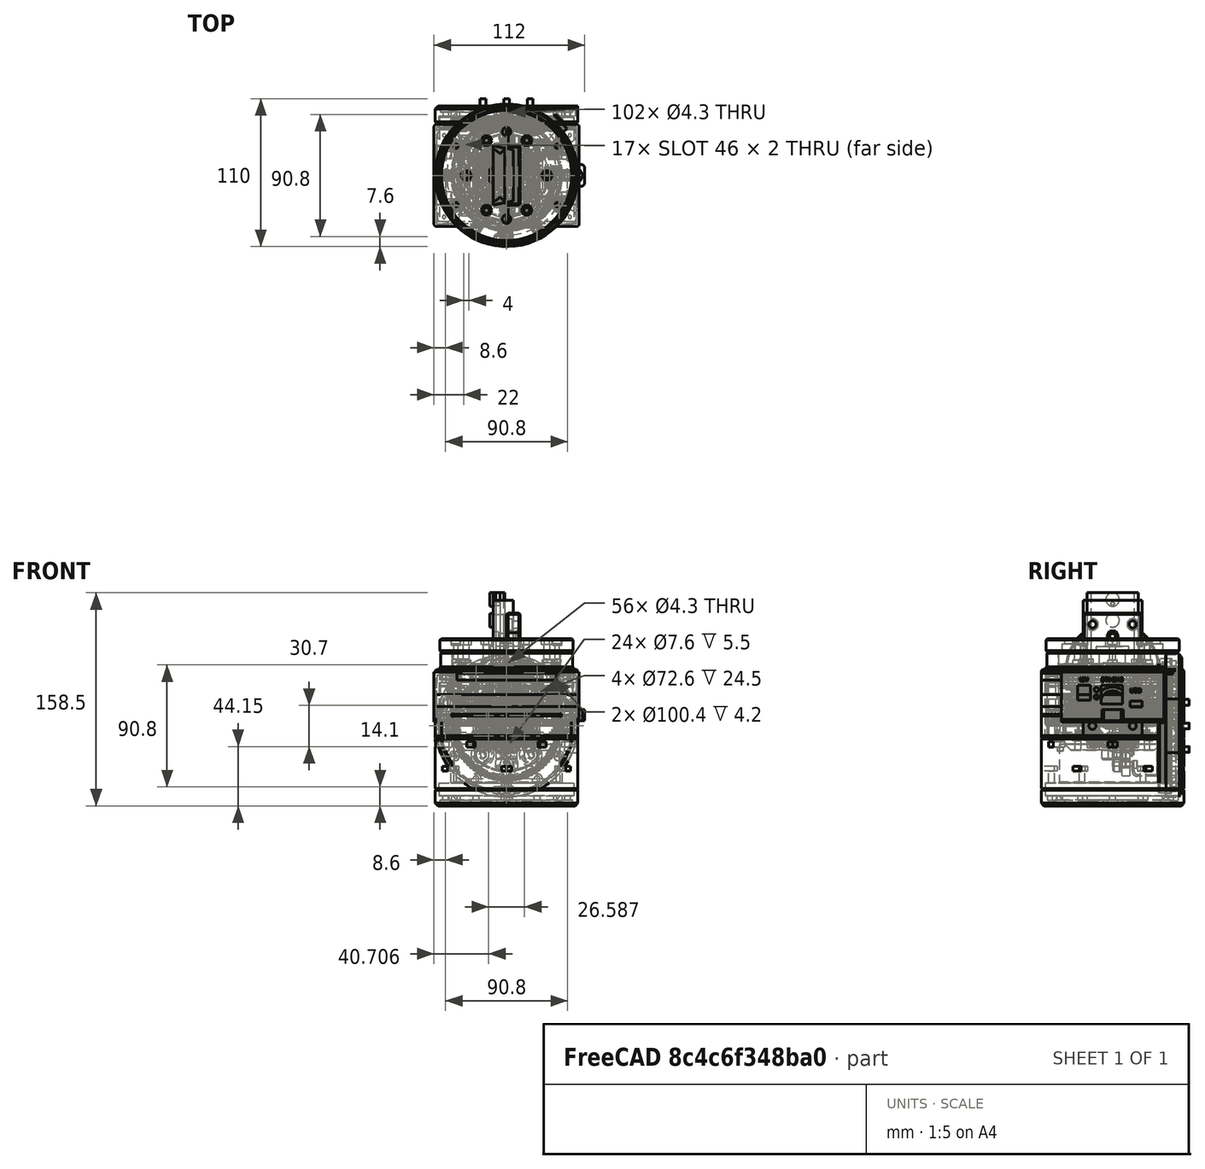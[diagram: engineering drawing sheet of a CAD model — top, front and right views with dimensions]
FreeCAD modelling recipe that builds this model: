
FCSTD DOCUMENT  (FreeCAD 0.19R)
Label: HrEM
License: All rights reserved
LicenseURL: http://en.wikipedia.org/wiki/All_rights_reserved
objects: Part::Cylinder×298, Part::Refine×224, Part::MultiFuse×180, Part::Box×74, Part::Cut×71, Part::Prism×45, Part::Feature×42, Part::Chamfer×30, Part::FeaturePython×20, Part::Part2DObjectPython×13, Part::Extrusion×12, Part::Fillet×5, Part::Fuse×4, App::Part×3
note: 1018 computed .brp shape members not serialized (recipe doc carries the construction recipe); baked Part::Feature solids carry a one-line shape summary decoded from their .brp

FEATURE [Part::Feature] Part__Feature048  label="OUTPUT_SHAFT"
  Placement = pos=(0,0,-16) rot=(1,0,0;1.5708rad)
  shape: bbox 70.02 x 70.02 x 15.12 mm, 150 faces (baked)
FEATURE [Part::Feature] Part__Feature015  label="CIRCULAR_SPLINE"
  Placement = pos=(-3.943e-12,44,4.322e-12) rot=(1,0,0;3.14159rad)
  shape: bbox 100 x 10 x 100 mm, 706 faces (baked)
FEATURE [Part::Feature] Part__Feature014  label="FLEXGEAR"
  Placement = pos=(0,33.5,0) rot=(0,0,1;0rad)
  shape: bbox 81.18 x 57.96 x 81.18 mm, 699 faces (baked)
FEATURE [Part::FeaturePython] cycloidgear  # WARN: FeaturePython — macro-defined, semantics opaque (R4)
  AttacherType = Attacher::AttachEngine3D
  Placement = pos=(0,44,0) rot=(1,0,0;1.5708rad)
  backlash = 0
  beta = 0
  clearance = 0.25
  double_helix = false
  head = 0
  height = 10
  inner_diameter = 5
  module = 1
  numpoints = 15
  outer_diameter = 5
  teeth = 79
  version = 0.0.3
FEATURE [Part::Cylinder] Cylinder  label="Válec"
  Angle = 360
  AttacherType = Attacher::AttachEngine3D
  Height = 10
  Placement = pos=(0,44,0) rot=(1,0,0;1.5708rad)
  Radius = 50
FEATURE [Part::Cylinder] Cylinder001  label="Válec001"
  Angle = 360
  AttacherType = Attacher::AttachEngine3D
  Height = 10
  Placement = pos=(0,44,45.4) rot=(1,0,0;1.5708rad)
  Radius = 2.15
FEATURE [Part::Refine] Cylinder001001  label="Válec002"
  Placement = pos=(0,0,0) rot=(0,1,0;1.0472rad)
  Source = -> Cylinder001
FEATURE [Part::Refine] Cylinder001002  label="Válec003"
  Placement = pos=(0,0,0) rot=(0,1,0;2.0944rad)
  Source = -> Cylinder001
FEATURE [Part::Refine] Cylinder001003  label="Válec004"
  Placement = pos=(0,0,0) rot=(0,1,0;3.14159rad)
  Source = -> Cylinder001
FEATURE [Part::Refine] Cylinder001004  label="Válec005"
  Placement = pos=(0,0,0) rot=(0,1,0;4.18879rad)
  Source = -> Cylinder001
FEATURE [Part::Refine] Cylinder001005  label="Válec006"
  Placement = pos=(0,0,0) rot=(0,-1,0;1.0472rad)
  Source = -> Cylinder001
FEATURE [Part::MultiFuse] Fusion
  Shapes = -> [cycloidgear,Cylinder001,Cylinder001001,Cylinder001002,Cylinder001003,Cylinder001004,Cylinder001005]
FEATURE [Part::Chamfer] Chamfer
  Base = -> Cylinder
  Edges = 2 edges r=1: [Edge1,Edge3]
FEATURE [Part::Cut] Cut  label="CIRCULAR_79"
  Base = -> Chamfer
  Tool = -> Fusion
FEATURE [Part::Cylinder] Cylinder001006  label="Válec007"
  Angle = 360
  AttacherType = Attacher::AttachEngine3D
  Height = 10
  Placement = pos=(0,44,0) rot=(1,0,0;1.5708rad)
  Radius = 50
FEATURE [Part::FeaturePython] cycloidgear001  # WARN: FeaturePython — macro-defined, semantics opaque (R4)
  AttacherType = Attacher::AttachEngine3D
  Placement = pos=(0,43.5,0) rot=(1,0,0;1.5708rad)
  backlash = 0
  beta = 0
  clearance = 0.25
  double_helix = false
  head = 0
  height = 11
  inner_diameter = 5
  module = 0.55
  numpoints = 15
  outer_diameter = 5
  teeth = 145
  version = 0.0.3
FEATURE [Part::Cylinder] Cylinder001007  label="Válec008"
  Angle = 360
  AttacherType = Attacher::AttachEngine3D
  Height = 10
  Placement = pos=(0,44,45.4) rot=(1,0,0;1.5708rad)
  Radius = 2.15
FEATURE [Part::Chamfer] Chamfer001
  Base = -> Cylinder001006
  Edges = 2 edges r=1: [Edge1,Edge3]
FEATURE [Part::Refine] Cylinder001008  label="Válec009"
  Placement = pos=(0,0,0) rot=(0,1,0;2.0944rad)
  Source = -> Cylinder001007
FEATURE [Part::Refine] Cylinder001009  label="Válec010"
  Placement = pos=(0,0,0) rot=(0,1,0;1.0472rad)
  Source = -> Cylinder001007
FEATURE [Part::Refine] Cylinder001010  label="Válec011"
  Placement = pos=(0,0,0) rot=(0,1,0;4.18879rad)
  Source = -> Cylinder001007
FEATURE [Part::Refine] Cylinder001011  label="Válec012"
  Placement = pos=(0,0,0) rot=(0,-1,0;1.0472rad)
  Source = -> Cylinder001007
FEATURE [Part::Refine] Cylinder001012  label="Válec013"
  Placement = pos=(0,0,0) rot=(0,1,0;3.14159rad)
  Source = -> Cylinder001007
FEATURE [Part::MultiFuse] Fusion001
  Shapes = -> [cycloidgear001,Cylinder001007,Cylinder001009,Cylinder001008,Cylinder001012,Cylinder001010,Cylinder001011]
FEATURE [Part::Cut] Cut001  label="CIRCULAR_145"
  Base = -> Chamfer001
  Tool = -> Fusion001
FEATURE [Part::Cylinder] Cylinder001014  label="Válec015"
  Angle = 360
  AttacherType = Attacher::AttachEngine3D
  Height = 10
  Placement = pos=(0,44,0) rot=(1,0,0;1.5708rad)
  Radius = 50
FEATURE [Part::Cylinder] Cylinder001017  label="Válec018"
  Angle = 360
  AttacherType = Attacher::AttachEngine3D
  Height = 10
  Placement = pos=(0,44,45.4) rot=(1,0,0;1.5708rad)
  Radius = 2.15
FEATURE [Part::Refine] Cylinder001013  label="Válec014"
  Placement = pos=(0,0,0) rot=(0,-1,0;1.0472rad)
  Source = -> Cylinder001017
FEATURE [Part::Refine] Cylinder001015  label="Válec016"
  Placement = pos=(0,0,0) rot=(0,1,0;2.0944rad)
  Source = -> Cylinder001017
FEATURE [Part::Refine] Cylinder001016  label="Válec017"
  Placement = pos=(0,0,0) rot=(0,1,0;4.18879rad)
  Source = -> Cylinder001017
FEATURE [Part::FeaturePython] cycloidgear002  # WARN: FeaturePython — macro-defined, semantics opaque (R4)
  AttacherType = Attacher::AttachEngine3D
  Placement = pos=(0,44,0) rot=(1,0,0;1.5708rad)
  backlash = 0
  beta = 30
  clearance = 0.25
  double_helix = false
  head = 0
  height = 10
  inner_diameter = 5
  module = 0.792
  numpoints = 15
  outer_diameter = 5
  teeth = 101
  version = 0.0.3
FEATURE [Part::Chamfer] Chamfer002
  Base = -> Cylinder001014
  Edges = 2 edges r=1: [Edge1,Edge3]
FEATURE [Part::Refine] Cylinder001018  label="Válec019"
  Placement = pos=(0,0,0) rot=(0,1,0;1.0472rad)
  Source = -> Cylinder001017
FEATURE [Part::Refine] Cylinder001019  label="Válec020"
  Placement = pos=(0,0,0) rot=(0,1,0;3.14159rad)
  Source = -> Cylinder001017
FEATURE [Part::MultiFuse] Fusion002
  Shapes = -> [cycloidgear002,Cylinder001017,Cylinder001018,Cylinder001015,Cylinder001019,Cylinder001016,Cylinder001013]
FEATURE [Part::Cut] Cut002  label="CIRCULAR_101"
  Base = -> Chamfer002
  Tool = -> Fusion002
FEATURE [Part::FeaturePython] cycloidgear003  # WARN: FeaturePython — macro-defined, semantics opaque (R4)
  AttacherType = Attacher::AttachEngine3D
  Placement = pos=(0,44,0) rot=(1,0,0;1.5708rad)
  backlash = 0
  beta = 30
  clearance = 0.25
  double_helix = false
  head = 0
  height = 11
  inner_diameter = 5
  module = 0.792
  numpoints = 15
  outer_diameter = 5
  teeth = 101
  version = 0.0.3
FEATURE [Part::Cylinder] Cylinder001023  label="Válec024"
  Angle = 360
  AttacherType = Attacher::AttachEngine3D
  Height = 10
  Placement = pos=(0,44,45.4) rot=(1,0,0;1.5708rad)
  Radius = 2.15
FEATURE [Part::Refine] Cylinder001020  label="Válec021"
  Placement = pos=(0,0,0) rot=(0,1,0;4.18879rad)
  Source = -> Cylinder001023
FEATURE [Part::Refine] Cylinder001021  label="Válec022"
  Placement = pos=(0,0,0) rot=(0,-1,0;1.0472rad)
  Source = -> Cylinder001023
FEATURE [Part::Refine] Cylinder001022  label="Válec023"
  Placement = pos=(0,0,0) rot=(0,1,0;2.0944rad)
  Source = -> Cylinder001023
FEATURE [Part::Refine] Cylinder001024  label="Válec025"
  Placement = pos=(0,0,0) rot=(0,1,0;3.14159rad)
  Source = -> Cylinder001023
FEATURE [Part::Refine] Cylinder001025  label="Válec026"
  Placement = pos=(0,0,0) rot=(0,1,0;1.0472rad)
  Source = -> Cylinder001023
FEATURE [Part::MultiFuse] Fusion003
  Shapes = -> [cycloidgear003,Cylinder001023,Cylinder001025,Cylinder001022,Cylinder001024,Cylinder001020,Cylinder001021]
FEATURE [Part::Cylinder] Cylinder001026  label="Válec027"
  Angle = 360
  AttacherType = Attacher::AttachEngine3D
  Height = 10
  Placement = pos=(0,44,0) rot=(1,0,0;1.5708rad)
  Radius = 50
FEATURE [Part::Chamfer] Chamfer003
  Base = -> Cylinder001026
  Edges = 2 edges r=1: [Edge1,Edge3]
FEATURE [Part::Cut] Cut003
  Base = -> Chamfer003
  Tool = -> Fusion003
FEATURE [Part::Cylinder] cylinder
  Angle = 360
  AttacherType = Attacher::AttachEngine3D
  Height = 10
  Radius = 3
FEATURE [Part::Cylinder] cylinder001
  Angle = 360
  AttacherType = Attacher::AttachEngine3D
  Height = 10
  Placement = pos=(15,0,0) rot=(0,0,1;0rad)
  Radius = 3.5
FEATURE [Part::Cylinder] cylinder002
  Angle = 360
  AttacherType = Attacher::AttachEngine3D
  Height = 5
  Placement = pos=(15,0,0) rot=(0,0,1;0rad)
  Radius = 7
FEATURE [Part::Cylinder] cylinder003
  Angle = 360
  AttacherType = Attacher::AttachEngine3D
  Height = 10
  Placement = pos=(-15,0,0) rot=(0,0,1;0rad)
  Radius = 3.5
FEATURE [Part::Cylinder] cylinder004
  Angle = 360
  AttacherType = Attacher::AttachEngine3D
  Height = 5
  Placement = pos=(-15,0,0) rot=(0,0,1;0rad)
  Radius = 7
FEATURE [Part::Cylinder] cylinder005
  Angle = 360
  AttacherType = Attacher::AttachEngine3D
  Height = 10
  Placement = pos=(-25,0,0) rot=(0,0,1;0rad)
  Radius = 2.6
FEATURE [Part::Cylinder] cylinder006
  Angle = 360
  AttacherType = Attacher::AttachEngine3D
  Height = 10
  Placement = pos=(25,0,0) rot=(0,0,1;0rad)
  Radius = 2.6
FEATURE [Part::MultiFuse] union
  Shapes = -> [cylinder,cylinder001,cylinder002,cylinder003,cylinder004,cylinder005,cylinder006]
FEATURE [Part::Cylinder] Cylinder001027  label="Válec028"
  Angle = 360
  AttacherType = Attacher::AttachEngine3D
  Height = 10
  Radius = 35
FEATURE [Part::Cut] Cut004  label="H1"
  Base = -> Cylinder001027
  Placement = pos=(0,0,10) rot=(0,0,1;0rad)
  Tool = -> union
FEATURE [Part::Cylinder] Cylinder001028  label="H2"
  Angle = 360
  AttacherType = Attacher::AttachEngine3D
  Height = 10
  Radius = 35
FEATURE [Part::Cylinder] Cylinder001029  label="Válec030"
  Angle = 360
  AttacherType = Attacher::AttachEngine3D
  Height = 16
  Placement = pos=(0,24,-6) rot=(0,0,1;0rad)
  Radius = 2.15
FEATURE [Part::Cylinder] cylinder007
  Angle = 360
  AttacherType = Attacher::AttachEngine3D
  Height = 10
  Placement = pos=(-25,0,0) rot=(0,0,1;0rad)
  Radius = 2.6
FEATURE [Part::Cylinder] cylinder008
  Angle = 360
  AttacherType = Attacher::AttachEngine3D
  Height = 10
  Placement = pos=(25,0,0) rot=(0,0,1;0rad)
  Radius = 2.6
FEATURE [Part::Cylinder] cylinder009
  Angle = 360
  AttacherType = Attacher::AttachEngine3D
  Height = 10
  Radius = 3
FEATURE [Part::Cylinder] Cylinder001030  label="Válec031"
  Angle = 360
  AttacherType = Attacher::AttachEngine3D
  Height = 4
  Placement = pos=(0,24,6) rot=(0,0,1;0rad)
  Radius = 3.6
FEATURE [Part::MultiFuse] Fusion004  label="Imbus"
  Shapes = -> [Cylinder001030,Cylinder001029]
FEATURE [Part::Refine] Fusion004001  label="Imbus001"
  Placement = pos=(0,0,0) rot=(0,0,1;1.0472rad)
  Source = -> Fusion004
FEATURE [Part::Refine] Fusion004002  label="Imbus002"
  Placement = pos=(0,0,0) rot=(0,0,1;2.0944rad)
  Source = -> Fusion004
FEATURE [Part::Refine] Fusion004003  label="Imbus003"
  Placement = pos=(0,0,0) rot=(0,0,1;3.14159rad)
  Source = -> Fusion004
FEATURE [Part::Refine] Fusion004004  label="Imbus004"
  Placement = pos=(0,0,0) rot=(0,0,1;4.18879rad)
  Source = -> Fusion004
FEATURE [Part::Refine] Fusion004005  label="Imbus005"
  Placement = pos=(0,0,0) rot=(0,0,-1;1.0472rad)
  Source = -> Fusion004
FEATURE [Part::FeaturePython] Nut  label="M5-Nut"  # Fasteners workbench fastener (typed FeaturePython)
  Placement = pos=(25,0,0) rot=(0.894427,0,0.447214;0rad)
  diameter = 7
  invert = false
  matchOuter = false
  offset = 0
  thread = false
  type = 7
FEATURE [Part::FeaturePython] Nut001  label="M5-Nut001"  # Fasteners workbench fastener (typed FeaturePython)
  Placement = pos=(-25,0,0) rot=(0.894427,0,0.447214;0rad)
  diameter = 7
  invert = false
  matchOuter = false
  offset = 0
  thread = false
  type = 7
FEATURE [Part::MultiFuse] Fusion004006
  Shapes = -> [cylinder007,cylinder008,cylinder009,Fusion004,Fusion004001,Fusion004002,Fusion004003,Fusion004004,Fusion004005,Nut,Nut001]
FEATURE [Part::Cut] Cut005
  Base = -> Cylinder001028
  Tool = -> Fusion004006
FEATURE [Part::Chamfer] Chamfer004  label="HH1"
  Base = -> Cut004
  Edges = 2 edges r=1: [Edge1,Edge3]
FEATURE [Part::Chamfer] Chamfer005  label="HH2"
  Base = -> Cut005
  Edges = 2 edges r=1: [Edge1,Edge3]
FEATURE [Part::Feature] Part__Feature049  label="FLEXGEAR001"
  Placement = pos=(0,33.5,0) rot=(0,0,1;0rad)
  shape: bbox 81.18 x 57.96 x 81.18 mm, 699 faces (baked)
FEATURE [Part::FeaturePython] cycloidgear005  # WARN: FeaturePython — macro-defined, semantics opaque (R4)
  AttacherType = Attacher::AttachEngine3D
  Placement = pos=(0,43.5,0) rot=(1,0,0;1.5708rad)
  backlash = 0
  beta = 0
  clearance = 0.25
  double_helix = false
  head = 0
  height = 10.5
  inner_diameter = 5
  module = 0.79
  numpoints = 15
  outer_diameter = 5
  teeth = 100
  version = 0.0.3
FEATURE [Part::FeaturePython] Tube  # WARN: FeaturePython — macro-defined, semantics opaque (R4)
  AttacherType = Attacher::AttachEngine3D
  Height = 10
  InnerRadius = 36.5
  OuterRadius = 42
  Placement = pos=(0,35.75,0) rot=(1,0,0;1.5708rad)
FEATURE [Part::Chamfer] Chamfer007
  Base = -> Tube
  Edges = 1 edges r=4: [Edge5]
FEATURE [Part::Cut] Cut007
  Base = -> cycloidgear005
  Tool = -> Chamfer007
FEATURE [Part::Cylinder] Cylinder001038  label="Válec039"
  Angle = 360
  AttacherType = Attacher::AttachEngine3D
  Height = 10.5
  Placement = pos=(0,43.5,0) rot=(1,0,0;1.5708rad)
  Radius = 42
FEATURE [Part::Cylinder] Cylinder001039  label="Válec040"
  Angle = 360
  AttacherType = Attacher::AttachEngine3D
  Height = 10.5
  Placement = pos=(0,43.5,0) rot=(1,0,0;1.5708rad)
  Radius = 36.3
FEATURE [Part::Cut] Cut008
  Base = -> Part__Feature049
  Tool = -> Cylinder001038
FEATURE [Part::MultiFuse] Fusion004008
  Shapes = -> [Cut007,Cut008]
FEATURE [Part::Cut] Cut009  label="FLEX100"
  Base = -> Fusion004008
  Tool = -> Cylinder001039
FEATURE [Part::Refine] Cut009001  label="FLEX100n"
  Source = -> Cut009
FEATURE [Part::FeaturePython] cycloidgear006  # WARN: FeaturePython — macro-defined, semantics opaque (R4)
  AttacherType = Attacher::AttachEngine3D
  Placement = pos=(0,43.5,0) rot=(1,0,0;1.5708rad)
  backlash = 0
  beta = 0
  clearance = 0.25
  double_helix = false
  head = 0
  height = 10.5
  inner_diameter = 5
  module = 1
  numpoints = 15
  outer_diameter = 5
  teeth = 78
  version = 0.0.3
FEATURE [Part::Feature] Part__Feature050  label="FLEXGEAR002"
  Placement = pos=(0,33.5,0) rot=(0,0,1;0rad)
  shape: bbox 81.18 x 57.96 x 81.18 mm, 699 faces (baked)
FEATURE [Part::FeaturePython] Tube001  # WARN: FeaturePython — macro-defined, semantics opaque (R4)
  AttacherType = Attacher::AttachEngine3D
  Height = 10
  InnerRadius = 36.5
  OuterRadius = 42
  Placement = pos=(0,35.75,0) rot=(1,0,0;1.5708rad)
FEATURE [Part::Chamfer] Chamfer008
  Base = -> Tube001
  Edges = 1 edges r=4: [Edge5]
FEATURE [Part::Cut] Cut009002
  Base = -> cycloidgear006
  Tool = -> Chamfer008
FEATURE [Part::Cylinder] Cylinder001040  label="Válec041"
  Angle = 360
  AttacherType = Attacher::AttachEngine3D
  Height = 11.5
  Placement = pos=(0,43.5,0) rot=(1,0,0;1.5708rad)
  Radius = 36.3
FEATURE [Part::Cylinder] Cylinder001041  label="Válec042"
  Angle = 360
  AttacherType = Attacher::AttachEngine3D
  Height = 10.5
  Placement = pos=(0,43.5,0) rot=(1,0,0;1.5708rad)
  Radius = 42
FEATURE [Part::Cut] Cut009004
  Base = -> Part__Feature050
  Tool = -> Cylinder001041
FEATURE [Part::MultiFuse] Fusion004009
  Shapes = -> [Cut009002,Cut009004]
FEATURE [Part::Cut] Cut009003  label="FLEX78"
  Base = -> Fusion004009
  Tool = -> Cylinder001040
FEATURE [Part::Refine] Cut009003001  label="FLEX78n"
  Source = -> Cut009003
FEATURE [Part::FeaturePython] cycloidgear007  # WARN: FeaturePython — macro-defined, semantics opaque (R4)
  AttacherType = Attacher::AttachEngine3D
  Placement = pos=(0,43.5,0) rot=(1,0,0;1.5708rad)
  backlash = 0
  beta = 0
  clearance = 0.25
  double_helix = false
  head = 0
  height = 10.5
  inner_diameter = 5
  module = 0.55
  numpoints = 15
  outer_diameter = 5
  teeth = 144
  version = 0.0.3
FEATURE [Part::Feature] Part__Feature051  label="FLEXGEAR003"
  Placement = pos=(0,33.5,0) rot=(0,0,1;0rad)
  shape: bbox 81.18 x 57.96 x 81.18 mm, 699 faces (baked)
FEATURE [Part::FeaturePython] Tube002  # WARN: FeaturePython — macro-defined, semantics opaque (R4)
  AttacherType = Attacher::AttachEngine3D
  Height = 10
  InnerRadius = 36.5
  OuterRadius = 42
  Placement = pos=(0,35.75,0) rot=(1,0,0;1.5708rad)
FEATURE [Part::Chamfer] Chamfer009
  Base = -> Tube002
  Edges = 1 edges r=4: [Edge5]
FEATURE [Part::Cut] Cut009003002
  Base = -> cycloidgear007
  Tool = -> Chamfer009
FEATURE [Part::Cylinder] Cylinder001042  label="Válec043"
  Angle = 360
  AttacherType = Attacher::AttachEngine3D
  Height = 11.5
  Placement = pos=(0,43.5,0) rot=(1,0,0;1.5708rad)
  Radius = 36.3
FEATURE [Part::Cylinder] Cylinder001043  label="Válec044"
  Angle = 360
  AttacherType = Attacher::AttachEngine3D
  Height = 10.5
  Placement = pos=(0,43.5,0) rot=(1,0,0;1.5708rad)
  Radius = 42
FEATURE [Part::Cut] Cut009003004
  Base = -> Part__Feature051
  Tool = -> Cylinder001043
FEATURE [Part::MultiFuse] Fusion004010
  Shapes = -> [Cut009003002,Cut009003004]
FEATURE [Part::Cut] Cut009003003  label="FLEX144"
  Base = -> Fusion004010
  Tool = -> Cylinder001042
FEATURE [Part::Refine] Cut009003003001  label="FLEX144n"
  Source = -> Cut009003003
FEATURE [Part::Feature] Part__Feature030  label="MOTOR_CAP"
  Placement = pos=(0,0,0) rot=(0,1,0;0.523599rad)
  shape: bbox 106 x 12.2 x 106 mm, 94 faces (baked)
FEATURE [Part::Cylinder] Cylinder014005699  label="Válec616"
  Angle = 360
  AttacherType = Attacher::AttachEngine3D
  Height = 10
  Placement = pos=(-9.9,9.9,0) rot=(0,0,1;0rad)
  Radius = 1.6
FEATURE [Part::Cylinder] Cylinder014005700  label="Válec617"
  Angle = 360
  AttacherType = Attacher::AttachEngine3D
  Height = 10
  Placement = pos=(-9.9,-9.9,0) rot=(0,0,1;0rad)
  Radius = 1.6
FEATURE [Part::Cylinder] Cylinder014005701  label="Válec618"
  Angle = 360
  AttacherType = Attacher::AttachEngine3D
  Height = 10
  Placement = pos=(9.9,-9.9,0) rot=(0,0,1;0rad)
  Radius = 1.6
FEATURE [Part::Cylinder] Cylinder014005703  label="Válec619"
  Angle = 360
  AttacherType = Attacher::AttachEngine3D
  Height = 10
  Placement = pos=(9.9,9.9,0) rot=(0,0,1;0rad)
  Radius = 1.6
FEATURE [Part::MultiFuse] Fusion004011  label="Diry PG"
  Shapes = -> [Cylinder014005699,Cylinder014005703,Cylinder014005700,Cylinder014005701]
FEATURE [Part::Box] Box001  label="Krychle001"
  AttacherType = Attacher::AttachEngine3D
  Height = 40
  Length = 10
  Placement = pos=(43,39.5,-20) rot=(0,0,1;0rad)
  Width = 12
FEATURE [Part::Cylinder] Cylinder014005822  label="Válec735"
  Angle = 360
  AttacherType = Attacher::AttachEngine3D
  Height = 12
  Placement = pos=(0,51.5,0) rot=(1,0,0;1.5708rad)
  Radius = 51
FEATURE [Part::FeaturePython] Tube003  label="B6010"  # WARN: FeaturePython — macro-defined, semantics opaque (R4)
  AttacherType = Attacher::AttachEngine3D
  Height = 16
  InnerRadius = 25
  OuterRadius = 40
FEATURE [Part::Cut] Cut009003003003  label="Lista prac"
  Base = -> Box001
  Tool = -> Cylinder014005822
FEATURE [Part::Cylinder] Cylinder014005826  label="Válec739"
  Angle = 360
  AttacherType = Attacher::AttachEngine3D
  Height = 4
  Placement = pos=(0,17.5,0) rot=(0,0,1;0rad)
  Radius = 3.6
FEATURE [Part::Cylinder] Cylinder014005827  label="Válec740"
  Angle = 360
  AttacherType = Attacher::AttachEngine3D
  Height = 4
  Placement = pos=(-17.5,0,0) rot=(0,0,1;0rad)
  Radius = 3.6
FEATURE [Part::Cylinder] Cylinder014005828  label="Válec741"
  Angle = 360
  AttacherType = Attacher::AttachEngine3D
  Height = 4
  Placement = pos=(17.5,0,0) rot=(0,0,1;0rad)
  Radius = 3.6
FEATURE [Part::Cylinder] Cylinder014005834  label="Válec747"
  Angle = 360
  AttacherType = Attacher::AttachEngine3D
  Height = 4
  Placement = pos=(0,-17.5,0) rot=(0,0,1;0rad)
  Radius = 3.6
FEATURE [Part::MultiFuse] Fusion001089086  label="Diry HG002"
  Placement = pos=(0,0,-1) rot=(0,0,1;0rad)
  Shapes = -> [Cylinder014005828,Cylinder014005834,Cylinder014005827,Cylinder014005826]
FEATURE [Part::Cylinder] Cylinder014005835  label="Válec748"
  Angle = 360
  AttacherType = Attacher::AttachEngine3D
  Height = 10
  Placement = pos=(17.5,0,0) rot=(0,0,1;0rad)
  Radius = 2.15
FEATURE [Part::Cylinder] Cylinder014005836  label="Válec749"
  Angle = 360
  AttacherType = Attacher::AttachEngine3D
  Height = 10
  Placement = pos=(-17.5,0,0) rot=(0,0,1;0rad)
  Radius = 2.15
FEATURE [Part::Cylinder] Cylinder014005837  label="Válec750"
  Angle = 360
  AttacherType = Attacher::AttachEngine3D
  Height = 10
  Placement = pos=(0,17.5,0) rot=(0,0,1;0rad)
  Radius = 2.15
FEATURE [Part::Cylinder] Cylinder014005838  label="Válec751"
  Angle = 360
  AttacherType = Attacher::AttachEngine3D
  Height = 10
  Placement = pos=(0,-17.5,0) rot=(0,0,1;0rad)
  Radius = 2.15
FEATURE [Part::MultiFuse] Fusion001089087  label="Diry HG003"
  Shapes = -> [Cylinder014005835,Cylinder014005838,Cylinder014005836,Cylinder014005837]
FEATURE [Part::MultiFuse] Fusion001089085  label="GeerHD"
  Placement = pos=(0,47,0) rot=(-1,0,0;1.5708rad)
  Shapes = -> [Fusion001089087,Fusion001089086]
FEATURE [Part::Cylinder] Cylinder014005814  label="Válec727"
  Angle = 360
  AttacherType = Attacher::AttachEngine3D
  Height = 3
  Placement = pos=(9.9,9.9,0) rot=(0,0,1;0rad)
  Radius = 2.8
FEATURE [Part::Cylinder] Cylinder014005815  label="Válec728"
  Angle = 360
  AttacherType = Attacher::AttachEngine3D
  Height = 3
  Placement = pos=(9.9,-9.9,0) rot=(0,0,1;0rad)
  Radius = 2.8
FEATURE [Part::Cylinder] Cylinder014005816  label="Válec729"
  Angle = 360
  AttacherType = Attacher::AttachEngine3D
  Height = 3
  Placement = pos=(-9.9,-9.9,0) rot=(0,0,1;0rad)
  Radius = 2.8
FEATURE [Part::Cylinder] Cylinder014005817  label="Válec730"
  Angle = 360
  AttacherType = Attacher::AttachEngine3D
  Height = 3
  Placement = pos=(-9.9,9.9,0) rot=(0,0,1;0rad)
  Radius = 2.8
FEATURE [Part::MultiFuse] Fusion001089081  label="Diry PG001"
  Shapes = -> [Cylinder014005817,Cylinder014005814,Cylinder014005816,Cylinder014005815]
FEATURE [Part::MultiFuse] Fusion001089083  label="GeerPG"
  Placement = pos=(0,47,0) rot=(-1,0,0;1.5708rad)
  Shapes = -> [Fusion004011,Fusion001089081]
FEATURE [Part::Feature] Part__Feature052  label="MOTOR_CAP001"
  Placement = pos=(0,0,0) rot=(0,1,0;0.523599rad)
  shape: bbox 106 x 12.2 x 106 mm, 94 faces (baked)
FEATURE [Part::Cut] Cut009003003004  label="MotorPG"
  Base = -> Part__Feature052
  Tool = -> Fusion001089083
FEATURE [Part::Feature] Cut005_solid  label="Planetary Gear Box distance  RA"
  shape: bbox 41 x 41 x 22.5 mm, 15 faces (baked)
FEATURE [Part::Cylinder] Cylinder014005839  label="Válec752"
  Angle = 360
  AttacherType = Attacher::AttachEngine3D
  Height = 22.5
  Placement = pos=(15.5,15.5,0) rot=(0,0,1;0rad)
  Radius = 1.3
FEATURE [Part::Cylinder] Cylinder014005840  label="Válec753"
  Angle = 360
  AttacherType = Attacher::AttachEngine3D
  Height = 22.5
  Placement = pos=(-15.5,15.5,0) rot=(0,0,1;0rad)
  Radius = 1.3
FEATURE [Part::Cylinder] Cylinder014005841  label="Válec754"
  Angle = 360
  AttacherType = Attacher::AttachEngine3D
  Height = 22.5
  Placement = pos=(15.5,-15.5,0) rot=(0,0,1;0rad)
  Radius = 1.3
FEATURE [Part::Cylinder] Cylinder014005842  label="Válec755"
  Angle = 360
  AttacherType = Attacher::AttachEngine3D
  Height = 22.5
  Placement = pos=(-15.5,-15.5,0) rot=(0,0,1;0rad)
  Radius = 1.3
FEATURE [Part::MultiFuse] Fusion001089088
  Shapes = -> [Cylinder014005839,Cylinder014005840,Cylinder014005841,Cylinder014005842]
FEATURE [Part::Cylinder] Cylinder014005843  label="Válec756"
  Angle = 360
  AttacherType = Attacher::AttachEngine3D
  Height = 22.5
  Placement = pos=(15.5,15.5,0) rot=(0,0,1;0rad)
  Radius = 2
FEATURE [Part::Cylinder] Cylinder014005844  label="Válec757"
  Angle = 360
  AttacherType = Attacher::AttachEngine3D
  Height = 22.5
  Placement = pos=(-15.5,15.5,0) rot=(0,0,1;0rad)
  Radius = 2
FEATURE [Part::Cylinder] Cylinder014005845  label="Válec758"
  Angle = 360
  AttacherType = Attacher::AttachEngine3D
  Height = 22.5
  Placement = pos=(15.5,-15.5,0) rot=(0,0,1;0rad)
  Radius = 2
FEATURE [Part::Cylinder] Cylinder014005846  label="Válec759"
  Angle = 360
  AttacherType = Attacher::AttachEngine3D
  Height = 22.5
  Placement = pos=(-15.5,-15.5,0) rot=(0,0,1;0rad)
  Radius = 2
FEATURE [Part::MultiFuse] Fusion001089089
  Shapes = -> [Cylinder014005843,Cylinder014005844,Cylinder014005845,Cylinder014005846,Cut005_solid]
FEATURE [Part::Cut] Cut009003003005  label="PlantH"
  Base = -> Fusion001089089
  Tool = -> Fusion001089088
FEATURE [Part::Feature] Part__Feature011  label="606ZZ003"
  Placement = pos=(17.9237,7,-21.3677) rot=(0.707107,0.707107,0;3.14159rad)
  shape: bbox 18.4 x 6 x 18.4 mm, 16 faces (baked)
FEATURE [Part::Feature] Part__Feature013  label="606ZZ005"
  Placement = pos=(17.9237,7,21.3677) rot=(0.707107,0.707107,0;3.14159rad)
  shape: bbox 18.4 x 6 x 18.4 mm, 16 faces (baked)
FEATURE [Part::Feature] Part__Feature012  label="606ZZ004"
  Placement = pos=(-17.9237,7,21.3677) rot=(0.707107,0.707107,0;3.14159rad)
  shape: bbox 18.4 x 6 x 18.4 mm, 16 faces (baked)
FEATURE [Part::Feature] Part__Feature005  label="SQ_NUT_M005"
  Placement = pos=(9.1,9.5075,-1e-15) rot=(0,0,1;1.5708rad)
  shape: bbox 3.1 x 7.8 x 7.8 mm, 7 faces (baked)
FEATURE [Part::Feature] Part__Feature009  label="M4x017"
  Placement = pos=(-12,9.5075,1.2e-14) rot=(0,0,1;1.5708rad)
  shape: bbox 14 x 7 x 7 mm, 5 faces (baked)
FEATURE [Part::Feature] Part__Feature001  label="WAVE_BEARING_CAP"
  Placement = pos=(0,0,0) rot=(1,0,0;1.5708rad)
  shape: bbox 70.52 x 49.37 x 8.25 mm, 105 faces (baked)
FEATURE [Part::Feature] Part__Feature010  label="606ZZ002"
  Placement = pos=(-17.9237,7,-21.3677) rot=(0.707107,0.707107,0;3.14159rad)
  shape: bbox 18.4 x 6 x 18.4 mm, 16 faces (baked)
FEATURE [Part::Feature] Part__Feature008  label="M4x10"
  Placement = pos=(12,9.5075,-8e-15) rot=(0,0,-1;1.5708rad)
  shape: bbox 14 x 7 x 7 mm, 5 faces (baked)
FEATURE [Part::Feature] Part__Feature004  label="SQ_NUT_M4"
  Placement = pos=(-6,9.5075,1e-15) rot=(0,0,1;1.5708rad)
  shape: bbox 3.1 x 7.8 x 7.8 mm, 7 faces (baked)
FEATURE [Part::Feature] Part__Feature003  label="606ZZ001"
  Placement = pos=(1.1e-14,7,28.5) rot=(0.707107,0.707107,0;3.14159rad)
  shape: bbox 18.4 x 6 x 18.4 mm, 16 faces (baked)
FEATURE [Part::Feature] Part__Feature007  label="M4x016"
  Placement = pos=(-7.9e-15,15.25,-28.5) rot=(0,0,1;0rad)
  shape: bbox 5.5 x 18 x 5.5 mm, 5 faces (baked)
FEATURE [Part::Feature] Part__Feature  label="WAVE_BEARING_PLATE"
  shape: bbox 49.37 x 14 x 70.52 mm, 157 faces (baked)
FEATURE [Part::Feature] Part__Feature006  label="M4x15"
  Placement = pos=(1.2e-15,15.25,28.5) rot=(0,0,1;0rad)
  shape: bbox 5.5 x 18 x 5.5 mm, 5 faces (baked)
FEATURE [Part::Feature] Part__Feature002  label="606ZZ"
  Placement = pos=(-1.1e-14,7,-28.5) rot=(0.707107,0.707107,0;3.14159rad)
  shape: bbox 18.4 x 6 x 18.4 mm, 16 faces (baked)
FEATURE [App::Part] WAVE_GEN1_ASM
  Group = -> [Part__Feature,Part__Feature002,Part__Feature003,Part__Feature004,Part__Feature005,Part__Feature006,Part__Feature007,Part__Feature008,Part__Feature009,Part__Feature010,Part__Feature011,Part__Feature012,Part__Feature013]
  Origin = -> Origin001
  Placement = pos=(-2.4e-15,27.5,1.1e-15) rot=(0,1,0;3.14159rad)
FEATURE [Part::Feature] Part__Feature053  label="WAVE_BEARING_PLATE001"
  Placement = pos=(0,0,0) rot=(1,0,0;1.5708rad)
  shape: bbox 49.37 x 70.52 x 14 mm, 157 faces (baked)
FEATURE [Part::Cylinder] Cylinder014005847  label="Válec760"
  Angle = 360
  AttacherType = Attacher::AttachEngine3D
  Height = 14
  Radius = 4
FEATURE [Part::Cylinder] Cylinder014005848  label="Válec761"
  Angle = 360
  AttacherType = Attacher::AttachEngine3D
  Height = 3
  Placement = pos=(0,28.5,0) rot=(0,0,1;0rad)
  Radius = 2.9
FEATURE [Part::Cylinder] Cylinder014005849  label="Válec762"
  Angle = 360
  AttacherType = Attacher::AttachEngine3D
  Height = 3
  Placement = pos=(0,-28.5,0) rot=(0,0,1;0rad)
  Radius = 2.9
FEATURE [Part::Cylinder] Cylinder014005854  label="Valec"
  Angle = 360
  AttacherType = Attacher::AttachEngine3D
  Height = 30
  Placement = pos=(-15,0,9) rot=(0,1,0;1.5708rad)
  Radius = 2.5
FEATURE [Part::FeaturePython] Tube004  # WARN: FeaturePython — macro-defined, semantics opaque (R4)
  AttacherType = Attacher::AttachEngine3D
  Height = 4
  InnerRadius = 4.2
  OuterRadius = 8
FEATURE [Part::Cylinder] Cylinder014005855  label="Válec768"
  Angle = 360
  AttacherType = Attacher::AttachEngine3D
  Height = 1
  Radius = 7
FEATURE [Part::Cut] Cut009003003007  label="ring"
  Base = -> Tube004
  Tool = -> Cylinder014005855
FEATURE [Part::Prism] prism  label="M4X"
  AttacherType = Attacher::AttachEngine3D
  Circumradius = 4.21
  FirstAngle = 0
  Height = 8.4
  Placement = pos=(0,23,-12.8) rot=(0,0,1;0rad)
  Polygon = 6
  SecondAngle = 0
FEATURE [Part::Feature] Part__Feature054  label="OUTPUT_SHAFT001"
  Placement = pos=(0,0,-17) rot=(1,0,0;1.5708rad)
  shape: bbox 70.02 x 70.02 x 15.12 mm, 150 faces (baked)
FEATURE [Part::Feature] Part__Feature055  label="M4_NUT017"
  Placement = pos=(0,0.1,15.35) rot=(0,1,0;0.523599rad)
  shape: bbox 7 x 3.2 x 8.083 mm, 9 faces (baked)
FEATURE [Part::Feature] Part__Feature056  label="M4x029"
  Placement = pos=(-13.2935,9.5,7.675) rot=(0,1,0;2.0944rad)
  shape: bbox 7 x 14 x 7 mm, 5 faces (baked)
FEATURE [Part::Feature] Part__Feature016  label="HOUSING"
  Placement = pos=(0,0,-52.5) rot=(1,0,0;1.5708rad)
  shape: bbox 106 x 106 x 39.4 mm, 163 faces (baked)
FEATURE [Part::Cylinder] Cylinder014005856  label="H003"
  Angle = 360
  AttacherType = Attacher::AttachEngine3D
  Height = 8
  Radius = 35
FEATURE [Part::Cylinder] Cylinder014005857  label="Válec769"
  Angle = 360
  AttacherType = Attacher::AttachEngine3D
  Height = 16
  Placement = pos=(0,24,-6) rot=(0,0,1;0rad)
  Radius = 2.15
FEATURE [Part::Cylinder] Cylinder014005858  label="Válec770"
  Angle = 360
  AttacherType = Attacher::AttachEngine3D
  Height = 4
  Placement = pos=(0,24,6) rot=(0,0,1;0rad)
  Radius = 3.6
FEATURE [Part::MultiFuse] Fusion001089094  label="Imbus006"
  Shapes = -> [Cylinder014005858,Cylinder014005857]
FEATURE [Part::Refine] Fusion001089095  label="Imbus007"
  Placement = pos=(0,0,0) rot=(0,0,1;1.0472rad)
  Source = -> Fusion001089094
FEATURE [Part::Refine] Fusion001089096  label="Imbus008"
  Placement = pos=(0,0,0) rot=(0,0,1;2.0944rad)
  Source = -> Fusion001089094
FEATURE [Part::Refine] Fusion001089097  label="Imbus009"
  Placement = pos=(0,0,0) rot=(0,0,1;3.14159rad)
  Source = -> Fusion001089094
FEATURE [Part::Refine] Fusion001089098  label="Imbus010"
  Placement = pos=(0,0,0) rot=(0,0,1;4.18879rad)
  Source = -> Fusion001089094
FEATURE [Part::Refine] Fusion001089099  label="Imbus011"
  Placement = pos=(0,0,0) rot=(0,0,-1;1.0472rad)
  Source = -> Fusion001089094
FEATURE [Part::MultiFuse] Fusion001089100
  Shapes = -> [Fusion001089094,Fusion001089095,Fusion001089096,Fusion001089097,Fusion001089098,Fusion001089099]
FEATURE [Part::Cut] Cut009003003008  label="Old"
  Base = -> Cylinder014005856
  Tool = -> Fusion001089100
FEATURE [Part::Cylinder] Cylinder014005859  label="Válec771"
  Angle = 360
  AttacherType = Attacher::AttachEngine3D
  Height = 15.9
  Radius = 24.8
FEATURE [Part::Cylinder] Cylinder014005860  label="H004"
  Angle = 360
  AttacherType = Attacher::AttachEngine3D
  Height = 7.5
  Placement = pos=(0,0,-7.8) rot=(0,0,1;0rad)
  Radius = 35
FEATURE [Part::Cylinder] Cylinder014005861  label="Válec772"
  Angle = 360
  AttacherType = Attacher::AttachEngine3D
  Height = 20
  Placement = pos=(0,23,-15) rot=(0,0,1;0rad)
  Radius = 2.1
FEATURE [Part::MultiFuse] Fusion001089102  label="sroub"
  Shapes = -> [Cylinder014005861,prism]
FEATURE [Part::Refine] Fusion001089102001  label="sroub001"
  Placement = pos=(0,0,0) rot=(0,0,1;1.0472rad)
  Source = -> Fusion001089102
FEATURE [Part::Refine] Fusion001089102002  label="sroub002"
  Placement = pos=(0,0,0) rot=(0,0,1;2.0944rad)
  Source = -> Fusion001089102
FEATURE [Part::Refine] Fusion001089102003  label="sroub003"
  Placement = pos=(0,0,0) rot=(0,0,1;3.14159rad)
  Source = -> Fusion001089102
FEATURE [Part::Refine] Fusion001089102004  label="sroub004"
  Placement = pos=(0,0,0) rot=(0,0,1;4.18879rad)
  Source = -> Fusion001089102
FEATURE [Part::Refine] Fusion001089102005  label="sroub005"
  Placement = pos=(0,0,0) rot=(0,0,-1;1.0472rad)
  Source = -> Fusion001089102
FEATURE [Part::Prism] prism001  label="M4X001"
  AttacherType = Attacher::AttachEngine3D
  Circumradius = 7.86
  FirstAngle = 0
  Height = 5.5
  Placement = pos=(0,0,-15.5) rot=(0,0,1;0rad)
  Polygon = 6
  SecondAngle = 0
FEATURE [Part::Cylinder] Cylinder014005862  label="Válec773"
  Angle = 360
  AttacherType = Attacher::AttachEngine3D
  Height = 30
  Placement = pos=(0,0,-28) rot=(0,0,1;0rad)
  Radius = 3.15
FEATURE [Part::MultiFuse] Fusion001089102006
  Shapes = -> [Fusion001089102,Fusion001089102001,Fusion001089102002,Fusion001089102003,Fusion001089102004,Fusion001089102005,Cylinder014005862]
FEATURE [Part::Cylinder] Cylinder014005863  label="Válec774"
  Angle = 360
  AttacherType = Attacher::AttachEngine3D
  Height = 10.5
  Placement = pos=(0,0,-25) rot=(0,0,1;0rad)
  Radius = 7.75
FEATURE [Part::MultiFuse] Fusion001089101
  Shapes = -> [Part__Feature054,Cylinder014005860,Cylinder014005863]
FEATURE [Part::Cut] Cut009003003009  label="Out"
  Base = -> Fusion001089101
  Tool = -> Fusion001089102006
FEATURE [Part::Refine] Cut009003003009001
  Source = -> Cut009003003009
FEATURE [Part::Chamfer] Chamfer010  label="OutA"
  Base = -> Cut009003003009001
  Edges = 3 edges r=0.5: [Edge436,Edge437,Edge441]
FEATURE [Part::Cylinder] Cylinder014005865  label="H005"
  Angle = 360
  AttacherType = Attacher::AttachEngine3D
  Height = 12
  Placement = pos=(0,0,15.9) rot=(0,0,1;0rad)
  Radius = 35
FEATURE [Part::Cylinder] Cylinder014005866  label="Válec776"
  Angle = 360
  AttacherType = Attacher::AttachEngine3D
  Height = 28
  Placement = pos=(0,23,0) rot=(0,0,1;0rad)
  Radius = 2.1
FEATURE [Part::Cylinder] Cylinder014005867  label="Válec777"
  Angle = 360
  AttacherType = Attacher::AttachEngine3D
  Height = 4.1
  Placement = pos=(0,23,24) rot=(0,0,1;0rad)
  Radius = 3.45
FEATURE [Part::MultiFuse] Fusion001089102007  label="M4Inbus"
  Placement = pos=(0,0,0) rot=(0,0,1;2.0944rad)
  Shapes = -> [Cylinder014005866,Cylinder014005867]
FEATURE [Part::MultiFuse] Fusion001089102008
  Shapes = -> [Cylinder014005859,Cylinder014005865]
FEATURE [Part::Refine] Fusion001089102007001  label="M4Inbus001"
  Placement = pos=(0,0,0) rot=(0,0,1;1.0472rad)
  Source = -> Fusion001089102007
FEATURE [Part::Refine] Fusion001089102007002  label="M4Inbus002"
  Placement = pos=(0,0,0) rot=(0,0,1;2.0944rad)
  Source = -> Fusion001089102007
FEATURE [Part::Refine] Fusion001089102007003  label="M4Inbus003"
  Placement = pos=(0,0,0) rot=(0,0,1;3.14159rad)
  Source = -> Fusion001089102007
FEATURE [Part::Refine] Fusion001089102007004  label="M4Inbus004"
  Placement = pos=(0,0,0) rot=(0,0,1;4.18879rad)
  Source = -> Fusion001089102007
FEATURE [Part::Refine] Fusion001089102007005  label="M4Inbus005"
  Placement = pos=(0,0,0) rot=(0,0,-1;1.0472rad)
  Source = -> Fusion001089102007
FEATURE [Part::Cylinder] Cylinder014005868  label="Válec778"
  Angle = 360
  AttacherType = Attacher::AttachEngine3D
  Height = 28
  Radius = 3.15
FEATURE [Part::Cylinder] Cylinder014005869  label="Válec779"
  Angle = 360
  AttacherType = Attacher::AttachEngine3D
  Height = 28
  Placement = pos=(25,0,12) rot=(0,0,1;0rad)
  Radius = 2.65
FEATURE [Part::Prism] prism002  label="M4X002"
  AttacherType = Attacher::AttachEngine3D
  Circumradius = 4.6
  FirstAngle = 0
  Height = 8.4
  Placement = pos=(25,0,12) rot=(0,0,1;0rad)
  Polygon = 6
  SecondAngle = 0
FEATURE [Part::MultiFuse] Fusion001089102007007
  Shapes = -> [Cylinder014005869,prism002]
FEATURE [Part::Refine] Fusion001089102007007001
  Placement = pos=(0,0,0) rot=(0,0,1;3.14159rad)
  Source = -> Fusion001089102007007
FEATURE [Part::MultiFuse] Fusion001089102007006
  Shapes = -> [Fusion001089102007001,Fusion001089102007002,Fusion001089102007003,Fusion001089102007004,Fusion001089102007005,Cylinder014005868,Fusion001089102007,Fusion001089102007007,Fusion001089102007007001]
FEATURE [Part::Chamfer] Chamfer011
  Base = -> Fusion001089102008
  Edges = 3 edges r=0.75: [Edge1,Edge3,Edge6]
FEATURE [Part::Cut] Cut009003003009002  label="OutB"
  Base = -> Chamfer011
  Tool = -> Fusion001089102007006
FEATURE [Part::Cylinder] Cylinder014005870  label="Válec780"
  Angle = 360
  AttacherType = Attacher::AttachEngine3D
  Height = 16
  Placement = pos=(0,0,-8) rot=(0,0,1;0rad)
  Radius = 53
FEATURE [Part::Cylinder] Cylinder014005871  label="Válec781"
  Angle = 360
  AttacherType = Attacher::AttachEngine3D
  Height = 16
  Placement = pos=(0,0,-8) rot=(0,0,1;0rad)
  Radius = 36
FEATURE [Part::Cylinder] Cylinder014005872  label="Válec782"
  Angle = 360
  AttacherType = Attacher::AttachEngine3D
  Height = 16
  Placement = pos=(0,0,0.1) rot=(0,0,1;0rad)
  Radius = 40.05
FEATURE [Part::Cylinder] Cylinder014005873  label="Válec783"
  Angle = 360
  AttacherType = Attacher::AttachEngine3D
  Height = 24
  Placement = pos=(45,0,-16) rot=(0,0,1;0rad)
  Radius = 2.15
FEATURE [Part::Cylinder] Cylinder014005874  label="Válec784"
  Angle = 360
  AttacherType = Attacher::AttachEngine3D
  Height = 4
  Placement = pos=(45,0,4) rot=(0,0,1;0rad)
  Radius = 3.65
FEATURE [Part::MultiFuse] Fusion001089102007007003  label="inbusL1"
  Shapes = -> [Cylinder014005873,Cylinder014005874]
FEATURE [Part::Refine] Fusion001089102007007003001  label="inbusL002"
  Placement = pos=(0,0,0) rot=(0,0,1;1.0472rad)
  Source = -> Fusion001089102007007003
FEATURE [Part::Refine] Fusion001089102007007003002  label="inbusL003"
  Placement = pos=(0,0,0) rot=(0,0,1;2.0944rad)
  Source = -> Fusion001089102007007003
FEATURE [Part::Refine] Fusion001089102007007003003  label="inbusL004"
  Placement = pos=(0,0,0) rot=(0,0,1;3.14159rad)
  Source = -> Fusion001089102007007003
FEATURE [Part::Refine] Fusion001089102007007003004  label="inbusL005"
  Placement = pos=(0,0,0) rot=(0,0,1;4.18879rad)
  Source = -> Fusion001089102007007003
FEATURE [Part::Refine] Fusion001089102007007003005  label="inbusL006"
  Placement = pos=(0,0,0) rot=(0,0,-1;1.0472rad)
  Source = -> Fusion001089102007007003
FEATURE [Part::MultiFuse] Fusion001089102007007003006
  Shapes = -> [Fusion001089102007007003,Fusion001089102007007003001,Fusion001089102007007003002,Fusion001089102007007003003,Fusion001089102007007003004,Fusion001089102007007003005]
FEATURE [Part::Box] Box  label="Krychle"
  AttacherType = Attacher::AttachEngine3D
  Height = 16
  Length = 10
  Placement = pos=(43,-22,-8) rot=(0,0,1;0rad)
  Width = 44
FEATURE [Part::MultiFuse] Fusion001089102007007003007
  Shapes = -> [Cylinder014005870,Box]
FEATURE [Part::Prism] prism003  label="M4X003"
  AttacherType = Attacher::AttachEngine3D
  Circumradius = 4.21
  FirstAngle = 0
  Height = 3.4
  Placement = pos=(0,0,0) rot=(0,0,1;1.5708rad)
  Polygon = 6
  SecondAngle = 0
FEATURE [Part::Box] Box002  label="Krychle002"
  AttacherType = Attacher::AttachEngine3D
  Height = 3.4
  Length = 7
  Placement = pos=(-3.5,0,0) rot=(0,0,1;0rad)
  Width = 10
FEATURE [Part::Cylinder] Cylinder014005875  label="Válec785"
  Angle = 360
  AttacherType = Attacher::AttachEngine3D
  Height = 16
  Placement = pos=(0,0,-8) rot=(0,0,1;0rad)
  Radius = 2.15
FEATURE [Part::MultiFuse] Fusion001089102007007003008  label="M4nut"
  Placement = pos=(0,-45,0) rot=(0,0,1;0rad)
  Shapes = -> [Cylinder014005875,Box002,prism003]
FEATURE [Part::Refine] Fusion001089102007007003008001  label="M4nut001"
  Placement = pos=(0,0,0) rot=(0,0,1;1.0472rad)
  Source = -> Fusion001089102007007003008
FEATURE [Part::Refine] Fusion001089102007007003008002  label="M4nut002"
  Placement = pos=(0,0,0) rot=(0,0,1;2.0944rad)
  Source = -> Fusion001089102007007003008
FEATURE [Part::Refine] Fusion001089102007007003008003  label="M4nut003"
  Placement = pos=(0,0,0) rot=(0,0,1;3.14159rad)
  Source = -> Fusion001089102007007003008
FEATURE [Part::Refine] Fusion001089102007007003008004  label="M4nut004"
  Placement = pos=(0,0,0) rot=(0,0,1;4.18879rad)
  Source = -> Fusion001089102007007003008
FEATURE [Part::Refine] Fusion001089102007007003008005  label="M4nut005"
  Placement = pos=(0,0,0) rot=(0,0,-1;1.0472rad)
  Source = -> Fusion001089102007007003008
FEATURE [Part::MultiFuse] Fusion001089102007007003008006
  Shapes = -> [Fusion001089102007007003008,Fusion001089102007007003008001,Fusion001089102007007003008002,Fusion001089102007007003008003,Fusion001089102007007003008004,Fusion001089102007007003008005]
FEATURE [Part::Prism] prism004  label="M5X004"
  AttacherType = Attacher::AttachEngine3D
  Circumradius = 4.6
  FirstAngle = 0
  Height = 4.2
  Placement = pos=(0,0,0) rot=(0,1,0;1.5708rad)
  Polygon = 6
  SecondAngle = 0
FEATURE [Part::Box] Box003  label="Krychle003"
  AttacherType = Attacher::AttachEngine3D
  Height = 10
  Length = 4.1
  Placement = pos=(0,-4,0) rot=(0,0.707107,0.707107;0rad)
  Width = 8
FEATURE [Part::Cylinder] Cylinder014005876  label="Válec786"
  Angle = 360
  AttacherType = Attacher::AttachEngine3D
  Height = 14
  Placement = pos=(-4,0,0) rot=(0,1,0;1.5708rad)
  Radius = 2.65
FEATURE [Part::MultiFuse] Fusion001089102007007003008007  label="M5"
  Placement = pos=(45,15,0) rot=(0,0,1;0rad)
  Shapes = -> [prism004,Box003,Cylinder014005876]
FEATURE [Part::Box] Box004  label="Krychle004"
  AttacherType = Attacher::AttachEngine3D
  Height = 10
  Length = 4.1
  Placement = pos=(0,-4,0) rot=(0,0.707107,0.707107;0rad)
  Width = 8
FEATURE [Part::Cylinder] Cylinder014005877  label="Válec787"
  Angle = 360
  AttacherType = Attacher::AttachEngine3D
  Height = 14
  Placement = pos=(-4,0,0) rot=(0,1,0;1.5708rad)
  Radius = 2.65
FEATURE [Part::Prism] prism005  label="M5X005"
  AttacherType = Attacher::AttachEngine3D
  Circumradius = 4.6
  FirstAngle = 0
  Height = 4.2
  Placement = pos=(0,0,0) rot=(0,1,0;1.5708rad)
  Polygon = 6
  SecondAngle = 0
FEATURE [Part::MultiFuse] Fusion001089102007007003008008  label="M006"
  Placement = pos=(45,-15,0) rot=(0,0,1;0rad)
  Shapes = -> [prism005,Box004,Cylinder014005877]
FEATURE [Part::MultiFuse] Fusion001089102007007002
  Shapes = -> [Cylinder014005871,Cylinder014005872,Fusion001089102007007003006,Fusion001089102007007003008006,Fusion001089102007007003008007,Fusion001089102007007003008008]
FEATURE [Part::Cut] Cut009003003009003  label="OutC"
  Base = -> Fusion001089102007007003007
  Tool = -> Fusion001089102007007002
FEATURE [Part::Refine] Cut009003003009003001  label="OutC001"
  Source = -> Cut009003003009003
FEATURE [Part::Chamfer] Chamfer012  label="OutputC"
  Base = -> Cut009003003009003001
  Edges = 10 edges r=0.75: [Edge1,Edge3,Edge5,Edge7,Edge8,Edge10,Edge11,Edge12,Edge172,Edge300]
FEATURE [Part::Cylinder] Cylinder014005878  label="Válec788"
  Angle = 360
  AttacherType = Attacher::AttachEngine3D
  Height = 16
  Placement = pos=(0,0,8) rot=(0,0,1;0rad)
  Radius = 53
FEATURE [Part::Cylinder] Cylinder014005879  label="Válec789"
  Angle = 360
  AttacherType = Attacher::AttachEngine3D
  Height = 16
  Placement = pos=(0,0,8) rot=(0,0,1;0rad)
  Radius = 36
FEATURE [Part::Cylinder] Cylinder014005880  label="Válec790"
  Angle = 360
  AttacherType = Attacher::AttachEngine3D
  Height = 16
  Placement = pos=(0,0,-0.25) rot=(0,0,1;0rad)
  Radius = 40.05
FEATURE [Part::Cylinder] Cylinder014005881  label="Válec791"
  Angle = 360
  AttacherType = Attacher::AttachEngine3D
  Height = 24
  Placement = pos=(45,0,-16) rot=(0,0,1;0rad)
  Radius = 2.15
FEATURE [Part::Cylinder] Cylinder014005882  label="Válec792"
  Angle = 360
  AttacherType = Attacher::AttachEngine3D
  Height = 4
  Placement = pos=(45,0,4) rot=(0,0,1;0rad)
  Radius = 3.65
FEATURE [Part::MultiFuse] Fusion001089102007007003008013  label="inbusL010"
  Shapes = -> [Cylinder014005881,Cylinder014005882]
FEATURE [Part::Refine] Fusion001089102007007003008009  label="inbusL007"
  Placement = pos=(0,0,0) rot=(0,0,1;3.14159rad)
  Source = -> Fusion001089102007007003008013
FEATURE [Part::Refine] Fusion001089102007007003008011  label="inbusL008"
  Placement = pos=(0,0,0) rot=(0,0,1;2.0944rad)
  Source = -> Fusion001089102007007003008013
FEATURE [Part::Refine] Fusion001089102007007003008012  label="inbusL009"
  Placement = pos=(0,0,0) rot=(0,0,1;4.18879rad)
  Source = -> Fusion001089102007007003008013
FEATURE [Part::Refine] Fusion001089102007007003008014  label="inbusL011"
  Placement = pos=(0,0,0) rot=(0,0,-1;1.0472rad)
  Source = -> Fusion001089102007007003008013
FEATURE [Part::Refine] Fusion001089102007007003008015  label="inbusL012"
  Placement = pos=(0,0,0) rot=(0,0,1;1.0472rad)
  Source = -> Fusion001089102007007003008013
FEATURE [Part::MultiFuse] Fusion001089102007007003008010
  Placement = pos=(0,0,16) rot=(0,0,1;0.523599rad)
  Shapes = -> [Fusion001089102007007003008013,Fusion001089102007007003008015,Fusion001089102007007003008011,Fusion001089102007007003008009,Fusion001089102007007003008012,Fusion001089102007007003008014]
FEATURE [Part::MultiFuse] Fusion001089102007007003008016
  Shapes = -> [Cylinder014005879,Cylinder014005880,Fusion001089102007007003008010]
FEATURE [Part::Cut] Cut009003003009003002
  Base = -> Cylinder014005878
  Tool = -> Fusion001089102007007003008016
FEATURE [Part::Chamfer] Chamfer013  label="OutputD"
  Base = -> Cut009003003009003002
  Edges = 4 edges r=0.75: [Edge1,Edge3,Edge6,Edge13]
FEATURE [Part::Cylinder] Cylinder014005883  label="Válec793"
  Angle = 360
  AttacherType = Attacher::AttachEngine3D
  Height = 16
  Placement = pos=(0,0,-8) rot=(0,0,1;0rad)
  Radius = 53
FEATURE [Part::Cylinder] Cylinder014005884  label="Válec794"
  Angle = 360
  AttacherType = Attacher::AttachEngine3D
  Height = 16
  Placement = pos=(0,0,-8) rot=(0,0,1;0rad)
  Radius = 36
FEATURE [Part::Cylinder] Cylinder014005885  label="Válec795"
  Angle = 360
  AttacherType = Attacher::AttachEngine3D
  Height = 16
  Placement = pos=(0,0,0.1) rot=(0,0,1;0rad)
  Radius = 40.05
FEATURE [Part::Cylinder] Cylinder014005886  label="Válec796"
  Angle = 360
  AttacherType = Attacher::AttachEngine3D
  Height = 24
  Placement = pos=(45,0,-16) rot=(0,0,1;0rad)
  Radius = 2.15
FEATURE [Part::Cylinder] Cylinder014005887  label="Válec797"
  Angle = 360
  AttacherType = Attacher::AttachEngine3D
  Height = 4
  Placement = pos=(45,0,4) rot=(0,0,1;0rad)
  Radius = 3.65
FEATURE [Part::MultiFuse] Fusion001089102007007003008017  label="inbusL013"
  Shapes = -> [Cylinder014005886,Cylinder014005887]
FEATURE [Part::Refine] Fusion001089102007007003008018  label="inbusL014"
  Placement = pos=(0,0,0) rot=(0,0,1;4.18879rad)
  Source = -> Fusion001089102007007003008017
FEATURE [Part::Refine] Fusion001089102007007003008020  label="inbusL015"
  Placement = pos=(0,0,0) rot=(0,0,1;1.0472rad)
  Source = -> Fusion001089102007007003008017
FEATURE [Part::Refine] Fusion001089102007007003008021  label="inbusL016"
  Placement = pos=(0,0,0) rot=(0,0,1;2.0944rad)
  Source = -> Fusion001089102007007003008017
FEATURE [Part::Refine] Fusion001089102007007003008022  label="inbusL017"
  Placement = pos=(0,0,0) rot=(0,0,1;3.14159rad)
  Source = -> Fusion001089102007007003008017
FEATURE [Part::Refine] Fusion001089102007007003008023  label="inbusL018"
  Placement = pos=(0,0,0) rot=(0,0,-1;1.0472rad)
  Source = -> Fusion001089102007007003008017
FEATURE [Part::MultiFuse] Fusion001089102007007003008024
  Shapes = -> [Fusion001089102007007003008017,Fusion001089102007007003008020,Fusion001089102007007003008021,Fusion001089102007007003008022,Fusion001089102007007003008018,Fusion001089102007007003008023]
FEATURE [Part::Box] Box005  label="Krychle005"
  AttacherType = Attacher::AttachEngine3D
  Height = 16
  Length = 10
  Placement = pos=(43,-22,-8) rot=(0,0,1;0rad)
  Width = 44
FEATURE [Part::Prism] prism006  label="M4X004"
  AttacherType = Attacher::AttachEngine3D
  Circumradius = 4.21
  FirstAngle = 0
  Height = 3.4
  Placement = pos=(0,0,0) rot=(0,0,1;1.5708rad)
  Polygon = 6
  SecondAngle = 0
FEATURE [Part::Box] Box006  label="Krychle006"
  AttacherType = Attacher::AttachEngine3D
  Height = 3.4
  Length = 7
  Placement = pos=(-3.5,0,0) rot=(0,0,1;0rad)
  Width = 10
FEATURE [Part::Cylinder] Cylinder014005888  label="Válec798"
  Angle = 360
  AttacherType = Attacher::AttachEngine3D
  Height = 16
  Placement = pos=(0,0,-8) rot=(0,0,1;0rad)
  Radius = 2.15
FEATURE [Part::MultiFuse] Fusion001089102007007003008026  label="M4nut006"
  Placement = pos=(0,-45,0) rot=(0,0,1;0rad)
  Shapes = -> [Cylinder014005888,Box006,prism006]
FEATURE [Part::Refine] Fusion001089102007007003008027  label="M4nut007"
  Placement = pos=(0,0,0) rot=(0,0,1;1.0472rad)
  Source = -> Fusion001089102007007003008026
FEATURE [Part::Refine] Fusion001089102007007003008028  label="M4nut008"
  Placement = pos=(0,0,0) rot=(0,0,1;2.0944rad)
  Source = -> Fusion001089102007007003008026
FEATURE [Part::Refine] Fusion001089102007007003008029  label="M4nut009"
  Placement = pos=(0,0,0) rot=(0,0,1;3.14159rad)
  Source = -> Fusion001089102007007003008026
FEATURE [Part::Refine] Fusion001089102007007003008030  label="M4nut010"
  Placement = pos=(0,0,0) rot=(0,0,1;4.18879rad)
  Source = -> Fusion001089102007007003008026
FEATURE [Part::Refine] Fusion001089102007007003008031  label="M4nut011"
  Placement = pos=(0,0,0) rot=(0,0,-1;1.0472rad)
  Source = -> Fusion001089102007007003008026
FEATURE [Part::MultiFuse] Fusion001089102007007003008032
  Shapes = -> [Fusion001089102007007003008026,Fusion001089102007007003008027,Fusion001089102007007003008028,Fusion001089102007007003008029,Fusion001089102007007003008030,Fusion001089102007007003008031]
FEATURE [Part::Prism] prism007  label="M5X006"
  AttacherType = Attacher::AttachEngine3D
  Circumradius = 4.6
  FirstAngle = 0
  Height = 4.2
  Placement = pos=(0,0,0) rot=(0,1,0;1.5708rad)
  Polygon = 6
  SecondAngle = 0
FEATURE [Part::Box] Box007  label="Krychle007"
  AttacherType = Attacher::AttachEngine3D
  Height = 10
  Length = 4.1
  Placement = pos=(0,-4,0) rot=(0,0.707107,0.707107;0rad)
  Width = 8
FEATURE [Part::Cylinder] Cylinder014005889  label="Válec799"
  Angle = 360
  AttacherType = Attacher::AttachEngine3D
  Height = 14
  Placement = pos=(-4,0,0) rot=(0,1,0;1.5708rad)
  Radius = 2.65
FEATURE [Part::MultiFuse] Fusion001089102007007003008033  label="M007"
  Placement = pos=(45,15,0) rot=(0,0,1;0rad)
  Shapes = -> [prism007,Box007,Cylinder014005889]
FEATURE [Part::Box] Box008  label="Krychle008"
  AttacherType = Attacher::AttachEngine3D
  Height = 10
  Length = 4.1
  Placement = pos=(0,-4,0) rot=(0,0.707107,0.707107;0rad)
  Width = 8
FEATURE [Part::Cylinder] Cylinder014005890  label="Válec800"
  Angle = 360
  AttacherType = Attacher::AttachEngine3D
  Height = 14
  Placement = pos=(-4,0,0) rot=(0,1,0;1.5708rad)
  Radius = 2.65
FEATURE [Part::Prism] prism008  label="M5X007"
  AttacherType = Attacher::AttachEngine3D
  Circumradius = 4.6
  FirstAngle = 0
  Height = 4.2
  Placement = pos=(0,0,0) rot=(0,1,0;1.5708rad)
  Polygon = 6
  SecondAngle = 0
FEATURE [Part::MultiFuse] Fusion001089102007007003008034  label="M008"
  Placement = pos=(45,-15,0) rot=(0,0,1;0rad)
  Shapes = -> [prism008,Box008,Cylinder014005890]
FEATURE [Part::Box] Box009  label="Krychle009"
  AttacherType = Attacher::AttachEngine3D
  Height = 16
  Length = 10
  Placement = pos=(-53,-22,-8) rot=(0,0,1;0rad)
  Width = 44
FEATURE [Part::MultiFuse] Fusion001089102007007003008025
  Shapes = -> [Cylinder014005883,Box005,Box009]
FEATURE [Part::Refine] Fusion001089102007007003008033001  label="M009"
  Placement = pos=(0,0,0) rot=(0,0,1;3.14159rad)
  Source = -> Fusion001089102007007003008033
FEATURE [Part::Refine] Fusion001089102007007003008034001  label="M010"
  Placement = pos=(0,0,0) rot=(0,0,1;3.14159rad)
  Source = -> Fusion001089102007007003008034
FEATURE [Part::MultiFuse] Fusion001089102007007003008019
  Shapes = -> [Cylinder014005884,Cylinder014005885,Fusion001089102007007003008024,Fusion001089102007007003008032,Fusion001089102007007003008033,Fusion001089102007007003008034,Fusion001089102007007003008033001,Fusion001089102007007003008034001]
FEATURE [Part::Cut] Cut009003003009003003  label="OutC002"
  Base = -> Fusion001089102007007003008025
  Tool = -> Fusion001089102007007003008019
FEATURE [Part::Refine] Cut009003003009003003001  label="OutC003"
  Source = -> Cut009003003009003003
FEATURE [Part::Chamfer] Chamfer014  label="OuTCra"
  Base = -> Cut009003003009003003001
  Edges = 18 edges r=0.5: [Edge2,Edge4,Edge5,Edge7,Edge8,Edge9,Edge11,Edge12,Edge13,Edge14,Edge15,Edge16,Edge33,Edge37,Edge38,Edge185,Edge315,Edge392]
FEATURE [Part::Cylinder] Cylinder014005892  label="Válec802"
  Angle = 360
  AttacherType = Attacher::AttachEngine3D
  Height = 10
  Placement = pos=(0,44,0) rot=(1,0,0;1.5708rad)
  Radius = 50
FEATURE [Part::Cylinder] Cylinder014005895  label="Válec805"
  Angle = 360
  AttacherType = Attacher::AttachEngine3D
  Height = 10
  Placement = pos=(0,44,45.4) rot=(1,0,0;1.5708rad)
  Radius = 2.15
FEATURE [Part::Refine] Cylinder014005891  label="Válec801"
  Placement = pos=(0,0,0) rot=(0,-1,0;1.0472rad)
  Source = -> Cylinder014005895
FEATURE [Part::Refine] Cylinder014005893  label="Válec803"
  Placement = pos=(0,0,0) rot=(0,1,0;2.0944rad)
  Source = -> Cylinder014005895
FEATURE [Part::Refine] Cylinder014005894  label="Válec804"
  Placement = pos=(0,0,0) rot=(0,1,0;4.18879rad)
  Source = -> Cylinder014005895
FEATURE [Part::FeaturePython] cycloidgear008  # WARN: FeaturePython — macro-defined, semantics opaque (R4)
  AttacherType = Attacher::AttachEngine3D
  Placement = pos=(0,44,0) rot=(1,0,0;1.5708rad)
  backlash = 0
  beta = 0
  clearance = 0.25
  double_helix = false
  head = 0
  height = 10
  inner_diameter = 5
  module = 0.792
  numpoints = 15
  outer_diameter = 5
  teeth = 102
  version = 0.0.3
FEATURE [Part::Chamfer] Chamfer015
  Base = -> Cylinder014005892
  Edges = 2 edges r=1: [Edge1,Edge3]
FEATURE [Part::Refine] Cylinder014005896  label="Válec806"
  Placement = pos=(0,0,0) rot=(0,1,0;1.0472rad)
  Source = -> Cylinder014005895
FEATURE [Part::Refine] Cylinder014005897  label="Válec807"
  Placement = pos=(0,0,0) rot=(0,1,0;3.14159rad)
  Source = -> Cylinder014005895
FEATURE [Part::MultiFuse] Fusion001089102007007003008034002
  Shapes = -> [cycloidgear008,Cylinder014005895,Cylinder014005896,Cylinder014005893,Cylinder014005897,Cylinder014005894,Cylinder014005891]
FEATURE [Part::Cut] Cut009003003009003003002  label="CIRCULAR_102"
  Base = -> Chamfer015
  Placement = pos=(0,0,0) rot=(1,0,0;1.5708rad)
  Tool = -> Fusion001089102007007003008034002
FEATURE [Part::Refine] Part__Feature001001  label="WAVE_BEARING_CAP001"
  Placement = pos=(0,0,14) rot=(0,0,1;1.5708rad)
  Source = -> Part__Feature001
FEATURE [Part::Prism] Prism  label="Hranol"
  AttacherType = Attacher::AttachEngine3D
  Circumradius = 3.2
  FirstAngle = 0
  Height = 2.5
  Placement = pos=(0,27.9,0) rot=(0,0,1;0rad)
  Polygon = 6
  SecondAngle = 0
FEATURE [Part::Prism] Prism001  label="Hranol001"
  AttacherType = Attacher::AttachEngine3D
  Circumradius = 3.2
  FirstAngle = 0
  Height = 2.5
  Placement = pos=(0,-27.9,0) rot=(0,0,1;0rad)
  Polygon = 6
  SecondAngle = 0
FEATURE [Part::MultiFuse] Fusion001089092
  Placement = pos=(0,0,0) rot=(0,0,1;0.698132rad)
  Shapes = -> [Prism,Prism001]
FEATURE [Part::Prism] Prism002  label="Hranol002"
  AttacherType = Attacher::AttachEngine3D
  Circumradius = 3.2
  FirstAngle = 0
  Height = 2.5
  Placement = pos=(0,27.9,0) rot=(0,0,1;0rad)
  Polygon = 6
  SecondAngle = 0
FEATURE [Part::Prism] Prism003  label="Hranol003"
  AttacherType = Attacher::AttachEngine3D
  Circumradius = 3.2
  FirstAngle = 0
  Height = 2.5
  Placement = pos=(0,-27.9,0) rot=(0,0,1;0rad)
  Polygon = 6
  SecondAngle = 0
FEATURE [Part::MultiFuse] Fusion001089091
  Placement = pos=(0,0,0) rot=(0,0,-1;0.698132rad)
  Shapes = -> [Prism002,Prism003]
FEATURE [Part::Prism] Prism004  label="Hranol004"
  AttacherType = Attacher::AttachEngine3D
  Circumradius = 3.2
  FirstAngle = 0
  Height = 2.5
  Placement = pos=(0,28.5,0) rot=(0,0,1;0rad)
  Polygon = 6
  SecondAngle = 0
FEATURE [Part::Prism] Prism005  label="Hranol005"
  AttacherType = Attacher::AttachEngine3D
  Circumradius = 3.2
  FirstAngle = 0
  Height = 2.5
  Placement = pos=(0,-28.5,0) rot=(0,0,1;0rad)
  Polygon = 6
  SecondAngle = 0
FEATURE [Part::MultiFuse] Fusion001089090
  Shapes = -> [Cylinder014005848,Cylinder014005849,Prism004,Prism005]
FEATURE [Part::Box] Box010  label="Krychle010"
  AttacherType = Attacher::AttachEngine3D
  Height = 14
  Length = 22
  Placement = pos=(-11,-11,0) rot=(0,0,1;0rad)
  Width = 22
FEATURE [Part::MultiFuse] Fusion001089102007007003008034003
  Shapes = -> [Part__Feature053,Box010]
FEATURE [Part::Prism] Prism006  label="Hranol006"
  AttacherType = Attacher::AttachEngine3D
  Circumradius = 4.6
  FirstAngle = 0
  Height = 3.8
  Placement = pos=(0,0,9) rot=(0,1,0;1.5708rad)
  Polygon = 6
  SecondAngle = 0
FEATURE [Part::Box] Box011  label="Krychle011"
  AttacherType = Attacher::AttachEngine3D
  Height = 10
  Length = 3.8
  Placement = pos=(0,-3.95,9) rot=(0,0,1;0rad)
  Width = 7.9
FEATURE [Part::MultiFuse] Fusion001089102007007003008034004
  Placement = pos=(6,0,0) rot=(0,0,1;0rad)
  Shapes = -> [Prism006,Box011]
FEATURE [Part::Box] Box012  label="Krychle012"
  AttacherType = Attacher::AttachEngine3D
  Height = 10
  Length = 3.8
  Placement = pos=(0,-3.95,9) rot=(0,0,1;0rad)
  Width = 7.9
FEATURE [Part::Prism] Prism007  label="Hranol007"
  AttacherType = Attacher::AttachEngine3D
  Circumradius = 4.6
  FirstAngle = 0
  Height = 3.8
  Placement = pos=(0,0,9) rot=(0,1,0;1.5708rad)
  Polygon = 6
  SecondAngle = 0
FEATURE [Part::MultiFuse] Fusion001089102007007003008034005
  Placement = pos=(-9.8,0,0) rot=(0,0,1;0rad)
  Shapes = -> [Prism007,Box012]
FEATURE [Part::MultiFuse] Fusion001089093
  Shapes = -> [Cylinder014005847,Fusion001089090,Fusion001089091,Fusion001089092,Cylinder014005854,Fusion001089102007007003008034004,Fusion001089102007007003008034005]
FEATURE [Part::Cut] Cut009003003009003003003  label="WAWE"
  Base = -> Fusion001089102007007003008034003
  Tool = -> Fusion001089093
FEATURE [Part::Cylinder] Cylinder014005898  label="Válec808"
  Angle = 360
  AttacherType = Attacher::AttachEngine3D
  Height = 14
  Placement = pos=(0,0,10) rot=(0,0,1;0rad)
  Radius = 4
FEATURE [Part::Refine] Cut009003003009003003003001  label="WaveGenA"
  Source = -> Cut009003003009003003003
FEATURE [Part::Cut] Cut009003003009003003003002  label="WaveGenB"
  Base = -> Part__Feature001001
  Tool = -> Cylinder014005898
FEATURE [Part::FeaturePython] Tube005  # WARN: FeaturePython — macro-defined, semantics opaque (R4)
  AttacherType = Attacher::AttachEngine3D
  Height = 4.5
  InnerRadius = 4.2
  OuterRadius = 8
FEATURE [Part::Cylinder] Cylinder014005899  label="Válec809"
  Angle = 360
  AttacherType = Attacher::AttachEngine3D
  Height = 1
  Radius = 7
FEATURE [Part::Cut] Cut009003003009003003003003  label="ring001"
  Base = -> Tube005
  Tool = -> Cylinder014005899
FEATURE [Part::Cylinder] Cylinder014005900  label="Válec810"
  Angle = 360
  AttacherType = Attacher::AttachEngine3D
  Height = 22.5
  Placement = pos=(0,0,-8) rot=(0,0,1;0rad)
  Radius = 53
FEATURE [Part::Cylinder] Cylinder014005901  label="Válec811"
  Angle = 360
  AttacherType = Attacher::AttachEngine3D
  Height = 22.5
  Placement = pos=(0,0,-8) rot=(0,0,1;0rad)
  Radius = 18.5
FEATURE [Part::Cylinder] Cylinder014005902  label="Válec812"
  Angle = 360
  AttacherType = Attacher::AttachEngine3D
  Height = 22.5
  Placement = pos=(0,0,-5) rot=(0,0,1;0rad)
  Radius = 39
FEATURE [Part::Cylinder] Cylinder014005903  label="Válec813"
  Angle = 360
  AttacherType = Attacher::AttachEngine3D
  Height = 14
  Placement = pos=(45,0,-8) rot=(0,0,1;0rad)
  Radius = 2.15
FEATURE [Part::Cylinder] Cylinder014005904  label="Válec814"
  Angle = 360
  AttacherType = Attacher::AttachEngine3D
  Height = 10.5
  Placement = pos=(45,0,4) rot=(0,0,1;0rad)
  Radius = 3.65
FEATURE [Part::MultiFuse] Fusion001089102007007003008034008  label="inbusL020"
  Shapes = -> [Cylinder014005903,Cylinder014005904]
FEATURE [Part::Refine] Fusion001089102007007003008034006  label="inbusL019"
  Placement = pos=(0,0,0) rot=(0,0,-1;1.0472rad)
  Source = -> Fusion001089102007007003008034008
FEATURE [Part::Refine] Fusion001089102007007003008034009  label="inbusL021"
  Placement = pos=(0,0,0) rot=(0,0,1;1.0472rad)
  Source = -> Fusion001089102007007003008034008
FEATURE [Part::Refine] Fusion001089102007007003008034010  label="inbusL022"
  Placement = pos=(0,0,0) rot=(0,0,1;2.0944rad)
  Source = -> Fusion001089102007007003008034008
FEATURE [Part::Refine] Fusion001089102007007003008034011  label="inbusL023"
  Placement = pos=(0,0,0) rot=(0,0,1;3.14159rad)
  Source = -> Fusion001089102007007003008034008
FEATURE [Part::Refine] Fusion001089102007007003008034012  label="inbusL024"
  Placement = pos=(0,0,0) rot=(0,0,1;4.18879rad)
  Source = -> Fusion001089102007007003008034008
FEATURE [Part::MultiFuse] Fusion001089102007007003008034013  label="m4INBUS"
  Shapes = -> [Fusion001089102007007003008034008,Fusion001089102007007003008034009,Fusion001089102007007003008034010,Fusion001089102007007003008034011,Fusion001089102007007003008034012,Fusion001089102007007003008034006]
FEATURE [Part::Box] Box013  label="Krychle013"
  AttacherType = Attacher::AttachEngine3D
  Height = 16
  Length = 10
  Placement = pos=(43,-22,-8) rot=(0,0,1;0rad)
  Width = 44
FEATURE [Part::MultiFuse] Fusion001089102007007003008034014
  Shapes = -> [Cylinder014005900,Box013]
FEATURE [Part::Prism] prism009  label="M4X005"
  AttacherType = Attacher::AttachEngine3D
  Circumradius = 4.6
  FirstAngle = 0
  Height = 4.2
  Placement = pos=(0,0,7) rot=(0,0,1;1.5708rad)
  Polygon = 6
  SecondAngle = 0
FEATURE [Part::Box] Box014  label="Krychle014"
  AttacherType = Attacher::AttachEngine3D
  Height = 4.1
  Length = 8
  Placement = pos=(-3.5,0,7) rot=(0,0,1;0rad)
  Width = 10
FEATURE [Part::Cylinder] Cylinder014005905  label="Válec815"
  Angle = 360
  AttacherType = Attacher::AttachEngine3D
  Height = 22.5
  Placement = pos=(0,0,-8) rot=(0,0,1;0rad)
  Radius = 2.65
FEATURE [Part::Prism] prism010  label="M5X008"
  AttacherType = Attacher::AttachEngine3D
  Circumradius = 4.6
  FirstAngle = 0
  Height = 4.2
  Placement = pos=(0,0,0) rot=(0,1,0;1.5708rad)
  Polygon = 6
  SecondAngle = 0
FEATURE [Part::Box] Box015  label="Krychle015"
  AttacherType = Attacher::AttachEngine3D
  Height = 10
  Length = 4.1
  Placement = pos=(0,-4,0) rot=(0,0.707107,0.707107;0rad)
  Width = 8
FEATURE [Part::Cylinder] Cylinder014005906  label="Válec816"
  Angle = 360
  AttacherType = Attacher::AttachEngine3D
  Height = 14
  Placement = pos=(-4,0,0) rot=(0,1,0;1.5708rad)
  Radius = 2.65
FEATURE [Part::MultiFuse] Fusion001089102007007003008034022  label="M011"
  Placement = pos=(45,15,0) rot=(1,0,0;3.14159rad)
  Shapes = -> [prism010,Box015,Cylinder014005906]
FEATURE [Part::Box] Box016  label="Krychle016"
  AttacherType = Attacher::AttachEngine3D
  Height = 10
  Length = 4.1
  Placement = pos=(0,-4,0) rot=(0,0.707107,0.707107;0rad)
  Width = 8
FEATURE [Part::Cylinder] Cylinder014005907  label="Válec817"
  Angle = 360
  AttacherType = Attacher::AttachEngine3D
  Height = 14
  Placement = pos=(-4,0,0) rot=(0,1,0;1.5708rad)
  Radius = 2.65
FEATURE [Part::Prism] prism011  label="M5X009"
  AttacherType = Attacher::AttachEngine3D
  Circumradius = 4.6
  FirstAngle = 0
  Height = 4.2
  Placement = pos=(0,0,0) rot=(0,1,0;1.5708rad)
  Polygon = 6
  SecondAngle = 0
FEATURE [Part::MultiFuse] Fusion001089102007007003008034023  label="M012"
  Placement = pos=(45,-15,0) rot=(1,0,0;3.14159rad)
  Shapes = -> [prism011,Box016,Cylinder014005907]
FEATURE [Part::Cylinder] Cylinder014005908  label="Válec818"
  Angle = 360
  AttacherType = Attacher::AttachEngine3D
  Height = 10
  Placement = pos=(-9.9,9.9,0) rot=(0,0,1;0rad)
  Radius = 1.6
FEATURE [Part::Cylinder] Cylinder014005909  label="Válec819"
  Angle = 360
  AttacherType = Attacher::AttachEngine3D
  Height = 10
  Placement = pos=(-9.9,-9.9,0) rot=(0,0,1;0rad)
  Radius = 1.6
FEATURE [Part::Cylinder] Cylinder014005910  label="Válec820"
  Angle = 360
  AttacherType = Attacher::AttachEngine3D
  Height = 10
  Placement = pos=(9.9,-9.9,0) rot=(0,0,1;0rad)
  Radius = 1.6
FEATURE [Part::Cylinder] Cylinder014005911  label="Válec821"
  Angle = 360
  AttacherType = Attacher::AttachEngine3D
  Height = 10
  Placement = pos=(9.9,9.9,0) rot=(0,0,1;0rad)
  Radius = 1.6
FEATURE [Part::MultiFuse] Fusion001089102007007003008034024  label="Diry PG002"
  Shapes = -> [Cylinder014005908,Cylinder014005911,Cylinder014005909,Cylinder014005910]
FEATURE [Part::Cylinder] Cylinder014005912  label="Válec822"
  Angle = 360
  AttacherType = Attacher::AttachEngine3D
  Height = 3
  Placement = pos=(9.9,9.9,0) rot=(0,0,1;0rad)
  Radius = 2.8
FEATURE [Part::Cylinder] Cylinder014005913  label="Válec823"
  Angle = 360
  AttacherType = Attacher::AttachEngine3D
  Height = 3
  Placement = pos=(9.9,-9.9,0) rot=(0,0,1;0rad)
  Radius = 2.8
FEATURE [Part::Cylinder] Cylinder014005914  label="Válec824"
  Angle = 360
  AttacherType = Attacher::AttachEngine3D
  Height = 3
  Placement = pos=(-9.9,-9.9,0) rot=(0,0,1;0rad)
  Radius = 2.8
FEATURE [Part::Cylinder] Cylinder014005915  label="Válec825"
  Angle = 360
  AttacherType = Attacher::AttachEngine3D
  Height = 3
  Placement = pos=(-9.9,9.9,0) rot=(0,0,1;0rad)
  Radius = 2.8
FEATURE [Part::MultiFuse] Fusion001089102007007003008034026  label="Diry PG003"
  Shapes = -> [Cylinder014005915,Cylinder014005912,Cylinder014005914,Cylinder014005913]
FEATURE [Part::MultiFuse] Fusion001089102007007003008034025  label="GeerPG001"
  Placement = pos=(0,47,0) rot=(-1,0,0;1.5708rad)
  Shapes = -> [Fusion001089102007007003008034024,Fusion001089102007007003008034026]
FEATURE [Part::Feature] Part__Feature001002  label="MOTOR_CAP002"
  Placement = pos=(0,0,0) rot=(0,1,0;0.523599rad)
  shape: bbox 106 x 12.2 x 106 mm, 94 faces (baked)
FEATURE [Part::Cut] Cut009003003009003003003006  label="MotorPG001"
  Base = -> Part__Feature001002
  Placement = pos=(0,0,-8) rot=(-1,0,0;1.5708rad)
  Tool = -> Fusion001089102007007003008034025
FEATURE [Part::Feature] Cut005_solid002  label="Planetary Gear Box distance  RA002"
  Placement = pos=(0,0,-8) rot=(0,0,1;0rad)
  shape: bbox 41 x 41 x 22.5 mm, 15 faces (baked)
FEATURE [Part::Cylinder] Cylinder014005916  label="Válec826"
  Angle = 360
  AttacherType = Attacher::AttachEngine3D
  Height = 10
  Placement = pos=(0,0,-8) rot=(0,0,1;0rad)
  Radius = 3.65
FEATURE [Part::MultiFuse] Fusion001089102007007003008034015  label="M4nut012"
  Placement = pos=(0,-45,0) rot=(0,0,1;0rad)
  Shapes = -> [Cylinder014005905,Box014,prism009,Cylinder014005916]
FEATURE [Part::Refine] Fusion001089102007007003008034016  label="M4nut013"
  Placement = pos=(0,0,0) rot=(0,0,1;1.0472rad)
  Source = -> Fusion001089102007007003008034015
FEATURE [Part::Refine] Fusion001089102007007003008034017  label="M4nut014"
  Placement = pos=(0,0,0) rot=(0,0,1;2.0944rad)
  Source = -> Fusion001089102007007003008034015
FEATURE [Part::Refine] Fusion001089102007007003008034018  label="M4nut015"
  Placement = pos=(0,0,0) rot=(0,0,1;3.14159rad)
  Source = -> Fusion001089102007007003008034015
FEATURE [Part::Refine] Fusion001089102007007003008034019  label="M4nut016"
  Placement = pos=(0,0,0) rot=(0,0,1;4.18879rad)
  Source = -> Fusion001089102007007003008034015
FEATURE [Part::Refine] Fusion001089102007007003008034020  label="M4nut017"
  Placement = pos=(0,0,0) rot=(0,0,-1;1.0472rad)
  Source = -> Fusion001089102007007003008034015
FEATURE [Part::Cylinder] Cylinder014005917  label="Válec827"
  Angle = 360
  AttacherType = Attacher::AttachEngine3D
  Height = 22.5
  Placement = pos=(0,0,-8) rot=(0,0,1;0rad)
  Radius = 1.65
FEATURE [Part::Prism] Prism008  label="Hranol008"
  AttacherType = Attacher::AttachEngine3D
  Circumradius = 3.2
  FirstAngle = 0
  Height = 2.5
  Polygon = 6
  SecondAngle = 0
FEATURE [Part::Box] Box017  label="Krychle017"
  AttacherType = Attacher::AttachEngine3D
  Height = 2.5
  Length = 8
  Placement = pos=(0,-2.75,0) rot=(0,0,1;0rad)
  Width = 5.5
FEATURE [Part::MultiFuse] Fusion001089102007007003008034028
  Placement = pos=(15.5,15.5,0) rot=(0,0,1;0.785398rad)
  Shapes = -> [Box017,Cylinder014005917,Prism008]
FEATURE [Part::Refine] Fusion001089102007007003008034028001
  Placement = pos=(0,0,0) rot=(0,0,1;1.5708rad)
  Source = -> Fusion001089102007007003008034028
FEATURE [Part::Refine] Fusion001089102007007003008034028002
  Placement = pos=(0,0,0) rot=(0,0,1;3.14159rad)
  Source = -> Fusion001089102007007003008034028
FEATURE [Part::Refine] Fusion001089102007007003008034028003
  Placement = pos=(0,0,0) rot=(0,0,-1;1.5708rad)
  Source = -> Fusion001089102007007003008034028
FEATURE [Part::MultiFuse] Fusion001089102007007003008034028004  label="M3i"
  Shapes = -> [Fusion001089102007007003008034028,Fusion001089102007007003008034028001,Fusion001089102007007003008034028002,Fusion001089102007007003008034028003]
FEATURE [Part::Cylinder] Cylinder014005918  label="Válec828"
  Angle = 360
  AttacherType = Attacher::AttachEngine3D
  Height = 22.5
  Placement = pos=(0,0,-8) rot=(0,0,1;0rad)
  Radius = 18.5
FEATURE [Part::Cylinder] Cylinder014005919  label="Válec829"
  Angle = 360
  AttacherType = Attacher::AttachEngine3D
  Height = 22.5
  Placement = pos=(0,0,-5) rot=(0,0,1;0rad)
  Radius = 39
FEATURE [Part::Cylinder] Cylinder014005920  label="Válec830"
  Angle = 360
  AttacherType = Attacher::AttachEngine3D
  Height = 14
  Placement = pos=(45,0,-8) rot=(0,0,1;0rad)
  Radius = 2.15
FEATURE [Part::Cylinder] Cylinder014005921  label="Válec831"
  Angle = 360
  AttacherType = Attacher::AttachEngine3D
  Height = 10.5
  Placement = pos=(45,0,4) rot=(0,0,1;0rad)
  Radius = 3.65
FEATURE [Part::Prism] prism012  label="M4X006"
  AttacherType = Attacher::AttachEngine3D
  Circumradius = 4.6
  FirstAngle = 0
  Height = 4.2
  Placement = pos=(0,0,7) rot=(0,0,1;1.5708rad)
  Polygon = 6
  SecondAngle = 0
FEATURE [Part::Box] Box018  label="Krychle018"
  AttacherType = Attacher::AttachEngine3D
  Height = 4.1
  Length = 8
  Placement = pos=(-3.5,0,7) rot=(0,0,1;0rad)
  Width = 10
FEATURE [Part::Cylinder] Cylinder014005922  label="Válec832"
  Angle = 360
  AttacherType = Attacher::AttachEngine3D
  Height = 22.5
  Placement = pos=(0,0,-8) rot=(0,0,1;0rad)
  Radius = 2.65
FEATURE [Part::Feature] Cut005_solid003  label="Planetary Gear Box distance  RA003"
  Placement = pos=(0,0,-8) rot=(0,0,1;0rad)
  shape: bbox 41 x 41 x 22.5 mm, 15 faces (baked)
FEATURE [Part::Prism] prism013  label="M5X010"
  AttacherType = Attacher::AttachEngine3D
  Circumradius = 4.6
  FirstAngle = 0
  Height = 4.2
  Placement = pos=(0,0,0) rot=(0,1,0;1.5708rad)
  Polygon = 6
  SecondAngle = 0
FEATURE [Part::Box] Box019  label="Krychle019"
  AttacherType = Attacher::AttachEngine3D
  Height = 10
  Length = 4.1
  Placement = pos=(0,-4,0) rot=(0,0.707107,0.707107;0rad)
  Width = 8
FEATURE [Part::Cylinder] Cylinder014005923  label="Válec833"
  Angle = 360
  AttacherType = Attacher::AttachEngine3D
  Height = 22.5
  Placement = pos=(0,0,-8) rot=(0,0,1;0rad)
  Radius = 53
FEATURE [Part::Cylinder] Cylinder014005924  label="Válec834"
  Angle = 360
  AttacherType = Attacher::AttachEngine3D
  Height = 14
  Placement = pos=(-4,0,0) rot=(0,1,0;1.5708rad)
  Radius = 2.65
FEATURE [Part::MultiFuse] Fusion001089102007007003008034028015  label="M013"
  Placement = pos=(45,15,0) rot=(1,0,0;3.14159rad)
  Shapes = -> [prism013,Box019,Cylinder014005924]
FEATURE [Part::Box] Box020  label="Krychle020"
  AttacherType = Attacher::AttachEngine3D
  Height = 10
  Length = 4.1
  Placement = pos=(0,-4,0) rot=(0,0.707107,0.707107;0rad)
  Width = 8
FEATURE [Part::Cylinder] Cylinder014005925  label="Válec835"
  Angle = 360
  AttacherType = Attacher::AttachEngine3D
  Height = 14
  Placement = pos=(-4,0,0) rot=(0,1,0;1.5708rad)
  Radius = 2.65
FEATURE [Part::Prism] prism014  label="M5X011"
  AttacherType = Attacher::AttachEngine3D
  Circumradius = 4.6
  FirstAngle = 0
  Height = 4.2
  Placement = pos=(0,0,0) rot=(0,1,0;1.5708rad)
  Polygon = 6
  SecondAngle = 0
FEATURE [Part::MultiFuse] Fusion001089102007007003008034028016  label="M014"
  Placement = pos=(45,-15,0) rot=(1,0,0;3.14159rad)
  Shapes = -> [prism014,Box020,Cylinder014005925]
FEATURE [Part::MultiFuse] Fusion001089102007007003008034028017  label="inbusL026"
  Shapes = -> [Cylinder014005920,Cylinder014005921]
FEATURE [Part::Refine] Fusion001089102007007003008034028006  label="inbusL025"
  Placement = pos=(0,0,0) rot=(0,0,-1;1.0472rad)
  Source = -> Fusion001089102007007003008034028017
FEATURE [Part::Refine] Fusion001089102007007003008034028018  label="inbusL027"
  Placement = pos=(0,0,0) rot=(0,0,1;1.0472rad)
  Source = -> Fusion001089102007007003008034028017
FEATURE [Part::Refine] Fusion001089102007007003008034028019  label="inbusL028"
  Placement = pos=(0,0,0) rot=(0,0,1;2.0944rad)
  Source = -> Fusion001089102007007003008034028017
FEATURE [Part::Refine] Fusion001089102007007003008034028020  label="inbusL029"
  Placement = pos=(0,0,0) rot=(0,0,1;3.14159rad)
  Source = -> Fusion001089102007007003008034028017
FEATURE [Part::Refine] Fusion001089102007007003008034028021  label="inbusL030"
  Placement = pos=(0,0,0) rot=(0,0,1;4.18879rad)
  Source = -> Fusion001089102007007003008034028017
FEATURE [Part::MultiFuse] Fusion001089102007007003008034028022  label="m4INBUS001"
  Shapes = -> [Fusion001089102007007003008034028017,Fusion001089102007007003008034028018,Fusion001089102007007003008034028019,Fusion001089102007007003008034028020,Fusion001089102007007003008034028021,Fusion001089102007007003008034028006]
FEATURE [Part::Box] Box021  label="Krychle021"
  AttacherType = Attacher::AttachEngine3D
  Height = 16
  Length = 10
  Placement = pos=(43,-22,-8) rot=(0,0,1;0rad)
  Width = 44
FEATURE [Part::Box] Box022  label="Krychle022"
  AttacherType = Attacher::AttachEngine3D
  Height = 2.5
  Length = 8
  Placement = pos=(0,-2.75,0) rot=(0,0,1;0rad)
  Width = 5.5
FEATURE [Part::Prism] Prism009  label="Hranol009"
  AttacherType = Attacher::AttachEngine3D
  Circumradius = 3.2
  FirstAngle = 0
  Height = 2.5
  Polygon = 6
  SecondAngle = 0
FEATURE [Part::Cylinder] Cylinder014005926  label="Válec836"
  Angle = 360
  AttacherType = Attacher::AttachEngine3D
  Height = 10
  Placement = pos=(0,0,-8) rot=(0,0,1;0rad)
  Radius = 3.65
FEATURE [Part::MultiFuse] Fusion001089102007007003008034028009  label="M4nut018"
  Placement = pos=(0,-45,0) rot=(0,0,1;0rad)
  Shapes = -> [Cylinder014005922,Box018,prism012,Cylinder014005926]
FEATURE [Part::Refine] Fusion001089102007007003008034028010  label="M4nut019"
  Placement = pos=(0,0,0) rot=(0,0,1;1.0472rad)
  Source = -> Fusion001089102007007003008034028009
FEATURE [Part::Refine] Fusion001089102007007003008034028011  label="M4nut020"
  Placement = pos=(0,0,0) rot=(0,0,1;3.14159rad)
  Source = -> Fusion001089102007007003008034028009
FEATURE [Part::Refine] Fusion001089102007007003008034028012  label="M4nut021"
  Placement = pos=(0,0,0) rot=(0,0,1;4.18879rad)
  Source = -> Fusion001089102007007003008034028009
FEATURE [Part::Refine] Fusion001089102007007003008034028013  label="M4nut022"
  Placement = pos=(0,0,0) rot=(0,0,-1;1.0472rad)
  Source = -> Fusion001089102007007003008034028009
FEATURE [Part::Cylinder] Cylinder014005927  label="Válec837"
  Angle = 360
  AttacherType = Attacher::AttachEngine3D
  Height = 22.5
  Placement = pos=(0,0,-8) rot=(0,0,1;0rad)
  Radius = 1.65
FEATURE [Part::MultiFuse] Fusion001089102007007003008034028027
  Placement = pos=(15.5,15.5,0) rot=(0,0,1;0.785398rad)
  Shapes = -> [Box022,Cylinder014005927,Prism009]
FEATURE [Part::Refine] Fusion001089102007007003008034028023
  Placement = pos=(0,0,0) rot=(0,0,1;1.5708rad)
  Source = -> Fusion001089102007007003008034028027
FEATURE [Part::Refine] Fusion001089102007007003008034028025
  Placement = pos=(0,0,0) rot=(0,0,-1;1.5708rad)
  Source = -> Fusion001089102007007003008034028027
FEATURE [Part::Refine] Fusion001089102007007003008034028026
  Placement = pos=(0,0,0) rot=(0,0,1;3.14159rad)
  Source = -> Fusion001089102007007003008034028027
FEATURE [Part::MultiFuse] Fusion001089102007007003008034028005  label="M3i001"
  Shapes = -> [Fusion001089102007007003008034028027,Fusion001089102007007003008034028023,Fusion001089102007007003008034028026,Fusion001089102007007003008034028025]
FEATURE [Part::Refine] Box021001  label="Krychle023"
  Placement = pos=(0,0,0) rot=(0,0,1;3.14159rad)
  Source = -> Box021
FEATURE [Part::MultiFuse] Fusion001089102007007003008034028008
  Shapes = -> [Cylinder014005923,Box021,Box021001]
FEATURE [Part::Refine] Fusion001089102007007003008034028015001  label="M015"
  Placement = pos=(0,0,0) rot=(0,0,1;3.14159rad)
  Source = -> Fusion001089102007007003008034028015
FEATURE [Part::Refine] Fusion001089102007007003008034028016001  label="M016"
  Placement = pos=(0,0,0) rot=(0,0,1;3.14159rad)
  Source = -> Fusion001089102007007003008034028016
FEATURE [Part::Refine] Fusion001089102007007003008034028009001  label="M4nut023"
  Placement = pos=(0,0,0) rot=(0,0,1;2.0944rad)
  Source = -> Fusion001089102007007003008034028009
FEATURE [Part::MultiFuse] Fusion001089102007007003008034028014
  Shapes = -> [Fusion001089102007007003008034028009,Fusion001089102007007003008034028010,Fusion001089102007007003008034028011,Fusion001089102007007003008034028012,Fusion001089102007007003008034028013,Fusion001089102007007003008034028009001]
FEATURE [Part::MultiFuse] Fusion001089102007007003008034028007
  Shapes = -> [Cylinder014005918,Cylinder014005919,Fusion001089102007007003008034028022,Fusion001089102007007003008034028014,Fusion001089102007007003008034028015,Fusion001089102007007003008034028016,Fusion001089102007007003008034028015001,Fusion001089102007007003008034028016001]
FEATURE [Part::Cut] Cut009003003009003003003007002  label="OutC005"
  Base = -> Fusion001089102007007003008034028008
  Tool = -> Fusion001089102007007003008034028007
FEATURE [Part::MultiFuse] Fusion001089102007007003008034028024  label="MotorDa001"
  Shapes = -> [Cut005_solid003,Cut009003003009003003003007002]
FEATURE [Part::Cut] Cut009003003009003003003007003  label="MotorOra02"
  Base = -> Fusion001089102007007003008034028024
  Tool = -> Fusion001089102007007003008034028005
FEATURE [Part::Refine] Cut009003003009003003003007003001  label="MotorOra003"
  Source = -> Cut009003003009003003003007003
FEATURE [Part::Refine] Fusion001089102007007003008034015001  label="M4nut024"
  Placement = pos=(0,0,0) rot=(0,0,1;2.0944rad)
  Source = -> Fusion001089102007007003008034015
FEATURE [Part::MultiFuse] Fusion001089102007007003008034021
  Shapes = -> [Fusion001089102007007003008034015,Fusion001089102007007003008034016,Fusion001089102007007003008034018,Fusion001089102007007003008034019,Fusion001089102007007003008034020,Fusion001089102007007003008034015001]
FEATURE [Part::MultiFuse] Fusion001089102007007003008034007
  Shapes = -> [Cylinder014005901,Cylinder014005902,Fusion001089102007007003008034013,Fusion001089102007007003008034021,Fusion001089102007007003008034022,Fusion001089102007007003008034023]
FEATURE [Part::Cut] Cut009003003009003003003004  label="OutC004"
  Base = -> Fusion001089102007007003008034014
  Tool = -> Fusion001089102007007003008034007
FEATURE [Part::MultiFuse] Fusion001089102007007003008034027  label="MotorDa"
  Shapes = -> [Cut005_solid002,Cut009003003009003003003004]
FEATURE [Part::Cut] Cut009003003009003003003007  label="MotorOde"
  Base = -> Fusion001089102007007003008034027
  Tool = -> Fusion001089102007007003008034028004
FEATURE [Part::Refine] Cut009003003009003003003007001  label="MotorOde001"
  Source = -> Cut009003003009003003003007
FEATURE [Part::Fillet] Fillet  label="MotorDe"
  Base = -> Cut009003003009003003003007001
  Edges = 8 edges r=0.75: [Edge87,Edge167,Edge314,Edge429,Edge430,Edge431,Edge432,Edge483]
FEATURE [Part::Box] Box021002  label="Krychle024"
  AttacherType = Attacher::AttachEngine3D
  Height = 84
  Length = 10
  Placement = pos=(0,-22,0) rot=(0,0,1;0rad)
  Width = 44
FEATURE [Part::Cylinder] Cylinder014005928  label="Válec838"
  Angle = 360
  AttacherType = Attacher::AttachEngine3D
  Height = 10
  Placement = pos=(0,0,42) rot=(0,1,0;1.5708rad)
  Radius = 35
FEATURE [Part::MultiFuse] Fusion001089102007007003008034028016002
  Shapes = -> [Cylinder014005928,Box021002]
FEATURE [Part::Cylinder] Cylinder014005931  label="Válec841"
  Angle = 360
  AttacherType = Attacher::AttachEngine3D
  Height = 10
  Placement = pos=(0,-15,7.5) rot=(0,1,0;1.5708rad)
  Radius = 2.65
FEATURE [Part::Cylinder] Cylinder014005932  label="Válec842"
  Angle = 360
  AttacherType = Attacher::AttachEngine3D
  Height = 10
  Placement = pos=(0,15,7.5) rot=(0,1,0;1.5708rad)
  Radius = 2.65
FEATURE [Part::Cylinder] Cylinder014005933  label="Válec843"
  Angle = 360
  AttacherType = Attacher::AttachEngine3D
  Height = 10
  Placement = pos=(0,-15,75.5) rot=(0,1,0;1.5708rad)
  Radius = 2.65
FEATURE [Part::Cylinder] Cylinder014005934  label="Válec844"
  Angle = 360
  AttacherType = Attacher::AttachEngine3D
  Height = 10
  Placement = pos=(0,15,75.5) rot=(0,1,0;1.5708rad)
  Radius = 2.65
FEATURE [Part::Cylinder] Cylinder014005935  label="Válec845"
  Angle = 360
  AttacherType = Attacher::AttachEngine3D
  Height = 4.2
  Placement = pos=(0,-15,7.5) rot=(0,1,0;1.5708rad)
  Radius = 4.3
FEATURE [Part::Cylinder] Cylinder014005936  label="Válec846"
  Angle = 360
  AttacherType = Attacher::AttachEngine3D
  Height = 4.2
  Placement = pos=(0,15,7.5) rot=(0,1,0;1.5708rad)
  Radius = 4.3
FEATURE [Part::Cylinder] Cylinder014005937  label="Válec847"
  Angle = 360
  AttacherType = Attacher::AttachEngine3D
  Height = 4.2
  Placement = pos=(0,-15,75.5) rot=(0,1,0;1.5708rad)
  Radius = 4.3
FEATURE [Part::Cylinder] Cylinder014005938  label="Válec848"
  Angle = 360
  AttacherType = Attacher::AttachEngine3D
  Height = 4.2
  Placement = pos=(0,15,75.5) rot=(0,1,0;1.5708rad)
  Radius = 4.3
FEATURE [Part::Cylinder] Cylinder014005939  label="Válec849"
  Angle = 360
  AttacherType = Attacher::AttachEngine3D
  Height = 10
  Placement = pos=(0,-25,42) rot=(0,1,0;1.5708rad)
  Radius = 2.65
FEATURE [Part::Cylinder] Cylinder014005940  label="Válec850"
  Angle = 360
  AttacherType = Attacher::AttachEngine3D
  Height = 10
  Placement = pos=(0,25,42) rot=(0,1,0;1.5708rad)
  Radius = 2.65
FEATURE [Part::Cylinder] Cylinder014005941  label="Válec851"
  Angle = 360
  AttacherType = Attacher::AttachEngine3D
  Height = 4.2
  Placement = pos=(5.8,-25,42) rot=(0,1,0;1.5708rad)
  Radius = 4.3
FEATURE [Part::Cylinder] Cylinder014005942  label="Válec852"
  Angle = 360
  AttacherType = Attacher::AttachEngine3D
  Height = 4.2
  Placement = pos=(5.8,25,42) rot=(0,1,0;1.5708rad)
  Radius = 4.3
FEATURE [Part::Prism] Prism010  label="Hranol010"
  AttacherType = Attacher::AttachEngine3D
  Circumradius = 5.8
  FirstAngle = 0
  Height = 4.5
  Placement = pos=(5.5,0,0) rot=(0,1,0;1.5708rad)
  Polygon = 6
  SecondAngle = 0
FEATURE [Part::Cylinder] Cylinder014005943  label="Válec853"
  Angle = 360
  AttacherType = Attacher::AttachEngine3D
  Height = 10
  Placement = pos=(0,0,0) rot=(0,1,0;1.5708rad)
  Radius = 3.15
FEATURE [Part::MultiFuse] Fusion001089102007007003008034028016004
  Placement = pos=(0,0,41.5) rot=(0,0,1;0rad)
  Shapes = -> [Prism010,Cylinder014005943]
FEATURE [Part::Box] Box021003  label="Krychle025"
  AttacherType = Attacher::AttachEngine3D
  Height = 84
  Length = 10
  Placement = pos=(0,-22,0) rot=(0,0,1;0rad)
  Width = 44
FEATURE [Part::Cylinder] Cylinder014005945  label="Válec855"
  Angle = 360
  AttacherType = Attacher::AttachEngine3D
  Height = 10
  Placement = pos=(0,-15,7.5) rot=(0,1,0;1.5708rad)
  Radius = 2.65
FEATURE [Part::Cylinder] Cylinder014005946  label="Válec856"
  Angle = 360
  AttacherType = Attacher::AttachEngine3D
  Height = 10
  Placement = pos=(0,15,7.5) rot=(0,1,0;1.5708rad)
  Radius = 2.65
FEATURE [Part::Cylinder] Cylinder014005947  label="Válec857"
  Angle = 360
  AttacherType = Attacher::AttachEngine3D
  Height = 10
  Placement = pos=(0,-15,75.5) rot=(0,1,0;1.5708rad)
  Radius = 2.65
FEATURE [Part::Cylinder] Cylinder014005948  label="Válec858"
  Angle = 360
  AttacherType = Attacher::AttachEngine3D
  Height = 10
  Placement = pos=(0,15,75.5) rot=(0,1,0;1.5708rad)
  Radius = 2.65
FEATURE [Part::Cylinder] Cylinder014005949  label="Válec859"
  Angle = 360
  AttacherType = Attacher::AttachEngine3D
  Height = 4.2
  Placement = pos=(0,-15,7.5) rot=(0,1,0;1.5708rad)
  Radius = 4.3
FEATURE [Part::Cylinder] Cylinder014005950  label="Válec860"
  Angle = 360
  AttacherType = Attacher::AttachEngine3D
  Height = 4.2
  Placement = pos=(0,15,7.5) rot=(0,1,0;1.5708rad)
  Radius = 4.3
FEATURE [Part::Cylinder] Cylinder014005951  label="Válec861"
  Angle = 360
  AttacherType = Attacher::AttachEngine3D
  Height = 4.2
  Placement = pos=(0,-15,75.5) rot=(0,1,0;1.5708rad)
  Radius = 4.3
FEATURE [Part::Cylinder] Cylinder014005952  label="Válec862"
  Angle = 360
  AttacherType = Attacher::AttachEngine3D
  Height = 4.2
  Placement = pos=(0,15,75.5) rot=(0,1,0;1.5708rad)
  Radius = 4.3
FEATURE [Part::Box] cube
  AttacherType = Attacher::AttachEngine3D
  Height = 10
  Length = 115
  Placement = pos=(0,-19,0) rot=(0,0,1;0rad)
  Width = 38
FEATURE [Part::Box] cube001
  AttacherType = Attacher::AttachEngine3D
  Height = 10
  Length = 115.1
  Placement = pos=(-0.01,16,5) rot=(-1,0,0;0.785398rad)
  Width = 10
FEATURE [Part::Box] cube002
  AttacherType = Attacher::AttachEngine3D
  Height = 10
  Length = 115.1
  Placement = pos=(-0.01,-16,5) rot=(1,0,0;2.35619rad)
  Width = 10
FEATURE [Part::Fuse] union001
  Base = -> cube001
  Tool = -> cube002
FEATURE [Part::Cut] difference
  Base = -> cube
  Placement = pos=(-10,0,99) rot=(0,1,0;1.5708rad)
  Tool = -> union001
FEATURE [Part::Prism] prism015  label="M4X007"
  AttacherType = Attacher::AttachEngine3D
  Circumradius = 4.21
  FirstAngle = 0
  Height = 3.4
  Placement = pos=(0,0,0) rot=(0,0,1;1.5708rad)
  Polygon = 6
  SecondAngle = 0
FEATURE [Part::Cylinder] Cylinder014005953  label="Válec863"
  Angle = 360
  AttacherType = Attacher::AttachEngine3D
  Height = 16
  Radius = 2.15
FEATURE [Part::MultiFuse] Fusion001089102007007003008034028016007  label="M4nut025"
  Placement = pos=(10,0,42) rot=(0,-1,0;1.5708rad)
  Shapes = -> [Cylinder014005953,prism015]
FEATURE [Part::Refine] Fusion001089102007007003008034028016007001  label="M4nut026"
  Placement = pos=(0,10,1) rot=(0,0,1;0rad)
  Source = -> Fusion001089102007007003008034028016007
FEATURE [Part::Refine] Fusion001089102007007003008034028016007002  label="M4nut027"
  Placement = pos=(0,-10,0) rot=(0,0,1;0rad)
  Source = -> Fusion001089102007007003008034028016007
FEATURE [Part::Refine] Fusion001089102007007003008034028016007003  label="M4nut028"
  Placement = pos=(0,0,25) rot=(0,0,1;0rad)
  Source = -> Fusion001089102007007003008034028016007
FEATURE [Part::Refine] Fusion001089102007007003008034028016007004  label="M4nut029"
  Placement = pos=(0,0,-25) rot=(0,0,1;0rad)
  Source = -> Fusion001089102007007003008034028016007
FEATURE [Part::MultiFuse] Fusion001089102007007003008034028016006
  Shapes = -> [Cylinder014005945,Cylinder014005946,Cylinder014005947,Cylinder014005948,Cylinder014005949,Cylinder014005950,Cylinder014005951,Cylinder014005952,Fusion001089102007007003008034028016007001,Fusion001089102007007003008034028016007002,Fusion001089102007007003008034028016007004,Fusion001089102007007003008034028016007003]
FEATURE [Part::Cut] Cut009003003009003003003007003002002  label="ListaRA1"
  Base = -> Box021003
  Tool = -> Fusion001089102007007003008034028016006
FEATURE [Part::Prism] prism016  label="M4X008"
  AttacherType = Attacher::AttachEngine3D
  Circumradius = 4.21
  FirstAngle = 0
  Height = 3.4
  Placement = pos=(0,0,0) rot=(0,0,1;1.5708rad)
  Polygon = 6
  SecondAngle = 0
FEATURE [Part::Cylinder] Cylinder014005954  label="Válec864"
  Angle = 360
  AttacherType = Attacher::AttachEngine3D
  Height = 16
  Radius = 2.15
FEATURE [Part::MultiFuse] Fusion001089102007007003008034028016007005  label="M4nut030"
  Placement = pos=(10,0,42) rot=(0,-1,0;1.5708rad)
  Shapes = -> [Cylinder014005954,prism016]
FEATURE [Part::Chamfer] Chamfer018  label="ListaRA 01"
  Base = -> Cut009003003009003003003007003002002
  Edges = 12 edges r=1: [Edge1,Edge2,Edge3,Edge4,Edge13,Edge14,Edge15,Edge16,Edge17,Edge18,Edge19,Edge20]
FEATURE [Part::Box] cube003
  AttacherType = Attacher::AttachEngine3D
  Height = 10
  Length = 115
  Placement = pos=(-1.5,-19,99) rot=(0,1,0;1.5708rad)
  Width = 38
FEATURE [Part::Cut] Cut009003003009003003003007003002003  label="lISTA x"
  Base = -> difference
  Tool = -> cube003
FEATURE [Part::Cylinder] Cylinder014005955  label="Válec865"
  Angle = 360
  AttacherType = Attacher::AttachEngine3D
  Height = 16
  Radius = 2.15
FEATURE [Part::Cylinder] Cylinder014005956  label="Válec866"
  Angle = 360
  AttacherType = Attacher::AttachEngine3D
  Height = 4
  Placement = pos=(0,0,16) rot=(0,0,1;0rad)
  Radius = 3.5
FEATURE [Part::MultiFuse] Fusion001089102007007003008034028016007006  label="M4nut031"
  Placement = pos=(10,0,41.5) rot=(0,-1,0;1.5708rad)
  Shapes = -> [Cylinder014005955,Cylinder014005956]
FEATURE [Part::Refine] Fusion001089102007007003008034028016007006001  label="M4nut032"
  Placement = pos=(0,10,0) rot=(0,0,1;0rad)
  Source = -> Fusion001089102007007003008034028016007006
FEATURE [Part::Refine] Fusion001089102007007003008034028016007006002  label="M4nut033"
  Placement = pos=(0,-10,0) rot=(0,0,1;0rad)
  Source = -> Fusion001089102007007003008034028016007006
FEATURE [Part::Refine] Fusion001089102007007003008034028016007006003  label="M4nut034"
  Placement = pos=(0,0,25) rot=(0,0,1;0rad)
  Source = -> Fusion001089102007007003008034028016007006
FEATURE [Part::Refine] Fusion001089102007007003008034028016007006004  label="M4nut035"
  Placement = pos=(0,0,-25) rot=(0,0,1;0rad)
  Source = -> Fusion001089102007007003008034028016007006
FEATURE [Part::MultiFuse] Fusion001089102007007003008034028016007006005
  Shapes = -> [Fusion001089102007007003008034028016007006001,Fusion001089102007007003008034028016007006002,Fusion001089102007007003008034028016007006003,Fusion001089102007007003008034028016007006004]
FEATURE [Part::Cut] Cut009003003009003003003007003002004
  Base = -> Cut009003003009003003003007003002003
  Tool = -> Fusion001089102007007003008034028016007006005
FEATURE [Part::Cylinder] Cylinder014005957  label="Válec867"
  Angle = 360
  AttacherType = Attacher::AttachEngine3D
  Height = 3
  Placement = pos=(-12.5,0,-11) rot=(0,1,0;1.5708rad)
  Radius = 5
FEATURE [Part::Cylinder] Cylinder014005958  label="Válec868"
  Angle = 360
  AttacherType = Attacher::AttachEngine3D
  Height = 3
  Placement = pos=(-12.5,0,94) rot=(0,1,0;1.5708rad)
  Radius = 5
FEATURE [Part::MultiFuse] Fusion001089102007007003008034028016007006006  label="Liasa RA02"
  Shapes = -> [Cut009003003009003003003007003002004,Cylinder014005957,Cylinder014005958]
FEATURE [Part::Cylinder] Cylinder014005959  label="Válec869"
  Angle = 360
  AttacherType = Attacher::AttachEngine3D
  Height = 52
  Placement = pos=(0,0,-10) rot=(0,0,1;0rad)
  Radius = 53
FEATURE [Part::Cylinder] Cylinder014005960  label="Válec870"
  Angle = 360
  AttacherType = Attacher::AttachEngine3D
  Height = 44
  Placement = pos=(0,0,-12) rot=(0,0,1;0rad)
  Radius = 50
FEATURE [Part::Cylinder] Cylinder014005961  label="Válec871"
  Angle = 360
  AttacherType = Attacher::AttachEngine3D
  Height = 50
  Placement = pos=(0,0,-10) rot=(0,0,1;0rad)
  Radius = 39
FEATURE [Part::MultiFuse] Fusion001089102007007003008034028016007006007
  Shapes = -> [Cylinder014005961,Cylinder014005960]
FEATURE [Part::Cut] Cut009003003009003003003007003002005  label="Telo001"
  Base = -> Cylinder014005959
  Tool = -> Fusion001089102007007003008034028016007006007
FEATURE [Part::Cylinder] Cylinder014005962  label="Válec872"
  Angle = 360
  AttacherType = Attacher::AttachEngine3D
  Height = 52
  Placement = pos=(0,-45,-10) rot=(0,0,1;0rad)
  Radius = 5
FEATURE [Part::Refine] Cylinder014005962001  label="Válec873"
  Placement = pos=(0,0,0) rot=(0,0,1;1.0472rad)
  Source = -> Cylinder014005962
FEATURE [Part::Refine] Cylinder014005962002  label="Válec874"
  Placement = pos=(0,0,0) rot=(0,0,1;2.0944rad)
  Source = -> Cylinder014005962
FEATURE [Part::Refine] Cylinder014005962003  label="Válec875"
  Placement = pos=(0,0,0) rot=(0,0,1;3.14159rad)
  Source = -> Cylinder014005962
FEATURE [Part::Refine] Cylinder014005962004  label="Válec876"
  Placement = pos=(0,0,0) rot=(0,0,1;4.18879rad)
  Source = -> Cylinder014005962
FEATURE [Part::Refine] Cylinder014005962005  label="Válec877"
  Placement = pos=(0,0,0) rot=(0,0,-1;1.0472rad)
  Source = -> Cylinder014005962
FEATURE [Part::Cylinder] Cylinder014005962006  label="Válec878"
  Angle = 360
  AttacherType = Attacher::AttachEngine3D
  Height = 52
  Placement = pos=(0,-45,-10) rot=(0,0,1;0rad)
  Radius = 2.65
FEATURE [Part::Cylinder] Cylinder014005962007  label="Válec879"
  Angle = 360
  AttacherType = Attacher::AttachEngine3D
  Height = 5
  Placement = pos=(0,-45,37) rot=(0,0,1;0rad)
  Radius = 4.4
FEATURE [Part::MultiFuse] Fusion001089102007007003008034028016007006009  label="Inbus"
  Shapes = -> [Cylinder014005962006,Cylinder014005962007]
FEATURE [Part::Refine] Fusion001089102007007003008034028016007006009001  label="Inbus001"
  Placement = pos=(0,0,0) rot=(0,0,1;1.0472rad)
  Source = -> Fusion001089102007007003008034028016007006009
FEATURE [Part::Refine] Fusion001089102007007003008034028016007006009002  label="Inbus002"
  Placement = pos=(0,0,0) rot=(0,0,1;2.0944rad)
  Source = -> Fusion001089102007007003008034028016007006009
FEATURE [Part::Refine] Fusion001089102007007003008034028016007006009003  label="Inbus003"
  Placement = pos=(0,0,0) rot=(0,0,1;3.14159rad)
  Source = -> Fusion001089102007007003008034028016007006009
FEATURE [Part::Refine] Fusion001089102007007003008034028016007006009004  label="Inbus004"
  Placement = pos=(0,0,0) rot=(0,0,1;4.18879rad)
  Source = -> Fusion001089102007007003008034028016007006009
FEATURE [Part::Refine] Fusion001089102007007003008034028016007006009005  label="Inbus005"
  Placement = pos=(0,0,0) rot=(0,0,-1;1.0472rad)
  Source = -> Fusion001089102007007003008034028016007006009
FEATURE [Part::Feature] Cut005_solid004  label="Planetary Gear Box distance  RA004"
  shape: bbox 41 x 41 x 22.5 mm, 15 faces (baked)
FEATURE [Part::Box] Box021004  label="Krychle026"
  AttacherType = Attacher::AttachEngine3D
  Height = 21
  Length = 42
  Placement = pos=(-21,-21,0) rot=(0,0,1;0rad)
  Width = 42
FEATURE [Part::Cut] Cut009003003009003003003007003002007  label="polozka"
  Base = -> Cut005_solid004
  Tool = -> Box021004
FEATURE [Part::Prism] prism017  label="M4X009"
  AttacherType = Attacher::AttachEngine3D
  Circumradius = 4.6
  FirstAngle = 0
  Height = 4.2
  Placement = pos=(0,0,7) rot=(0,0,1;1.5708rad)
  Polygon = 6
  SecondAngle = 0
FEATURE [Part::Box] Box021005  label="Krychle027"
  AttacherType = Attacher::AttachEngine3D
  Height = 4.1
  Length = 8
  Placement = pos=(-4,0,7) rot=(0,0,1;0rad)
  Width = 10
FEATURE [Part::Cylinder] Cylinder014005962008  label="Válec880"
  Angle = 360
  AttacherType = Attacher::AttachEngine3D
  Height = 22.5
  Radius = 2.65
FEATURE [Part::MultiFuse] Fusion001089102007007003008034028016007006009008  label="M4nut036"
  Placement = pos=(0,-45,0) rot=(0,0,1;0rad)
  Shapes = -> [Cylinder014005962008,Box021005,prism017]
FEATURE [Part::Refine] Fusion001089102007007003008034028016007006009009  label="M4nut037"
  Placement = pos=(0,0,0) rot=(0,0,1;1.0472rad)
  Source = -> Fusion001089102007007003008034028016007006009008
FEATURE [Part::Refine] Fusion001089102007007003008034028016007006009010  label="M4nut038"
  Placement = pos=(0,0,0) rot=(0,0,1;3.14159rad)
  Source = -> Fusion001089102007007003008034028016007006009008
FEATURE [Part::Refine] Fusion001089102007007003008034028016007006009011  label="M4nut039"
  Placement = pos=(0,0,0) rot=(0,0,1;4.18879rad)
  Source = -> Fusion001089102007007003008034028016007006009008
FEATURE [Part::Refine] Fusion001089102007007003008034028016007006009012  label="M4nut040"
  Placement = pos=(0,0,0) rot=(0,0,-1;1.0472rad)
  Source = -> Fusion001089102007007003008034028016007006009008
FEATURE [Part::Refine] Fusion001089102007007003008034028016007006009014  label="M4nut041"
  Placement = pos=(0,0,0) rot=(0,0,1;2.0944rad)
  Source = -> Fusion001089102007007003008034028016007006009008
FEATURE [Part::MultiFuse] Fusion001089102007007003008034028016007006009013  label="Matky M5"
  Placement = pos=(0,0,27) rot=(0,0,1;0.523599rad)
  Shapes = -> [Fusion001089102007007003008034028016007006009008,Fusion001089102007007003008034028016007006009009,Fusion001089102007007003008034028016007006009010,Fusion001089102007007003008034028016007006009011,Fusion001089102007007003008034028016007006009012,Fusion001089102007007003008034028016007006009014]
FEATURE [Part::Feature] Cut005023015002007002065013  label="Port16a015Ra004"
  Placement = pos=(43,0,17) rot=(0,0,1;1.5708rad)
  shape: bbox 15 x 14.5 x 16.4 mm, 6 faces (baked)
FEATURE [Part::Cylinder] Cylinder014005962009  label="Válec881"
  Angle = 360
  AttacherType = Attacher::AttachEngine3D
  Height = 4.5
  Placement = pos=(48.5,0,17) rot=(0,1,0;1.5708rad)
  Radius = 12
FEATURE [Part::MultiFuse] Fusion001089102007007003008034028016007006008  label="Kryt"
  Shapes = -> [Cylinder014005962,Cylinder014005962001,Cylinder014005962002,Cylinder014005962003,Cylinder014005962004,Cylinder014005962005,Cylinder014005962009]
FEATURE [Part::MultiFuse] Fusion001089102007007003008034028016007006009006  label="Telo"
  Shapes = -> [Cut009003003009003003003007003002005,Fusion001089102007007003008034028016007006008]
FEATURE [Part::Cylinder] Cylinder014005962010  label="Válec882"
  Angle = 360
  AttacherType = Attacher::AttachEngine3D
  Height = 2
  Placement = pos=(51.5,0,17) rot=(0,1,0;1.5708rad)
  Radius = 9
FEATURE [Part::Cylinder] Cylinder014005962011  label="Válec883"
  Angle = 360
  AttacherType = Attacher::AttachEngine3D
  Height = 10
  Placement = pos=(0,0,36) rot=(0,0,1;0rad)
  Radius = 6.5
FEATURE [Part::MultiFuse] Fusion001089102007007003008034028016007006009007  label="Srouby"
  Shapes = -> [Fusion001089102007007003008034028016007006009,Fusion001089102007007003008034028016007006009001,Fusion001089102007007003008034028016007006009002,Fusion001089102007007003008034028016007006009003,Fusion001089102007007003008034028016007006009004,Fusion001089102007007003008034028016007006009005,Fusion001089102007007003008034028016007006009013,Cut005023015002007002065013,Cylinder014005962010,+1 more]
FEATURE [Part::Cut] Cut009003003009003003003007003002006  label="Cap"
  Base = -> Fusion001089102007007003008034028016007006009006
  Tool = -> Fusion001089102007007003008034028016007006009007
FEATURE [Part::Chamfer] Chamfer019  label="CapA"
  Base = -> Cut009003003009003003003007003002006
  Edges = 2 edges r=1: [Edge4,Edge6]
FEATURE [Part::Part2DObjectPython] ShapeString058  # Draft 2D object (typed FeaturePython)
  FontFile = <userpath>/MyGit/Small-EQ-mount-OnStep/ttf/ARIALBD.TTF
  Placement = pos=(0,0,0) rot=(1,0,0;1.5708rad)
  Size = 3
  String = 12V
  Tracking = 0
FEATURE [Part::Part2DObjectPython] ShapeString056  # Draft 2D object (typed FeaturePython)
  FontFile = <userpath>/MyGit/Small-EQ-mount-OnStep/ttf/ARIALBD.TTF
  Placement = pos=(0,0,0) rot=(1,0,0;1.5708rad)
  Size = 3
  String = USB
  Tracking = 0
FEATURE [Part::Part2DObjectPython] ShapeString059  # Draft 2D object (typed FeaturePython)
  FontFile = <userpath>/MyGit/Small-EQ-mount-OnStep/ttf/ARIALBD.TTF
  Placement = pos=(0,0,0) rot=(1,0,0;1.5708rad)
  Size = 3
  String = 12V 
  Tracking = 0
FEATURE [Part::Feature] Cut005023015002007002056  label="Port16a014De"
  Placement = pos=(-34,-12,18) rot=(0,0,1;1.5708rad)
  shape: bbox 15 x 14.5 x 16.4 mm, 6 faces (baked)
FEATURE [Part::Feature] Cut005023015002007002057  label="Port16a015Ra"
  Placement = pos=(-34,10,18) rot=(0,0,1;1.5708rad)
  shape: bbox 15 x 14.5 x 16.4 mm, 6 faces (baked)
FEATURE [Part::Feature] Cut005023015002007002055  label="Port16a013pwr"
  Placement = pos=(-60,-18,18) rot=(0,0,1;1.5708rad)
  shape: bbox 15 x 14.5 x 16.4 mm, 6 faces (baked)
FEATURE [Part::Cylinder] Cylinder190  label="Válec163"
  Angle = 360
  AttacherType = Attacher::AttachEngine3D
  Height = 10
  Placement = pos=(47,29.9,28) rot=(0,0,1;0rad)
  Radius = 1.2
FEATURE [Part::Cylinder] Cylinder189  label="Válec162"
  Angle = 360
  AttacherType = Attacher::AttachEngine3D
  Height = 90
  Placement = pos=(40,45,8) rot=(1,0,0;1.5708rad)
  Radius = 1
FEATURE [Part::Box] Box088  label="usb006"
  AttacherType = Attacher::AttachEngine3D
  Height = 11
  Length = 20
  Placement = pos=(44,12,19.4) rot=(0,0,1;0rad)
  Width = 12.6
FEATURE [Part::Cylinder] Cylinder191  label="cam001"
  Angle = 360
  AttacherType = Attacher::AttachEngine3D
  Height = 10
  Placement = pos=(0,-22.5,27) rot=(0,1,0;1.5708rad)
  Radius = 3.4
FEATURE [Part::Box] Box089  label="RJ006ST4"
  AttacherType = Attacher::AttachEngine3D
  Height = 14
  Length = 20
  Placement = pos=(44,-8.5,16.4) rot=(0,0,1;0rad)
  Width = 16
FEATURE [Part::Extrusion] Extrude057  label="USB005"
  Base = -> ShapeString056
  Dir = (0,-1,-2e-16)
  DirMode = 2
  FaceMakerClass = Part::FaceMakerBullseye
  LengthFwd = 0.5
  LengthRev = 0
  Placement = pos=(53.5,14,33) rot=(0,0,1;1.5708rad)
  Solid = true
  Symmetric = false
FEATURE [Part::Box] Box087  label="Pwr"
  AttacherType = Attacher::AttachEngine3D
  Height = 11.4
  Length = 20
  Placement = pos=(40.9,-25.9,19) rot=(0,0,1;0rad)
  Width = 9.4
FEATURE [Part::Extrusion] Extrude056  label="12Vout"
  Base = -> ShapeString058
  Dir = (0,-1,-2e-16)
  DirMode = 2
  FaceMakerClass = Part::FaceMakerBullseye
  LengthFwd = 0.5
  LengthRev = 0
  Placement = pos=(-53.5,-13.5,33) rot=(0,0,-1;1.5708rad)
  Solid = true
  Symmetric = false
FEATURE [Part::Cylinder] Cylinder187  label="Válec160"
  Angle = 360
  AttacherType = Attacher::AttachEngine3D
  Height = 6.5
  Placement = pos=(-46.5,29.8,32) rot=(0,0,1;0rad)
  Radius = 5
FEATURE [Part::Cylinder] Cylinder195  label="Válec166"
  Angle = 360
  AttacherType = Attacher::AttachEngine3D
  Height = 10
  Placement = pos=(-46.5,29.8,28) rot=(0,0,1;0rad)
  Radius = 1.2
FEATURE [Part::Cylinder] Cylinder201  label="Válec171"
  Angle = 360
  AttacherType = Attacher::AttachEngine3D
  Height = 10
  Placement = pos=(-46.5,-30.9,28) rot=(0,0,1;0rad)
  Radius = 1.2
FEATURE [Part::Extrusion] Extrude061  label="12V005"
  Base = -> ShapeString059
  Dir = (0,-1,-2e-16)
  DirMode = 2
  FaceMakerClass = Part::FaceMakerBullseye
  LengthFwd = 0.5
  LengthRev = 0
  Placement = pos=(53.5,-25,33) rot=(0,0,1;1.5708rad)
  Solid = true
  Symmetric = false
FEATURE [Part::Cylinder] Cylinder199  label="Dira stres"
  Angle = 360
  AttacherType = Attacher::AttachEngine3D
  Height = 10
  Placement = pos=(0,0,32) rot=(0,0,1;0rad)
  Radius = 6
FEATURE [Part::Cylinder] Cylinder200  label="Válec170"
  Angle = 360
  AttacherType = Attacher::AttachEngine3D
  Height = 6.5
  Placement = pos=(-46.5,-30.9,32) rot=(0,0,1;0rad)
  Radius = 5
FEATURE [Part::Cylinder] Cylinder197  label="Válec168"
  Angle = 360
  AttacherType = Attacher::AttachEngine3D
  Height = 6.5
  Placement = pos=(47,-30.9,32) rot=(0,0,1;0rad)
  Radius = 5
FEATURE [Part::Cylinder] Cylinder194  label="Válec165"
  Angle = 360
  AttacherType = Attacher::AttachEngine3D
  Height = 10
  Placement = pos=(47,-30.9,28) rot=(0,0,1;0rad)
  Radius = 1.2
FEATURE [Part::MultiFuse] Fusion018071090  label="dir srouby005"
  Shapes = -> [Cylinder190,Cylinder195,Cylinder194,Cylinder201]
FEATURE [Part::Cylinder] Cylinder193  label="Led1"
  Angle = 360
  AttacherType = Attacher::AttachEngine3D
  Height = 15
  Placement = pos=(44,-12,27) rot=(0,1,0;1.5708rad)
  Radius = 1.75
FEATURE [Part::Cylinder] Cylinder196  label="Válec167"
  Angle = 360
  AttacherType = Attacher::AttachEngine3D
  Height = 90
  Placement = pos=(-40,45,8) rot=(1,0,0;1.5708rad)
  Radius = 1
FEATURE [Part::MultiFuse] Fusion018071087  label="hornidiry006"
  Shapes = -> [Cylinder189,Cylinder196]
FEATURE [Part::Cylinder] Cylinder198  label="Válec169"
  Angle = 360
  AttacherType = Attacher::AttachEngine3D
  Height = 6.5
  Placement = pos=(47,29.9,32) rot=(0,0,1;0rad)
  Radius = 5
FEATURE [Part::MultiFuse] Fusion018071084  label="sloupky"
  Shapes = -> [Cylinder198,Cylinder187,Cylinder197,Cylinder200]
FEATURE [Part::Box] Box021006  label="PWRsw001"
  AttacherType = Attacher::AttachEngine3D
  Height = 9
  Length = 15
  Placement = pos=(-57,8,16) rot=(0,0,1;0rad)
  Width = 15
FEATURE [Part::Box] Box090  label="RJ006RA"
  AttacherType = Attacher::AttachEngine3D
  Height = 14
  Length = 20
  Placement = pos=(0,1,16.4) rot=(0,0,1;0rad)
  Width = 16
FEATURE [Part::Box] Box091  label="RJ006DE"
  AttacherType = Attacher::AttachEngine3D
  Height = 14
  Length = 20
  Placement = pos=(0,-15,16.4) rot=(0,0,1;0rad)
  Width = 16
FEATURE [Part::Cylinder] Cylinder203  label="Led002"
  Angle = 360
  AttacherType = Attacher::AttachEngine3D
  Height = 15
  Placement = pos=(44,-12,21.5) rot=(0,1,0;1.5708rad)
  Radius = 1.75
FEATURE [Part::Cylinder] Cylinder204  label="extpwr"
  Angle = 360
  AttacherType = Attacher::AttachEngine3D
  Height = 10
  Placement = pos=(-55,-18,18) rot=(0,1,0;1.5708rad)
  Radius = 4.1
FEATURE [Part::Cylinder] Cylinder205  label="camLed"
  Angle = 360
  AttacherType = Attacher::AttachEngine3D
  Height = 10
  Placement = pos=(0,-22.5,20) rot=(0,1,0;1.5708rad)
  Radius = 1.8
FEATURE [Part::MultiFuse] Fusion018071085  label="PCB007"
  Shapes = -> [Box087,Box088,Box089,Cut005023015002007002055,Cut005023015002007002056,Cut005023015002007002057,Box021006,Box090,Box091,Cylinder203,Cylinder193,Cylinder191,Cylinder204,Cylinder205]
FEATURE [Part::Cylinder] Cylinder014005962013  label="Válec885"
  Angle = 360
  AttacherType = Attacher::AttachEngine3D
  Height = 7
  Placement = pos=(0,0,33) rot=(0,0,1;0rad)
  Radius = 53
FEATURE [Part::Box] Box021007  label="Krychle055"
  AttacherType = Attacher::AttachEngine3D
  Height = 35
  Length = 108
  Placement = pos=(-54,-38,5) rot=(0,0,1;0rad)
  Width = 76
FEATURE [Part::Box] Box021008  label="Krychle056"
  AttacherType = Attacher::AttachEngine3D
  Height = 36
  Length = 104
  Placement = pos=(-52,-36,2) rot=(0,0,1;0rad)
  Width = 72
FEATURE [Part::Cylinder] Cylinder014005962015  label="Válec887"
  Angle = 360
  AttacherType = Attacher::AttachEngine3D
  Height = 7
  Placement = pos=(0,-45,33) rot=(0,0,1;0rad)
  Radius = 2.65
FEATURE [Part::Cylinder] Cylinder014005962016  label="Válec888"
  Angle = 360
  AttacherType = Attacher::AttachEngine3D
  Height = 5.4
  Placement = pos=(0,-45,33) rot=(0,0,1;0rad)
  Radius = 4.3
FEATURE [Part::MultiFuse] Fusion001089102007007003008034028016007006009018  label="Inbus006"
  Shapes = -> [Cylinder014005962015,Cylinder014005962016]
FEATURE [Part::Refine] Fusion001089102007007003008034028016007006009018001  label="Inbus007"
  Placement = pos=(0,0,0) rot=(0,0,1;1.0472rad)
  Source = -> Fusion001089102007007003008034028016007006009018
FEATURE [Part::Refine] Fusion001089102007007003008034028016007006009018002  label="Inbus008"
  Placement = pos=(0,0,0) rot=(0,0,1;2.0944rad)
  Source = -> Fusion001089102007007003008034028016007006009018
FEATURE [Part::Refine] Fusion001089102007007003008034028016007006009018003  label="Inbus009"
  Placement = pos=(0,0,0) rot=(0,0,1;3.14159rad)
  Source = -> Fusion001089102007007003008034028016007006009018
FEATURE [Part::Refine] Fusion001089102007007003008034028016007006009018004  label="Inbus010"
  Placement = pos=(0,0,0) rot=(0,0,1;4.18879rad)
  Source = -> Fusion001089102007007003008034028016007006009018
FEATURE [Part::Refine] Fusion001089102007007003008034028016007006009018005  label="Inbus011"
  Placement = pos=(0,0,0) rot=(0,0,-1;1.0472rad)
  Source = -> Fusion001089102007007003008034028016007006009018
FEATURE [Part::MultiFuse] Fusion001089102007007003008034028016007006009018006  label="Inbus012"
  Shapes = -> [Fusion001089102007007003008034028016007006009018,Fusion001089102007007003008034028016007006009018001,Fusion001089102007007003008034028016007006009018002,Fusion001089102007007003008034028016007006009018003,Fusion001089102007007003008034028016007006009018004,Fusion001089102007007003008034028016007006009018005]
FEATURE [Part::Part2DObjectPython] ShapeString062  # Draft 2D object (typed FeaturePython)
  FontFile = <userpath>/MyGit/Small-EQ-mount-OnStep/ttf/ARIALBD.TTF
  Placement = pos=(0,0,0) rot=(-1,0,0;1.5708rad)
  Size = 10
  String = OnStep  HrEM
  Tracking = 0
FEATURE [Part::Extrusion] Extrude062  label="Hrem"
  Base = -> ShapeString062
  Dir = (0,1,-2e-16)
  DirMode = 2
  FaceMakerClass = Part::FaceMakerBullseye
  LengthFwd = 0.5
  LengthRev = 0
  Placement = pos=(43,37.5,16) rot=(0,1,0;3.14159rad)
  Solid = true
  Symmetric = false
FEATURE [Part::Part2DObjectPython] ShapeString063  # Draft 2D object (typed FeaturePython)
  FontFile = <userpath>/MyGit/Small-EQ-mount-OnStep/ttf/ARIALBD.TTF
  Placement = pos=(0,0,0) rot=(1,0,0;1.5708rad)
  Size = 3
  String = ST4 SHC
  Tracking = 0
FEATURE [Part::Extrusion] Extrude063  label="ST4"
  Base = -> ShapeString063
  Dir = (0,-1,2e-16)
  DirMode = 2
  FaceMakerClass = Part::FaceMakerBullseye
  LengthFwd = 0.5
  LengthRev = 0
  Placement = pos=(53.5,-8.5,33) rot=(0,0,1;1.5708rad)
  Solid = true
  Symmetric = false
FEATURE [Part::Chamfer] Chamfer021
  Base = -> Cylinder014005962013
  Edges = 2 edges r=1: [Edge1,Edge3]
FEATURE [Part::MultiFuse] Fusion001089102007007003008034028016007006009018007
  Shapes = -> [Box021007,Chamfer021]
FEATURE [Part::Cut] Cut009003003009003003003007003002006003
  Base = -> Fusion001089102007007003008034028016007006009018007
  Tool = -> Box021008
FEATURE [Part::MultiFuse] Fusion001089102007007003008034028016007006009018008
  Shapes = -> [Fusion018071084,Cut009003003009003003003007003002006003]
FEATURE [Part::Part2DObjectPython] ShapeString064  # Draft 2D object (typed FeaturePython)
  FontFile = <userpath>/MyGit/Small-EQ-mount-OnStep/ttf/ARIALBD.TTF
  Placement = pos=(0,0,0) rot=(1,0,0;1.5708rad)
  Size = 3
  String = Power
  Tracking = 0
FEATURE [Part::Extrusion] Extrude064  label="Pwr001"
  Base = -> ShapeString064
  Dir = (0,-1,2e-16)
  DirMode = 2
  FaceMakerClass = Part::FaceMakerBullseye
  LengthFwd = 0.5
  LengthRev = 0
  Placement = pos=(-53.5,22,33) rot=(0,0,-1;1.5708rad)
  Solid = true
  Symmetric = false
FEATURE [Part::MultiFuse] Fusion018071089  label="texty011"
  Shapes = -> [Extrude056,Extrude061,Extrude057,Extrude062,Extrude063,Extrude064]
FEATURE [Part::MultiFuse] Fusion018071086  label="Diry"
  Shapes = -> [Fusion018071085,Fusion018071090,Cylinder199,Fusion018071087,Fusion018071089,Fusion001089102007007003008034028016007006009018006]
FEATURE [Part::Cut] Cut009003003009003003003007003002006004
  Base = -> Fusion001089102007007003008034028016007006009018008
  Tool = -> Fusion018071086
FEATURE [Part::Fillet] Fillet001  label="OnstepBox"
  Base = -> Cut009003003009003003003007003002006004
  Edges = 4 edges r=2: [Edge143,Edge145,Edge244,Edge411]
FEATURE [Part::Part2DObjectPython] ShapeString073  # Draft 2D object (typed FeaturePython)
  FontFile = <path>
  Placement = pos=(0,0,0) rot=(1,0,0;3.14159rad)
  Size = 6
  String = ESP32
  Tracking = 0
FEATURE [App::Part] Part  label="Temp"
  Group = -> [Cylinder,cycloidgear,Fusion,Cylinder001,Chamfer,Cylinder001002,Cylinder001001,Cylinder001004,Cylinder001005,Cylinder001003,Cut,Cylinder001011,Cylinder001006,Cylinder001008,Cylinder001010,Cylinder001007,Fusion001,cycloidgear001,Chamfer001,Cylinder001009,Cylinder001012,Cut001,cycloidgear002,Fusion002,Cylinder001016,Cylinder001013,Cylinder001015,Cylinder001017,Cylinder001019,Chamfer002,+154 more]
  Origin = -> Origin
FEATURE [Part::Box] Box255  label="Krychle114"
  AttacherType = Attacher::AttachEngine3D
  Height = 2
  Length = 108
  Placement = pos=(-54,-38,0) rot=(0,0,1;0rad)
  Width = 76
FEATURE [Part::Cylinder] Cylinder262  label="Válec207"
  Angle = 360
  AttacherType = Attacher::AttachEngine3D
  Height = 80
  Placement = pos=(-40,40,5) rot=(1,0,0;1.5708rad)
  Radius = 1
FEATURE [Part::Box] Box256  label="Krychle115"
  AttacherType = Attacher::AttachEngine3D
  Height = 6
  Length = 104
  Placement = pos=(-52,-36,2) rot=(0,0,1;0rad)
  Width = 72
FEATURE [Part::MultiFuse] Fusion018209105
  Shapes = -> [Box255,Box256]
FEATURE [Part::Box] Box257  label="Krychle116"
  AttacherType = Attacher::AttachEngine3D
  Height = 6
  Length = 100
  Placement = pos=(-50,-34,2) rot=(0,0,1;0rad)
  Width = 68
FEATURE [Part::Cylinder] Cylinder263  label="Válec208"
  Angle = 360
  AttacherType = Attacher::AttachEngine3D
  Height = 80
  Placement = pos=(40,40,5) rot=(1,0,0;1.5708rad)
  Radius = 1
FEATURE [Part::MultiFuse] Fusion018209103  label="hornidiry008"
  Shapes = -> [Cylinder263,Cylinder262]
FEATURE [Part::Box] Box258  label="Krychle117"
  AttacherType = Attacher::AttachEngine3D
  Height = 6
  Length = 104
  Placement = pos=(-52,-34,4) rot=(0,0,1;0rad)
  Width = 68
FEATURE [Part::Box] Box021009  label="Krychle118"
  AttacherType = Attacher::AttachEngine3D
  Height = 10
  Length = 2
  Placement = pos=(-1,-22,0) rot=(0,0,1;0rad)
  Width = 44
FEATURE [Part::Cylinder] Cylinder014005962017  label="Válec889"
  Angle = 360
  AttacherType = Attacher::AttachEngine3D
  Height = 10
  Placement = pos=(0,22,0) rot=(0,0,1;0rad)
  Radius = 1
FEATURE [Part::Cylinder] Cylinder014005962018  label="Válec890"
  Angle = 360
  AttacherType = Attacher::AttachEngine3D
  Height = 10
  Placement = pos=(0,-22,0) rot=(0,0,1;0rad)
  Radius = 1
FEATURE [Part::MultiFuse] Fusion001089102007007003008034028016007006009018009  label="ZEBRO"
  Shapes = -> [Box021009,Cylinder014005962017,Cylinder014005962018]
FEATURE [Part::Refine] Fusion001089102007007003008034028016007006009018009001  label="ZEBRO001"
  Placement = pos=(4,0,0) rot=(0,0,1;0rad)
  Source = -> Fusion001089102007007003008034028016007006009018009
FEATURE [Part::Refine] Fusion001089102007007003008034028016007006009018009002  label="ZEBRO002"
  Placement = pos=(-4,0,0) rot=(0,0,1;0rad)
  Source = -> Fusion001089102007007003008034028016007006009018009
FEATURE [Part::Refine] Fusion001089102007007003008034028016007006009018009003  label="ZEBRO003"
  Placement = pos=(-8,0,0) rot=(0,0,1;0rad)
  Source = -> Fusion001089102007007003008034028016007006009018009
FEATURE [Part::Refine] Fusion001089102007007003008034028016007006009018009004  label="ZEBRO004"
  Placement = pos=(8,0,0) rot=(0,0,1;0rad)
  Source = -> Fusion001089102007007003008034028016007006009018009
FEATURE [Part::Refine] Fusion001089102007007003008034028016007006009018009005  label="ZEBRO005"
  Placement = pos=(12,0,0) rot=(0,0,1;0rad)
  Source = -> Fusion001089102007007003008034028016007006009018009
FEATURE [Part::Refine] Fusion001089102007007003008034028016007006009018009006  label="ZEBRO006"
  Placement = pos=(-12,0,0) rot=(0,0,1;0rad)
  Source = -> Fusion001089102007007003008034028016007006009018009
FEATURE [Part::Refine] Fusion001089102007007003008034028016007006009018009007  label="ZEBRO007"
  Placement = pos=(16,0,0) rot=(0,0,1;0rad)
  Source = -> Fusion001089102007007003008034028016007006009018009
FEATURE [Part::Refine] Fusion001089102007007003008034028016007006009018009008  label="ZEBRO008"
  Placement = pos=(-16,0,0) rot=(0,0,1;0rad)
  Source = -> Fusion001089102007007003008034028016007006009018009
FEATURE [Part::Refine] Fusion001089102007007003008034028016007006009018009009  label="ZEBRO009"
  Placement = pos=(20,0,0) rot=(0,0,1;0rad)
  Source = -> Fusion001089102007007003008034028016007006009018009
FEATURE [Part::Refine] Fusion001089102007007003008034028016007006009018009010  label="ZEBRO010"
  Placement = pos=(-20,0,0) rot=(0,0,1;0rad)
  Source = -> Fusion001089102007007003008034028016007006009018009
FEATURE [Part::Refine] Fusion001089102007007003008034028016007006009018009011  label="ZEBRO011"
  Placement = pos=(24,0,0) rot=(0,0,1;0rad)
  Source = -> Fusion001089102007007003008034028016007006009018009
FEATURE [Part::Refine] Fusion001089102007007003008034028016007006009018009012  label="ZEBRO012"
  Placement = pos=(-24,0,0) rot=(0,0,1;0rad)
  Source = -> Fusion001089102007007003008034028016007006009018009
FEATURE [Part::MultiFuse] Fusion018209104  label="Zebra001"
  Shapes = -> [Fusion001089102007007003008034028016007006009018009,Fusion001089102007007003008034028016007006009018009002,Fusion001089102007007003008034028016007006009018009001,Fusion001089102007007003008034028016007006009018009003,Fusion001089102007007003008034028016007006009018009004,Fusion001089102007007003008034028016007006009018009005,Fusion001089102007007003008034028016007006009018009006,+6 more]
FEATURE [Part::Refine] Fusion001089102007007003008034028016007006009018009013  label="ZEBRO013"
  Placement = pos=(-28,0,0) rot=(0,0,1;0rad)
  Source = -> Fusion001089102007007003008034028016007006009018009
FEATURE [Part::Refine] Fusion001089102007007003008034028016007006009018009014  label="ZEBRO014"
  Placement = pos=(28,0,0) rot=(0,0,1;0rad)
  Source = -> Fusion001089102007007003008034028016007006009018009
FEATURE [Part::Refine] Fusion001089102007007003008034028016007006009018009015  label="ZEBRO015"
  Placement = pos=(32,0,0) rot=(0,0,1;0rad)
  Source = -> Fusion001089102007007003008034028016007006009018009
FEATURE [Part::Refine] Fusion001089102007007003008034028016007006009018009016  label="ZEBRO016"
  Placement = pos=(-32,0,0) rot=(0,0,1;0rad)
  Source = -> Fusion001089102007007003008034028016007006009018009
FEATURE [Part::MultiFuse] Fusion018209102
  Shapes = -> [Fusion018209103,Box257,Box258,Fusion018209104,Fusion001089102007007003008034028016007006009018009013,Fusion001089102007007003008034028016007006009018009014,Fusion001089102007007003008034028016007006009018009015,Fusion001089102007007003008034028016007006009018009016]
FEATURE [Part::Cut] Cut005023015002007002066  label="Top001"
  Base = -> Fusion018209105
  Tool = -> Fusion018209102
FEATURE [Part::Fillet] Fillet002  label="OnstepV=Cap"
  Base = -> Cut005023015002007002066
  Edges = 8 edges r=2: [Edge1,Edge3,Edge6,Edge15,Edge85,Edge89,Edge96,Edge100]
  Placement = pos=(0,0,3) rot=(0,0,1;0rad)
FEATURE [Part::Prism] prism018  label="M4X010"
  AttacherType = Attacher::AttachEngine3D
  Circumradius = 4.21
  FirstAngle = 0
  Height = 3.4
  Placement = pos=(0,0,0) rot=(0,0,1;1.5708rad)
  Polygon = 6
  SecondAngle = 0
FEATURE [Part::Cylinder] Cylinder014005962027  label="Válec899"
  Angle = 360
  AttacherType = Attacher::AttachEngine3D
  Height = 16
  Radius = 2.15
FEATURE [Part::MultiFuse] Fusion001089102007007003008034028016007006009018009018  label="M4nut042"
  Placement = pos=(10,0,42) rot=(0,-1,0;1.5708rad)
  Shapes = -> [Cylinder014005962027,prism018]
FEATURE [Part::Refine] Fusion001089102007007003008034028016007006009018009019  label="M4nut043"
  Placement = pos=(0,10,0) rot=(0,0,1;0rad)
  Source = -> Fusion001089102007007003008034028016007006009018009018
FEATURE [Part::Refine] Fusion001089102007007003008034028016007006009018009020  label="M4nut044"
  Placement = pos=(0,-10,0) rot=(0,0,1;0rad)
  Source = -> Fusion001089102007007003008034028016007006009018009018
FEATURE [Part::Refine] Fusion001089102007007003008034028016007006009018009021  label="M4nut045"
  Placement = pos=(0,0,25) rot=(0,0,1;0rad)
  Source = -> Fusion001089102007007003008034028016007006009018009018
FEATURE [Part::Refine] Fusion001089102007007003008034028016007006009018009022  label="M4nut046"
  Placement = pos=(0,0,-25) rot=(0,0,1;0rad)
  Source = -> Fusion001089102007007003008034028016007006009018009018
FEATURE [Part::MultiFuse] Fusion001089102007007003008034028016003
  Shapes = -> [Cylinder014005931,Cylinder014005932,Cylinder014005933,Cylinder014005934,Cylinder014005935,Cylinder014005936,Cylinder014005937,Cylinder014005938,Cylinder014005939,Cylinder014005940,Cylinder014005941,Cylinder014005942,Fusion001089102007007003008034028016004,Fusion001089102007007003008034028016007006009018009019,Fusion001089102007007003008034028016007006009018009020,+2 more]
FEATURE [Part::Cut] Cut009003003009003003003007003002  label="ListaDee"
  Base = -> Fusion001089102007007003008034028016002
  Placement = pos=(0,0,0) rot=(1,0,0;1.5708rad)
  Tool = -> Fusion001089102007007003008034028016003
FEATURE [Part::Refine] Cut009003003009003003003007003002001  label="ListaDee001"
  Source = -> Cut009003003009003003003007003002
FEATURE [Part::Chamfer] Chamfer017  label="ListaDE"
  Base = -> Cut009003003009003003003007003002001
  Edges = 20 edges r=1: [Edge2,Edge4,Edge5,Edge6,Edge7,Edge8,Edge9,Edge10,Edge11,Edge12,Edge14,Edge15,Edge17,Edge18,Edge19,Edge20,Edge21,Edge22,Edge23,Edge24]
  Placement = pos=(0,0,0) rot=(-1,0,0;1.5708rad)
FEATURE [Part::Cylinder] cylinder010
  Angle = 360
  AttacherType = Attacher::AttachEngine3D
  Height = 14
  Radius = 3
FEATURE [Part::Cylinder] cylinder015
  Angle = 360
  AttacherType = Attacher::AttachEngine3D
  Height = 14
  Placement = pos=(-25,0,0) rot=(0,0,1;0rad)
  Radius = 2.6
FEATURE [Part::Cylinder] cylinder016
  Angle = 360
  AttacherType = Attacher::AttachEngine3D
  Height = 14
  Placement = pos=(25,0,0) rot=(0,0,1;0rad)
  Radius = 2.65
FEATURE [Part::Cylinder] Cylinder014005962028  label="Válec900"
  Angle = 360
  AttacherType = Attacher::AttachEngine3D
  Height = 14
  Radius = 35
FEATURE [Part::Prism] Prism011  label="Hranol011"
  AttacherType = Attacher::AttachEngine3D
  Circumradius = 7.5
  FirstAngle = 0
  Height = 6.5
  Placement = pos=(0,-17,0) rot=(0,0,1;0rad)
  Polygon = 6
  SecondAngle = 0
FEATURE [Part::Cylinder] Cylinder057  label="Válec055"
  Angle = 360
  AttacherType = Attacher::AttachEngine3D
  Height = 20
  Placement = pos=(0,-17,0) rot=(0,0,1;0rad)
  Radius = 4.16
FEATURE [Part::Cylinder] Cylinder058  label="Válec056"
  Angle = 360
  AttacherType = Attacher::AttachEngine3D
  Height = 20
  Placement = pos=(0,17,0) rot=(0,0,1;0rad)
  Radius = 4.16
FEATURE [Part::Prism] Prism012  label="Hranol012"
  AttacherType = Attacher::AttachEngine3D
  Circumradius = 7.5
  FirstAngle = 0
  Height = 6.5
  Placement = pos=(0,17,0) rot=(0,0,1;0rad)
  Polygon = 6
  SecondAngle = 0
FEATURE [Part::MultiFuse] Fusion027
  Shapes = -> [Prism011,Cylinder057,Cylinder058,Prism012]
FEATURE [Part::Cylinder] Cylinder014005962029  label="Válec901"
  Angle = 360
  AttacherType = Attacher::AttachEngine3D
  Height = 5.5
  Placement = pos=(25,0,8.5) rot=(0,0,1;0rad)
  Radius = 4.25
FEATURE [Part::Cylinder] Cylinder014005962030  label="Válec902"
  Angle = 360
  AttacherType = Attacher::AttachEngine3D
  Height = 5.5
  Placement = pos=(-25,0,8.5) rot=(0,0,1;0rad)
  Radius = 4.25
FEATURE [Part::MultiFuse] union002
  Shapes = -> [cylinder010,cylinder015,cylinder016,Fusion027,Cylinder014005962029,Cylinder014005962030]
FEATURE [Part::Cut] Cut009003003009003003003007003002006005  label="H006"
  Base = -> Cylinder014005962028
  Tool = -> union002
FEATURE [Part::Chamfer] Chamfer022  label="Vixen"
  Base = -> Cut009003003009003003003007003002006005
  Edges = 2 edges r=1.5: [Edge1,Edge3]
FEATURE [Part::Cylinder] Cylinder014005962031  label="Válec903"
  Angle = 360
  AttacherType = Attacher::AttachEngine3D
  Height = 10
  Placement = pos=(0,0,20) rot=(0,0,1;0rad)
  Radius = 40
FEATURE [Part::Cylinder] Cylinder012  label="Válec908"
  Angle = 360
  AttacherType = Attacher::AttachEngine3D
  Height = 10
  Placement = pos=(0,0,20) rot=(0,0,1;0rad)
  Radius = 40
FEATURE [Part::Cylinder] Cylinder015  label="Válec913"
  Angle = 360
  AttacherType = Attacher::AttachEngine3D
  Height = 10
  Placement = pos=(-52,0,6) rot=(0,1,0;1.5708rad)
  Radius = 1.4
FEATURE [Part::Cylinder] Cylinder014  label="Válec915"
  Angle = 360
  AttacherType = Attacher::AttachEngine3D
  Height = 6
  Placement = pos=(-51,0,6) rot=(0,1,0;1.5708rad)
  Radius = 6
FEATURE [Part::Refine] Cylinder014001  label="Válec911"
  Placement = pos=(0,0,0) rot=(0,0,1;2.0944rad)
  Source = -> Cylinder014
FEATURE [Part::Refine] Cylinder014002  label="Válec914"
  Placement = pos=(0,0,0) rot=(0,0,-1;2.0944rad)
  Source = -> Cylinder014
FEATURE [Part::Cylinder] Cylinder008  label="Válec917"
  Angle = 360
  AttacherType = Attacher::AttachEngine3D
  Height = 2
  Placement = pos=(0,0,12) rot=(0,0,1;0rad)
  Radius = 41.5
FEATURE [Part::Cylinder] Cylinder007  label="Válec918"
  Angle = 360
  AttacherType = Attacher::AttachEngine3D
  Height = 12
  Radius = 44.5
FEATURE [Part::Cylinder] Cylinder011  label="Válec919"
  Angle = 360
  AttacherType = Attacher::AttachEngine3D
  Height = 40
  Radius = 13
FEATURE [Part::MultiFuse] Fusion005
  Shapes = -> [Cylinder011,Cylinder012]
FEATURE [Part::Cylinder] Cylinder009  label="Válec921"
  Angle = 360
  AttacherType = Attacher::AttachEngine3D
  Height = 2
  Placement = pos=(0,0,12.5) rot=(0,0,1;0rad)
  Radius = 30
FEATURE [Part::Cylinder] Cylinder006  label="Válec922"
  Angle = 360
  AttacherType = Attacher::AttachEngine3D
  Height = 30
  Radius = 49.5
FEATURE [Part::Box] Box021010  label="Krychle124"
  AttacherType = Attacher::AttachEngine3D
  Height = 12
  Length = 12
  Placement = pos=(38,-15,0) rot=(0,0,1;0rad)
  Width = 30
FEATURE [Part::Refine] Box002002  label="Krychle119"
  Placement = pos=(0,0,0) rot=(0,0,-1;2.0944rad)
  Source = -> Box021010
FEATURE [Part::Refine] Box002001  label="Krychle123"
  Placement = pos=(0,0,0) rot=(0,0,1;2.0944rad)
  Source = -> Box021010
FEATURE [Part::MultiFuse] Fusion001089102007007003008034028016007006009018009024
  Shapes = -> [Box021010,Cylinder007,Box002001,Box002002,Cylinder008]
FEATURE [Part::Cut] Cut009003003009003003003007003002006006
  Base = -> Cylinder006
  Tool = -> Fusion001089102007007003008034028016007006009018009024
FEATURE [Part::MultiFuse] Fusion001089102007007003008034028016007006009018009023
  Shapes = -> [Cut009003003009003003003007003002006006,Cylinder009]
FEATURE [Part::Cut] Cut009003003009003003003007003002006007
  Base = -> Fusion001089102007007003008034028016007006009018009023
  Tool = -> Fusion005
FEATURE [Part::MultiFuse] Fusion006
  Shapes = -> [Cut009003003009003003003007003002006007,Cylinder014,Cylinder014002,Cylinder014001]
FEATURE [Part::Cylinder] Cylinder014005962032  label="Válec923"
  Angle = 360
  AttacherType = Attacher::AttachEngine3D
  Height = 10
  Placement = pos=(0,0,30) rot=(0,0,1;0rad)
  Radius = 49.5
FEATURE [Part::Cylinder] Cylinder014005962033  label="Válec924"
  Angle = 360
  AttacherType = Attacher::AttachEngine3D
  Height = 15
  Radius = 3.15
FEATURE [Part::Cylinder] Cylinder014005962034  label="Válec925"
  Angle = 360
  AttacherType = Attacher::AttachEngine3D
  Height = 6
  Radius = 5
FEATURE [Part::MultiFuse] Fusion001089102007007003008034028016007006009018009025  label="M6"
  Placement = pos=(0,0,30) rot=(0,0,1;0rad)
  Shapes = -> [Cylinder014005962033,Cylinder014005962034]
FEATURE [Part::Refine] Fusion001089102007007003008034028016007006009018009025001  label="M017"
  Placement = pos=(0,-32.5,0) rot=(0,0,1;0rad)
  Source = -> Fusion001089102007007003008034028016007006009018009025
FEATURE [Part::Refine] Fusion001089102007007003008034028016007006009018009025002  label="M018"
  Placement = pos=(0,32.5,0) rot=(0,0,1;0rad)
  Source = -> Fusion001089102007007003008034028016007006009018009025
FEATURE [Part::Cylinder] Cylinder014005962035  label="Válec926"
  Angle = 360
  AttacherType = Attacher::AttachEngine3D
  Height = 4
  Radius = 12
FEATURE [Part::Cylinder] Cylinder014005962036  label="Válec927"
  Angle = 360
  AttacherType = Attacher::AttachEngine3D
  Height = 15
  Radius = 5
FEATURE [Part::MultiFuse] Fusion001089102007007003008034028016007006009018009025003  label="Foto "
  Placement = pos=(0,0,30) rot=(0,0,1;0rad)
  Shapes = -> [Cylinder014005962036,Cylinder014005962035]
FEATURE [Part::Cylinder] Cylinder014005962037  label="Válec928"
  Angle = 360
  AttacherType = Attacher::AttachEngine3D
  Height = 20
  Placement = pos=(0,0,20) rot=(0,0,1;0rad)
  Radius = 2.16
FEATURE [Part::Prism] Prism013  label="Hranol013"
  AttacherType = Attacher::AttachEngine3D
  Circumradius = 4
  FirstAngle = 0
  Height = 4.5
  Placement = pos=(0,0,35.5) rot=(0,0,1;0rad)
  Polygon = 6
  SecondAngle = 0
FEATURE [Part::Cylinder] Cylinder014005962038  label="Válec929"
  Angle = 360
  AttacherType = Attacher::AttachEngine3D
  Height = 4.1
  Placement = pos=(0,0,20) rot=(0,0,1;0rad)
  Radius = 3.6
FEATURE [Part::MultiFuse] Fusion001089102007007003008034028016007006009018009025004  label="M4i"
  Placement = pos=(30,0,0) rot=(0,0,1;0rad)
  Shapes = -> [Cylinder014005962038,Cylinder014005962037,Prism013]
FEATURE [Part::Refine] Fusion001089102007007003008034028016007006009018009025004001  label="M4i001"
  Placement = pos=(0,0,0) rot=(0,0,1;1.0472rad)
  Source = -> Fusion001089102007007003008034028016007006009018009025004
FEATURE [Part::Refine] Fusion001089102007007003008034028016007006009018009025004002  label="M4i002"
  Placement = pos=(0,0,0) rot=(0,0,1;2.0944rad)
  Source = -> Fusion001089102007007003008034028016007006009018009025004
FEATURE [Part::Refine] Fusion001089102007007003008034028016007006009018009025004003  label="M4i003"
  Placement = pos=(0,0,0) rot=(0,0,1;3.14159rad)
  Source = -> Fusion001089102007007003008034028016007006009018009025004
FEATURE [Part::Refine] Fusion001089102007007003008034028016007006009018009025004004  label="M4i004"
  Placement = pos=(0,0,0) rot=(0,0,1;4.18879rad)
  Source = -> Fusion001089102007007003008034028016007006009018009025004
FEATURE [Part::Refine] Fusion001089102007007003008034028016007006009018009025004005  label="M4i005"
  Placement = pos=(0,0,0) rot=(0,0,-1;1.0472rad)
  Source = -> Fusion001089102007007003008034028016007006009018009025004
FEATURE [Part::MultiFuse] Fusion001089102007007003008034028016007006009018009025004006  label="Srouby001"
  Shapes = -> [Fusion001089102007007003008034028016007006009018009025004,Fusion001089102007007003008034028016007006009018009025004001,Fusion001089102007007003008034028016007006009018009025004002,Fusion001089102007007003008034028016007006009018009025004003,Fusion001089102007007003008034028016007006009018009025004004,Fusion001089102007007003008034028016007006009018009025004005]
FEATURE [Part::Cylinder] Cylinder014005962039  label="Válec930"
  Angle = 360
  AttacherType = Attacher::AttachEngine3D
  Height = 25
  Placement = pos=(0,43.5,20) rot=(0,0,1;0rad)
  Radius = 1.65
FEATURE [Part::Prism] Prism014  label="Hranol014"
  AttacherType = Attacher::AttachEngine3D
  Circumradius = 3.2
  FirstAngle = 0
  Height = 2.5
  Placement = pos=(0,0,23) rot=(0,0,1;0.523599rad)
  Polygon = 6
  SecondAngle = 0
FEATURE [Part::Box] Box021011  label="Krychle125"
  AttacherType = Attacher::AttachEngine3D
  Height = 3.5
  Length = 5.5
  Placement = pos=(-2.75,-10,23) rot=(0,0,1;0rad)
  Width = 10
FEATURE [Part::MultiFuse] Fusion001089102007007003008034028016007006009018009025004007002  label="Matk4"
  Placement = pos=(0,43.5,0) rot=(0,0,1;0rad)
  Shapes = -> [Box021011,Prism014]
FEATURE [Part::Cylinder] Cylinder014005962040  label="Válec931"
  Angle = 360
  AttacherType = Attacher::AttachEngine3D
  Height = 3
  Placement = pos=(0,43.5,36) rot=(0,0,1;0rad)
  Radius = 3.3
FEATURE [Part::MultiFuse] Fusion001089102007007003008034028016007006009018009025004007003  label="S2"
  Placement = pos=(0,0,0) rot=(0,0,1;1.0472rad)
  Shapes = -> [Cylinder014005962039,Fusion001089102007007003008034028016007006009018009025004007002,Cylinder014005962040]
FEATURE [Part::Refine] Fusion001089102007007003008034028016007006009018009025004007003001  label="S003"
  Placement = pos=(0,0,0) rot=(0,0,1;1.0472rad)
  Source = -> Fusion001089102007007003008034028016007006009018009025004007003
FEATURE [Part::Refine] Fusion001089102007007003008034028016007006009018009025004007003002  label="S004"
  Placement = pos=(0,0,0) rot=(0,0,1;3.14159rad)
  Source = -> Fusion001089102007007003008034028016007006009018009025004007003
FEATURE [Part::Refine] Fusion001089102007007003008034028016007006009018009025004007003003  label="S005"
  Placement = pos=(0,0,0) rot=(0,0,-1;2.0944rad)
  Source = -> Fusion001089102007007003008034028016007006009018009025004007003
FEATURE [Part::MultiFuse] Fusion001089102007007003008034028016007006009018009025004007003004  label="S006"
  Shapes = -> [Fusion001089102007007003008034028016007006009018009025004007003,Fusion001089102007007003008034028016007006009018009025004007003001,Fusion001089102007007003008034028016007006009018009025004007003002,Fusion001089102007007003008034028016007006009018009025004007003003]
FEATURE [Part::MultiFuse] Fusion001089102007007003008034028016007006009018009025004007  label="Sr"
  Shapes = -> [Fusion001089102007007003008034028016007006009018009025001,Fusion001089102007007003008034028016007006009018009025002,Fusion001089102007007003008034028016007006009018009025003,Fusion001089102007007003008034028016007006009018009025004006,Fusion001089102007007003008034028016007006009018009025004007003004]
FEATURE [Part::Cut] Cut009003003009003003003007003002006009  label="Vrchni"
  Base = -> Cylinder014005962032
  Tool = -> Fusion001089102007007003008034028016007006009018009025004007
FEATURE [Part::Refine] Fusion001089102007007003008034028016007006009018009025004007003004001  label="S007"
  Source = -> Fusion001089102007007003008034028016007006009018009025004007003004
FEATURE [Part::Prism] Prism015  label="Hranol015"
  AttacherType = Attacher::AttachEngine3D
  Circumradius = 3.2
  FirstAngle = 0
  Height = 2.4
  Placement = pos=(-46.82,0,6) rot=(0,1,0;1.5708rad)
  Polygon = 6
  SecondAngle = 0
FEATURE [Part::MultiFuse] Fusion008
  Shapes = -> [Cylinder015,Prism015]
FEATURE [Part::Refine] Fusion008002
  Placement = pos=(0,0,0) rot=(0,0,-1;2.0944rad)
  Source = -> Fusion008
FEATURE [Part::Refine] Fusion008001
  Placement = pos=(0,0,0) rot=(0,0,1;2.0944rad)
  Source = -> Fusion008
FEATURE [Part::MultiFuse] Fusion007
  Shapes = -> [Fusion008,Fusion008001,Fusion008002,Fusion001089102007007003008034028016007006009018009025004007003004001]
FEATURE [Part::Cut] Cut009003003009003003003007003002006008  label="spodni"
  Base = -> Fusion006
  Tool = -> Fusion007
FEATURE [Part::Cylinder] Cylinder014005962041  label="Válec932"
  Angle = 360
  AttacherType = Attacher::AttachEngine3D
  Height = 30
  Radius = 13.5
FEATURE [Part::MultiFuse] Fusion001089102007007003008034028016007006009018009025004007003004002  label="str"
  Shapes = -> [Cylinder014005962041,Cylinder014005962031]
FEATURE [Part::Cylinder] Cylinder014005962042  label="Válec933"
  Angle = 360
  AttacherType = Attacher::AttachEngine3D
  Height = 30
  Radius = 6.15
FEATURE [Part::Prism] Prism016  label="Hranol016"
  AttacherType = Attacher::AttachEngine3D
  Circumradius = 11.2
  FirstAngle = 0
  Height = 8.2
  Placement = pos=(0,0,21.8) rot=(0,0,1;0rad)
  Polygon = 6
  SecondAngle = 0
FEATURE [Part::Refine] Fusion001089102007007003008034028016007006009018009025004006001  label="Srouby002"
  Source = -> Fusion001089102007007003008034028016007006009018009025004006
FEATURE [Part::MultiFuse] Fusion001089102007007003008034028016007006009018009025004007003004003
  Shapes = -> [Cylinder014005962042,Prism016,Fusion001089102007007003008034028016007006009018009025004006001]
FEATURE [Part::Cut] Cut009003003009003003003007003002006010  label="stred"
  Base = -> Fusion001089102007007003008034028016007006009018009025004007003004002
  Tool = -> Fusion001089102007007003008034028016007006009018009025004007003004003
FEATURE [Part::Chamfer] Chamfer023  label="stred001"
  Base = -> Cut009003003009003003003007003002006010
  Edges = 3 edges r=1: [Edge8,Edge28,Edge62]
  Placement = pos=(0,0,25) rot=(0,0,1;0rad)
FEATURE [Part::Chamfer] Chamfer024  label="Vrchni001"
  Base = -> Cut009003003009003003003007003002006009
  Edges = 2 edges r=1: [Edge1,Edge3]
  Placement = pos=(0,0,25) rot=(0,0,1;0rad)
FEATURE [Part::Chamfer] Chamfer025  label="spodni001"
  Base = -> Cut009003003009003003003007003002006008
  Edges = 1 edges r=1: [Edge21]
FEATURE [Part::Box] cube004
  AttacherType = Attacher::AttachEngine3D
  Height = 10
  Length = 84
  Placement = pos=(0,-19,0) rot=(0,0,1;0rad)
  Width = 38
FEATURE [Part::Box] cube005
  AttacherType = Attacher::AttachEngine3D
  Height = 10
  Length = 115.1
  Placement = pos=(-0.01,16,5) rot=(-1,0,0;0.785398rad)
  Width = 10
FEATURE [Part::Box] cube006
  AttacherType = Attacher::AttachEngine3D
  Height = 10
  Length = 115.1
  Placement = pos=(-0.01,-16,5) rot=(1,0,0;2.35619rad)
  Width = 10
FEATURE [Part::Fuse] union003
  Base = -> cube005
  Tool = -> cube006
FEATURE [Part::Cut] difference001
  Base = -> cube004
  Placement = pos=(-10,0,83) rot=(0,1,0;1.5708rad)
  Tool = -> union003
FEATURE [Part::Box] cube007
  AttacherType = Attacher::AttachEngine3D
  Height = 10
  Length = 115
  Placement = pos=(-1.5,-19,99) rot=(0,1,0;1.5708rad)
  Width = 38
FEATURE [Part::Cut] Cut009003003009003003003007003002006011  label="lISTA x001"
  Base = -> difference001
  Tool = -> cube007
FEATURE [Part::Cylinder] Cylinder014005962043  label="Válec934"
  Angle = 360
  AttacherType = Attacher::AttachEngine3D
  Height = 16
  Radius = 2.15
FEATURE [Part::Cylinder] Cylinder014005962044  label="Válec935"
  Angle = 360
  AttacherType = Attacher::AttachEngine3D
  Height = 4
  Placement = pos=(0,0,16) rot=(0,0,1;0rad)
  Radius = 3.5
FEATURE [Part::MultiFuse] Fusion001089102007007003008034028016007006009018009025004007003004004  label="M4nut047"
  Placement = pos=(10,0,41.5) rot=(0,-1,0;1.5708rad)
  Shapes = -> [Cylinder014005962043,Cylinder014005962044]
FEATURE [Part::Refine] Fusion001089102007007003008034028016007006009018009025004007003004005  label="M4nut048"
  Placement = pos=(0,10,0) rot=(0,0,1;0rad)
  Source = -> Fusion001089102007007003008034028016007006009018009025004007003004004
FEATURE [Part::Refine] Fusion001089102007007003008034028016007006009018009025004007003004006  label="M4nut049"
  Placement = pos=(0,-10,0) rot=(0,0,1;0rad)
  Source = -> Fusion001089102007007003008034028016007006009018009025004007003004004
FEATURE [Part::Refine] Fusion001089102007007003008034028016007006009018009025004007003004007  label="M4nut050"
  Placement = pos=(0,0,25) rot=(0,0,1;0rad)
  Source = -> Fusion001089102007007003008034028016007006009018009025004007003004004
FEATURE [Part::Refine] Fusion001089102007007003008034028016007006009018009025004007003004008  label="M4nut051"
  Placement = pos=(0,0,-25) rot=(0,0,1;0rad)
  Source = -> Fusion001089102007007003008034028016007006009018009025004007003004004
FEATURE [Part::MultiFuse] Fusion001089102007007003008034028016007006009018009025004007003004009
  Shapes = -> [Fusion001089102007007003008034028016007006009018009025004007003004005,Fusion001089102007007003008034028016007006009018009025004007003004006,Fusion001089102007007003008034028016007006009018009025004007003004007,Fusion001089102007007003008034028016007006009018009025004007003004008]
FEATURE [Part::Cut] Cut009003003009003003003007003002006012
  Base = -> Cut009003003009003003003007003002006011
  Tool = -> Fusion001089102007007003008034028016007006009018009025004007003004009
FEATURE [Part::Cylinder] Cylinder014005962045  label="Válec936"
  Angle = 360
  AttacherType = Attacher::AttachEngine3D
  Height = 3
  Placement = pos=(-12.5,0,4.5) rot=(0,1,0;1.5708rad)
  Radius = 5
FEATURE [Part::Cylinder] Cylinder014005962046  label="Válec937"
  Angle = 360
  AttacherType = Attacher::AttachEngine3D
  Height = 3
  Placement = pos=(-12.5,0,78.5) rot=(0,1,0;1.5708rad)
  Radius = 5
FEATURE [Part::MultiFuse] Fusion001089102007007003008034028016007006009018009025004007003004010  label="Liasa RA003"
  Shapes = -> [Cut009003003009003003003007003002006012,Cylinder014005962045,Cylinder014005962046]
FEATURE [Part::Cylinder] Cylinder014005962047  label="Válec938"
  Angle = 360
  AttacherType = Attacher::AttachEngine3D
  Height = 10
  Placement = pos=(0,0,20) rot=(0,0,1;0rad)
  Radius = 40
FEATURE [Part::Cylinder] Cylinder014005962049  label="Válec940"
  Angle = 360
  AttacherType = Attacher::AttachEngine3D
  Height = 10
  Placement = pos=(-52,0,6) rot=(0,1,0;1.5708rad)
  Radius = 1.4
FEATURE [Part::Cylinder] Cylinder014005962051  label="Válec942"
  Angle = 360
  AttacherType = Attacher::AttachEngine3D
  Height = 6
  Placement = pos=(-51,0,6) rot=(0,1,0;1.5708rad)
  Radius = 6
FEATURE [Part::Refine] Cylinder014005962048  label="Válec939"
  Placement = pos=(0,0,0) rot=(0,0,1;2.0944rad)
  Source = -> Cylinder014005962051
FEATURE [Part::Refine] Cylinder014005962050  label="Válec941"
  Placement = pos=(0,0,0) rot=(0,0,-1;2.0944rad)
  Source = -> Cylinder014005962051
FEATURE [Part::Cylinder] Cylinder014005962052  label="Válec943"
  Angle = 360
  AttacherType = Attacher::AttachEngine3D
  Height = 2
  Placement = pos=(0,0,12) rot=(0,0,1;0rad)
  Radius = 41.5
FEATURE [Part::Cylinder] Cylinder014005962053  label="Válec944"
  Angle = 360
  AttacherType = Attacher::AttachEngine3D
  Height = 12
  Radius = 44.5
FEATURE [Part::Cylinder] Cylinder014005962054  label="Válec945"
  Angle = 360
  AttacherType = Attacher::AttachEngine3D
  Height = 40
  Radius = 13
FEATURE [Part::MultiFuse] Fusion001089102007007003008034028016007006009018009025004007003004015
  Shapes = -> [Cylinder014005962054,Cylinder014005962047]
FEATURE [Part::Cylinder] Cylinder014005962055  label="Válec946"
  Angle = 360
  AttacherType = Attacher::AttachEngine3D
  Height = 2
  Placement = pos=(0,0,12.5) rot=(0,0,1;0rad)
  Radius = 30
FEATURE [Part::Cylinder] Cylinder014005962056  label="Válec947"
  Angle = 360
  AttacherType = Attacher::AttachEngine3D
  Height = 30
  Radius = 49.5
FEATURE [Part::Box] Box021014  label="Krychle128"
  AttacherType = Attacher::AttachEngine3D
  Height = 12
  Length = 12
  Placement = pos=(38,-15,0) rot=(0,0,1;0rad)
  Width = 30
FEATURE [Part::Refine] Box021012  label="Krychle126"
  Placement = pos=(0,0,0) rot=(0,0,-1;2.0944rad)
  Source = -> Box021014
FEATURE [Part::Refine] Box021013  label="Krychle127"
  Placement = pos=(0,0,0) rot=(0,0,1;2.0944rad)
  Source = -> Box021014
FEATURE [Part::MultiFuse] Fusion001089102007007003008034028016007006009018009025004007003004016
  Shapes = -> [Box021014,Cylinder014005962053,Box021013,Box021012,Cylinder014005962052]
FEATURE [Part::Cut] Cut009003003009003003003007003002006013
  Base = -> Cylinder014005962056
  Tool = -> Fusion001089102007007003008034028016007006009018009025004007003004016
FEATURE [Part::MultiFuse] Fusion001089102007007003008034028016007006009018009025004007003004013
  Shapes = -> [Cut009003003009003003003007003002006013,Cylinder014005962055]
FEATURE [Part::Cut] Cut009003003009003003003007003002006014
  Base = -> Fusion001089102007007003008034028016007006009018009025004007003004013
  Tool = -> Fusion001089102007007003008034028016007006009018009025004007003004015
FEATURE [Part::MultiFuse] Fusion001089102007007003008034028016007006009018009025004007003004017
  Shapes = -> [Cut009003003009003003003007003002006014,Cylinder014005962051,Cylinder014005962050,Cylinder014005962048]
FEATURE [Part::Cylinder] Cylinder014005962057  label="Válec948"
  Angle = 360
  AttacherType = Attacher::AttachEngine3D
  Height = 25
  Placement = pos=(0,43.5,20) rot=(0,0,1;0rad)
  Radius = 1.65
FEATURE [Part::Prism] Prism017  label="Hranol017"
  AttacherType = Attacher::AttachEngine3D
  Circumradius = 3.2
  FirstAngle = 0
  Height = 2.5
  Placement = pos=(0,0,23) rot=(0,0,1;0.523599rad)
  Polygon = 6
  SecondAngle = 0
FEATURE [Part::Box] Box021015  label="Krychle129"
  AttacherType = Attacher::AttachEngine3D
  Height = 2.5
  Length = 5.5
  Placement = pos=(-2.75,-10,23) rot=(0,0,1;0rad)
  Width = 10
FEATURE [Part::MultiFuse] Fusion001089102007007003008034028016007006009018009025004007003004019  label="Matk005"
  Placement = pos=(0,43.5,0) rot=(0,0,1;0rad)
  Shapes = -> [Box021015,Prism017]
FEATURE [Part::Cylinder] Cylinder014005962058  label="Válec949"
  Angle = 360
  AttacherType = Attacher::AttachEngine3D
  Height = 4
  Placement = pos=(0,43.5,36) rot=(0,0,1;0rad)
  Radius = 3.5
FEATURE [Part::MultiFuse] Fusion001089102007007003008034028016007006009018009025004007003004020  label="S008"
  Placement = pos=(0,0,0) rot=(0,0,1;1.0472rad)
  Shapes = -> [Cylinder014005962057,Fusion001089102007007003008034028016007006009018009025004007003004019,Cylinder014005962058]
FEATURE [Part::Refine] Fusion001089102007007003008034028016007006009018009025004007003004021  label="S009"
  Placement = pos=(0,0,0) rot=(0,0,1;1.0472rad)
  Source = -> Fusion001089102007007003008034028016007006009018009025004007003004020
FEATURE [Part::Refine] Fusion001089102007007003008034028016007006009018009025004007003004022  label="S010"
  Placement = pos=(0,0,0) rot=(0,0,1;3.14159rad)
  Source = -> Fusion001089102007007003008034028016007006009018009025004007003004020
FEATURE [Part::Refine] Fusion001089102007007003008034028016007006009018009025004007003004023  label="S011"
  Placement = pos=(0,0,0) rot=(0,0,-1;2.0944rad)
  Source = -> Fusion001089102007007003008034028016007006009018009025004007003004020
FEATURE [Part::MultiFuse] Fusion001089102007007003008034028016007006009018009025004007003004024  label="S012"
  Shapes = -> [Fusion001089102007007003008034028016007006009018009025004007003004020,Fusion001089102007007003008034028016007006009018009025004007003004021,Fusion001089102007007003008034028016007006009018009025004007003004022,Fusion001089102007007003008034028016007006009018009025004007003004023]
FEATURE [Part::Refine] Fusion001089102007007003008034028016007006009018009025004007003004025  label="S013"
  Source = -> Fusion001089102007007003008034028016007006009018009025004007003004024
FEATURE [Part::Prism] Prism018  label="Hranol018"
  AttacherType = Attacher::AttachEngine3D
  Circumradius = 3.2
  FirstAngle = 0
  Height = 2.4
  Placement = pos=(-46.82,0,6) rot=(0,1,0;1.5708rad)
  Polygon = 6
  SecondAngle = 0
FEATURE [Part::MultiFuse] Fusion001089102007007003008034028016007006009018009025004007003004011
  Shapes = -> [Cylinder014005962049,Prism018]
FEATURE [Part::Refine] Fusion001089102007007003008034028016007006009018009025004007003004012
  Placement = pos=(0,0,0) rot=(0,0,-1;2.0944rad)
  Source = -> Fusion001089102007007003008034028016007006009018009025004007003004011
FEATURE [Part::Refine] Fusion001089102007007003008034028016007006009018009025004007003004018
  Placement = pos=(0,0,0) rot=(0,0,1;2.0944rad)
  Source = -> Fusion001089102007007003008034028016007006009018009025004007003004011
FEATURE [Part::MultiFuse] Fusion001089102007007003008034028016007006009018009025004007003004014
  Shapes = -> [Fusion001089102007007003008034028016007006009018009025004007003004011,Fusion001089102007007003008034028016007006009018009025004007003004018,Fusion001089102007007003008034028016007006009018009025004007003004012,Fusion001089102007007003008034028016007006009018009025004007003004025]
FEATURE [Part::Cut] Cut009003003009003003003007003002006015  label="spodni002"
  Base = -> Fusion001089102007007003008034028016007006009018009025004007003004017
  Tool = -> Fusion001089102007007003008034028016007006009018009025004007003004014
FEATURE [Part::Chamfer] Chamfer026  label="spodni003"
  Base = -> Cut009003003009003003003007003002006015
  Edges = 1 edges r=1: [Edge21]
FEATURE [Part::Cylinder] Cylinder014005962059  label="Válec950"
  Angle = 360
  AttacherType = Attacher::AttachEngine3D
  Height = 27
  Placement = pos=(0,0,28) rot=(0,0,1;0rad)
  Radius = 40.3
FEATURE [Part::Cylinder] Cylinder014005962061  label="Válec952"
  Angle = 360
  AttacherType = Attacher::AttachEngine3D
  Height = 10
  Placement = pos=(-52,0,6) rot=(0,1,0;1.5708rad)
  Radius = 1.4
FEATURE [Part::Cylinder] Cylinder014005962065  label="Válec956"
  Angle = 360
  AttacherType = Attacher::AttachEngine3D
  Height = 6
  Radius = 29
FEATURE [Part::Cylinder] Cylinder014005962066  label="Válec957"
  Angle = 360
  AttacherType = Attacher::AttachEngine3D
  Height = 45
  Radius = 16.5
FEATURE [Part::MultiFuse] Fusion001089102007007003008034028016007006009018009025004007003004030
  Shapes = -> [Cylinder014005962066,Cylinder014005962059]
FEATURE [Part::Cylinder] Cylinder014005962068  label="Válec959"
  Angle = 360
  AttacherType = Attacher::AttachEngine3D
  Height = 55
  Radius = 49
FEATURE [Part::Box] Box021018  label="Krychle132"
  AttacherType = Attacher::AttachEngine3D
  Height = 15
  Length = 30
  Placement = pos=(24,-15.5,0) rot=(0,0,1;0rad)
  Width = 31
FEATURE [Part::Refine] Box021016  label="Krychle130"
  Placement = pos=(0,0,0) rot=(0,0,-1;2.0944rad)
  Source = -> Box021018
FEATURE [Part::Refine] Box021017  label="Krychle131"
  Placement = pos=(0,0,0) rot=(0,0,1;2.0944rad)
  Source = -> Box021018
FEATURE [Part::Cylinder] Cylinder014005962069  label="Válec960"
  Angle = 360
  AttacherType = Attacher::AttachEngine3D
  Height = 30
  Placement = pos=(0,43.5,10) rot=(0,0,1;0rad)
  Radius = 1.75
FEATURE [Part::Prism] Prism019  label="Hranol019"
  AttacherType = Attacher::AttachEngine3D
  Circumradius = 3.2
  FirstAngle = 0
  Height = 2.5
  Placement = pos=(0,0,23) rot=(0,0,1;0.523599rad)
  Polygon = 6
  SecondAngle = 0
FEATURE [Part::Box] Box021019  label="Krychle133"
  AttacherType = Attacher::AttachEngine3D
  Height = 2.5
  Length = 5.5
  Placement = pos=(-2.75,-10,23) rot=(0,0,1;0rad)
  Width = 10
FEATURE [Part::MultiFuse] Fusion001089102007007003008034028016007006009018009025004007003004034  label="Matk006"
  Placement = pos=(0,43.5,0) rot=(0,0,1;0rad)
  Shapes = -> [Box021019,Prism019]
FEATURE [Part::Cylinder] Cylinder014005962070  label="Válec961"
  Angle = 360
  AttacherType = Attacher::AttachEngine3D
  Height = 4
  Placement = pos=(0,43.5,36) rot=(0,0,1;0rad)
  Radius = 3.5
FEATURE [Part::MultiFuse] Fusion001089102007007003008034028016007006009018009025004007003004035  label="S014"
  Placement = pos=(0,0,0) rot=(0,0,1;1.0472rad)
  Shapes = -> [Cylinder014005962069,Fusion001089102007007003008034028016007006009018009025004007003004034,Cylinder014005962070]
FEATURE [Part::Refine] Fusion001089102007007003008034028016007006009018009025004007003004036  label="S015"
  Placement = pos=(0,0,0) rot=(0,0,1;1.0472rad)
  Source = -> Fusion001089102007007003008034028016007006009018009025004007003004035
FEATURE [Part::Refine] Fusion001089102007007003008034028016007006009018009025004007003004037  label="S016"
  Placement = pos=(0,0,0) rot=(0,0,1;3.14159rad)
  Source = -> Fusion001089102007007003008034028016007006009018009025004007003004035
FEATURE [Part::Refine] Fusion001089102007007003008034028016007006009018009025004007003004038  label="S017"
  Placement = pos=(0,0,0) rot=(0,0,-1;2.0944rad)
  Source = -> Fusion001089102007007003008034028016007006009018009025004007003004035
FEATURE [Part::MultiFuse] Fusion001089102007007003008034028016007006009018009025004007003004039  label="S018"
  Placement = pos=(0,0,24) rot=(0,0,1;0rad)
  Shapes = -> [Fusion001089102007007003008034028016007006009018009025004007003004035,Fusion001089102007007003008034028016007006009018009025004007003004036,Fusion001089102007007003008034028016007006009018009025004007003004037,Fusion001089102007007003008034028016007006009018009025004007003004038]
FEATURE [Part::MultiFuse] Fusion001089102007007003008034028016007006009018009025004007003004031
  Shapes = -> [Box021018,Cylinder014005962065,Box021017,Box021016,Fusion001089102007007003008034028016007006009018009025004007003004030,Fusion001089102007007003008034028016007006009018009025004007003004039]
FEATURE [Part::Cut] Cut009003003009003003003007003002006016  label="Zomei"
  Base = -> Cylinder014005962068
  Tool = -> Fusion001089102007007003008034028016007006009018009025004007003004031
FEATURE [Part::Refine] Fusion001089102007007003008034028016007006009018009025004007003004040  label="S019"
  Source = -> Fusion001089102007007003008034028016007006009018009025004007003004039
FEATURE [Part::Prism] Prism020  label="Hranol020"
  AttacherType = Attacher::AttachEngine3D
  Circumradius = 3.2
  FirstAngle = 0
  Height = 2.4
  Placement = pos=(-46.82,0,6) rot=(0,1,0;1.5708rad)
  Polygon = 6
  SecondAngle = 0
FEATURE [Part::MultiFuse] Fusion001089102007007003008034028016007006009018009025004007003004026  label="DIsp"
  Shapes = -> [Cylinder014005962061,Prism020]
FEATURE [Part::Refine] Fusion001089102007007003008034028016007006009018009025004007003004027
  Placement = pos=(0,0,0) rot=(0,0,-1;2.0944rad)
  Source = -> Fusion001089102007007003008034028016007006009018009025004007003004026
FEATURE [Part::Refine] Fusion001089102007007003008034028016007006009018009025004007003004033
  Placement = pos=(0,0,0) rot=(0,0,1;2.0944rad)
  Source = -> Fusion001089102007007003008034028016007006009018009025004007003004026
FEATURE [Part::MultiFuse] Fusion001089102007007003008034028016007006009018009025004007003004029  label="  dirsp"
  Shapes = -> [Fusion001089102007007003008034028016007006009018009025004007003004026,Fusion001089102007007003008034028016007006009018009025004007003004033,Fusion001089102007007003008034028016007006009018009025004007003004027,Fusion001089102007007003008034028016007006009018009025004007003004040]
FEATURE [Part::Chamfer] Chamfer027  label="Zomey"
  Base = -> Cut009003003009003003003007003002006016
  Edges = 14 edges r=1: [Edge4,Edge8,Edge12,Edge15,Edge19,Edge23,Edge24,Edge31,Edge35,Edge36,Edge43,Edge47,Edge48,Edge55]
FEATURE [Part::Cylinder] cylinder017
  Angle = 360
  AttacherType = Attacher::AttachEngine3D
  Height = 10
  Radius = 3
FEATURE [Part::Cylinder] cylinder018
  Angle = 360
  AttacherType = Attacher::AttachEngine3D
  Height = 10
  Placement = pos=(15,0,0) rot=(0,0,1;0rad)
  Radius = 3.5
FEATURE [Part::Cylinder] cylinder019
  Angle = 360
  AttacherType = Attacher::AttachEngine3D
  Height = 5
  Placement = pos=(15,0,0) rot=(0,0,1;0rad)
  Radius = 7
FEATURE [Part::Cylinder] cylinder020
  Angle = 360
  AttacherType = Attacher::AttachEngine3D
  Height = 10
  Placement = pos=(-15,0,0) rot=(0,0,1;0rad)
  Radius = 3.5
FEATURE [Part::Cylinder] cylinder021
  Angle = 360
  AttacherType = Attacher::AttachEngine3D
  Height = 5
  Placement = pos=(-15,0,0) rot=(0,0,1;0rad)
  Radius = 7
FEATURE [Part::Cylinder] cylinder022
  Angle = 360
  AttacherType = Attacher::AttachEngine3D
  Height = 10
  Placement = pos=(-25,0,0) rot=(0,0,1;0rad)
  Radius = 2.6
FEATURE [Part::Cylinder] cylinder023
  Angle = 360
  AttacherType = Attacher::AttachEngine3D
  Height = 10
  Placement = pos=(25,0,0) rot=(0,0,1;0rad)
  Radius = 2.6
FEATURE [Part::MultiFuse] union004
  Shapes = -> [cylinder017,cylinder018,cylinder019,cylinder020,cylinder021,cylinder022,cylinder023]
FEATURE [Part::Cylinder] Cylinder014005962071  label="Válec962"
  Angle = 360
  AttacherType = Attacher::AttachEngine3D
  Height = 10
  Radius = 35
FEATURE [Part::Cut] Cut009003003009003003003007003002006017  label="H007"
  Base = -> Cylinder014005962071
  Placement = pos=(0,0,10) rot=(0,0,1;0rad)
  Tool = -> union004
FEATURE [Part::Chamfer] Chamfer028  label="HH003"
  Base = -> Cut009003003009003003003007003002006017
  Edges = 2 edges r=1: [Edge1,Edge3]
FEATURE [Part::Cylinder] Cylinder014005962079  label="Válec970"
  Angle = 360
  AttacherType = Attacher::AttachEngine3D
  Height = 10
  Placement = pos=(-9.9,9.9,0) rot=(0,0,1;0rad)
  Radius = 1.6
FEATURE [Part::Cylinder] Cylinder014005962080  label="Válec971"
  Angle = 360
  AttacherType = Attacher::AttachEngine3D
  Height = 10
  Placement = pos=(-9.9,-9.9,0) rot=(0,0,1;0rad)
  Radius = 1.6
FEATURE [Part::Cylinder] Cylinder014005962081  label="Válec972"
  Angle = 360
  AttacherType = Attacher::AttachEngine3D
  Height = 10
  Placement = pos=(9.9,-9.9,0) rot=(0,0,1;0rad)
  Radius = 1.6
FEATURE [Part::Cylinder] Cylinder014005962082  label="Válec973"
  Angle = 360
  AttacherType = Attacher::AttachEngine3D
  Height = 10
  Placement = pos=(9.9,9.9,0) rot=(0,0,1;0rad)
  Radius = 1.6
FEATURE [Part::MultiFuse] Fusion001089102007007003008034028016007006009018009025004007003004042  label="Diry PG004"
  Shapes = -> [Cylinder014005962079,Cylinder014005962082,Cylinder014005962080,Cylinder014005962081]
FEATURE [Part::Cylinder] Cylinder014005962083  label="Válec974"
  Angle = 360
  AttacherType = Attacher::AttachEngine3D
  Height = 3
  Placement = pos=(9.9,9.9,0) rot=(0,0,1;0rad)
  Radius = 2.8
FEATURE [Part::Cylinder] Cylinder014005962084  label="Válec975"
  Angle = 360
  AttacherType = Attacher::AttachEngine3D
  Height = 3
  Placement = pos=(9.9,-9.9,0) rot=(0,0,1;0rad)
  Radius = 2.8
FEATURE [Part::Cylinder] Cylinder014005962085  label="Válec976"
  Angle = 360
  AttacherType = Attacher::AttachEngine3D
  Height = 3
  Placement = pos=(-9.9,-9.9,0) rot=(0,0,1;0rad)
  Radius = 2.8
FEATURE [Part::Cylinder] Cylinder014005962086  label="Válec977"
  Angle = 360
  AttacherType = Attacher::AttachEngine3D
  Height = 3
  Placement = pos=(-9.9,9.9,0) rot=(0,0,1;0rad)
  Radius = 2.8
FEATURE [Part::MultiFuse] Fusion001089102007007003008034028016007006009018009025004007003004044  label="Diry PG005"
  Shapes = -> [Cylinder014005962086,Cylinder014005962083,Cylinder014005962085,Cylinder014005962084]
FEATURE [Part::MultiFuse] Fusion001089102007007003008034028016007006009018009025004007003004043  label="GeerPG002"
  Placement = pos=(0,47,0) rot=(-1,0,0;1.5708rad)
  Shapes = -> [Fusion001089102007007003008034028016007006009018009025004007003004042,Fusion001089102007007003008034028016007006009018009025004007003004044]
FEATURE [Part::Feature] Part__Feature001003  label="MOTOR_CAP003"
  Placement = pos=(0,0,0) rot=(0,1,0;0.523599rad)
  shape: bbox 106 x 12.2 x 106 mm, 94 faces (baked)
FEATURE [Part::Cut] Cut009003003009003003003007003002006019  label="MotorPG002"
  Base = -> Part__Feature001003
  Tool = -> Fusion001089102007007003008034028016007006009018009025004007003004043
FEATURE [Part::FeaturePython] cycloidgear010  # WARN: FeaturePython — macro-defined, semantics opaque (R4)
  AttacherType = Attacher::AttachEngine3D
  Placement = pos=(0,44,0) rot=(1,0,0;1.5708rad)
  backlash = 0
  beta = 0
  clearance = 0.25
  double_helix = false
  head = 0
  height = 10
  inner_diameter = 5
  module = 1
  numpoints = 15
  outer_diameter = 5
  teeth = 79
  version = 0.0.3
FEATURE [Part::Cylinder] Cylinder014005962087  label="Válec978"
  Angle = 360
  AttacherType = Attacher::AttachEngine3D
  Height = 10
  Placement = pos=(0,44,0) rot=(1,0,0;1.5708rad)
  Radius = 50
FEATURE [Part::Cylinder] Cylinder014005962088  label="Válec979"
  Angle = 360
  AttacherType = Attacher::AttachEngine3D
  Height = 10
  Placement = pos=(0,44,45.4) rot=(1,0,0;1.5708rad)
  Radius = 2.15
FEATURE [Part::Refine] Cylinder014005962089  label="Válec980"
  Placement = pos=(0,0,0) rot=(0,1,0;1.0472rad)
  Source = -> Cylinder014005962088
FEATURE [Part::Refine] Cylinder014005962090  label="Válec981"
  Placement = pos=(0,0,0) rot=(0,1,0;2.0944rad)
  Source = -> Cylinder014005962088
FEATURE [Part::Refine] Cylinder014005962091  label="Válec982"
  Placement = pos=(0,0,0) rot=(0,1,0;3.14159rad)
  Source = -> Cylinder014005962088
FEATURE [Part::Refine] Cylinder014005962092  label="Válec983"
  Placement = pos=(0,0,0) rot=(0,1,0;4.18879rad)
  Source = -> Cylinder014005962088
FEATURE [Part::Refine] Cylinder014005962093  label="Válec984"
  Placement = pos=(0,0,0) rot=(0,-1,0;1.0472rad)
  Source = -> Cylinder014005962088
FEATURE [Part::MultiFuse] Fusion001089102007007003008034028016007006009018009025004007003004045
  Shapes = -> [cycloidgear010,Cylinder014005962088,Cylinder014005962089,Cylinder014005962090,Cylinder014005962091,Cylinder014005962092,Cylinder014005962093]
FEATURE [Part::Chamfer] Chamfer030
  Base = -> Cylinder014005962087
  Edges = 2 edges r=1: [Edge1,Edge3]
FEATURE [Part::Cut] Cut009003003009003003003007003002006020  label="CIRCULAR_147"
  Base = -> Chamfer030
  Tool = -> Fusion001089102007007003008034028016007006009018009025004007003004045
FEATURE [Part::Refine] Part__Feature016001  label="HOUSING001"
  Source = -> Part__Feature016
FEATURE [Part::Part2DObjectPython] ShapeString074  # Draft 2D object (typed FeaturePython)
  FontFile = <userpath>/MyGit/Small-EQ-mount-OnStep/ttf/ARIALBD.TTF
  Placement = pos=(0,0,0) rot=(1,0,0;1.5708rad)
  Size = 3
  String = 12V
  Tracking = 0
FEATURE [Part::Part2DObjectPython] ShapeString075  # Draft 2D object (typed FeaturePython)
  FontFile = <userpath>/MyGit/Small-EQ-mount-OnStep/ttf/ARIALBD.TTF
  Placement = pos=(0,0,0) rot=(1,0,0;1.5708rad)
  Size = 3
  String = USB
  Tracking = 0
FEATURE [Part::Part2DObjectPython] ShapeString076  # Draft 2D object (typed FeaturePython)
  FontFile = <userpath>/MyGit/Small-EQ-mount-OnStep/ttf/ARIALBD.TTF
  Placement = pos=(0,0,0) rot=(1,0,0;1.5708rad)
  Size = 3
  String = 12V 
  Tracking = 0
FEATURE [Part::Feature] Cut009003003009003003003007003002006021  label="Port16a014De001"
  Placement = pos=(-34,-12,18) rot=(0,0,1;1.5708rad)
  shape: bbox 15 x 14.5 x 16.4 mm, 6 faces (baked)
FEATURE [Part::Feature] Cut009003003009003003003007003002006022  label="Port16a015Ra005"
  Placement = pos=(-34,10,18) rot=(0,0,1;1.5708rad)
  shape: bbox 15 x 14.5 x 16.4 mm, 6 faces (baked)
FEATURE [Part::Feature] Cut009003003009003003003007003002006023  label="Port16a013pwr001"
  Placement = pos=(-60,-18,18) rot=(0,0,1;1.5708rad)
  shape: bbox 15 x 14.5 x 16.4 mm, 6 faces (baked)
FEATURE [Part::Cylinder] Cylinder014005962094  label="Válec985"
  Angle = 360
  AttacherType = Attacher::AttachEngine3D
  Height = 10
  Placement = pos=(47,29.9,28) rot=(0,0,1;0rad)
  Radius = 1.2
FEATURE [Part::Cylinder] Cylinder014005962095  label="Válec986"
  Angle = 360
  AttacherType = Attacher::AttachEngine3D
  Height = 90
  Placement = pos=(40,45,8) rot=(1,0,0;1.5708rad)
  Radius = 1
FEATURE [Part::Box] Box021020  label="usbESP"
  AttacherType = Attacher::AttachEngine3D
  Height = 11
  Length = 20
  Placement = pos=(30,12,19.4) rot=(0,0,1;0rad)
  Width = 12.6
FEATURE [Part::Cylinder] Cylinder014005962096  label="cam002"
  Angle = 360
  AttacherType = Attacher::AttachEngine3D
  Height = 10
  Placement = pos=(0,-22.5,27) rot=(0,1,0;1.5708rad)
  Radius = 3.4
FEATURE [Part::Box] Box021021  label="RJ006ST005"
  AttacherType = Attacher::AttachEngine3D
  Height = 14
  Length = 20
  Placement = pos=(44,-8.5,16.4) rot=(0,0,1;0rad)
  Width = 16
FEATURE [Part::Extrusion] Extrude065  label="USB006"
  Base = -> ShapeString075
  Dir = (0,-1,-2e-16)
  DirMode = 2
  FaceMakerClass = Part::FaceMakerBullseye
  LengthFwd = 0.5
  LengthRev = 0
  Placement = pos=(53.5,13,25) rot=(0,0,1;1.5708rad)
  Solid = true
  Symmetric = false
FEATURE [Part::Box] Box021022  label="Pwr002"
  AttacherType = Attacher::AttachEngine3D
  Height = 11.4
  Length = 20
  Placement = pos=(40.9,-25.9,19) rot=(0,0,1;0rad)
  Width = 9.4
FEATURE [Part::Extrusion] Extrude066  label="12Vout001"
  Base = -> ShapeString074
  Dir = (0,-1,-2e-16)
  DirMode = 2
  FaceMakerClass = Part::FaceMakerBullseye
  LengthFwd = 0.5
  LengthRev = 0
  Placement = pos=(-53.5,-13.5,33) rot=(0,0,-1;1.5708rad)
  Solid = true
  Symmetric = false
FEATURE [Part::Cylinder] Cylinder014005962097  label="Válec987"
  Angle = 360
  AttacherType = Attacher::AttachEngine3D
  Height = 6.5
  Placement = pos=(-46.5,29.8,32) rot=(0,0,1;0rad)
  Radius = 5
FEATURE [Part::Cylinder] Cylinder014005962098  label="Válec988"
  Angle = 360
  AttacherType = Attacher::AttachEngine3D
  Height = 10
  Placement = pos=(-46.5,29.8,28) rot=(0,0,1;0rad)
  Radius = 1.2
FEATURE [Part::Cylinder] Cylinder014005962099  label="Válec989"
  Angle = 360
  AttacherType = Attacher::AttachEngine3D
  Height = 10
  Placement = pos=(-46.5,-30.9,28) rot=(0,0,1;0rad)
  Radius = 1.2
FEATURE [Part::Extrusion] Extrude067  label="12V006"
  Base = -> ShapeString076
  Dir = (0,-1,-2e-16)
  DirMode = 2
  FaceMakerClass = Part::FaceMakerBullseye
  LengthFwd = 0.5
  LengthRev = 0
  Placement = pos=(53.5,-25,33) rot=(0,0,1;1.5708rad)
  Solid = true
  Symmetric = false
FEATURE [Part::Cylinder] Cylinder014005962100  label="Dira stres001"
  Angle = 360
  AttacherType = Attacher::AttachEngine3D
  Height = 10
  Placement = pos=(0,0,32) rot=(0,0,1;0rad)
  Radius = 6
FEATURE [Part::Cylinder] Cylinder014005962101  label="Válec990"
  Angle = 360
  AttacherType = Attacher::AttachEngine3D
  Height = 6.5
  Placement = pos=(-46.5,-30.9,32) rot=(0,0,1;0rad)
  Radius = 5
FEATURE [Part::Cylinder] Cylinder014005962102  label="Válec991"
  Angle = 360
  AttacherType = Attacher::AttachEngine3D
  Height = 6.5
  Placement = pos=(47,-30.9,32) rot=(0,0,1;0rad)
  Radius = 5
FEATURE [Part::Cylinder] Cylinder014005962103  label="Válec992"
  Angle = 360
  AttacherType = Attacher::AttachEngine3D
  Height = 10
  Placement = pos=(47,-30.9,28) rot=(0,0,1;0rad)
  Radius = 1.2
FEATURE [Part::MultiFuse] Fusion001089102007007003008034028016007006009018009025004007003004051  label="dir srouby006"
  Shapes = -> [Cylinder014005962094,Cylinder014005962098,Cylinder014005962103,Cylinder014005962099]
FEATURE [Part::Cylinder] Cylinder014005962104  label="Led003"
  Angle = 360
  AttacherType = Attacher::AttachEngine3D
  Height = 15
  Placement = pos=(44,-12,27) rot=(0,1,0;1.5708rad)
  Radius = 1.75
FEATURE [Part::Cylinder] Cylinder014005962105  label="Válec993"
  Angle = 360
  AttacherType = Attacher::AttachEngine3D
  Height = 90
  Placement = pos=(-40,45,8) rot=(1,0,0;1.5708rad)
  Radius = 1
FEATURE [Part::MultiFuse] Fusion001089102007007003008034028016007006009018009025004007003004047  label="hornidiry009"
  Shapes = -> [Cylinder014005962095,Cylinder014005962105]
FEATURE [Part::Cylinder] Cylinder014005962106  label="Válec994"
  Angle = 360
  AttacherType = Attacher::AttachEngine3D
  Height = 6.5
  Placement = pos=(47,29.9,32) rot=(0,0,1;0rad)
  Radius = 5
FEATURE [Part::MultiFuse] Fusion001089102007007003008034028016007006009018009025004007003004048  label="sloupky001"
  Shapes = -> [Cylinder014005962106,Cylinder014005962097,Cylinder014005962102,Cylinder014005962101]
FEATURE [Part::Box] Box021023  label="PWRsw002"
  AttacherType = Attacher::AttachEngine3D
  Height = 9
  Length = 15
  Placement = pos=(-57,8,16) rot=(0,0,1;0rad)
  Width = 15
FEATURE [Part::Box] Box021024  label="RJ006RA001"
  AttacherType = Attacher::AttachEngine3D
  Height = 14
  Length = 20
  Placement = pos=(0,1,16.4) rot=(0,0,1;0rad)
  Width = 16
FEATURE [Part::Box] Box021025  label="RJ006DE001"
  AttacherType = Attacher::AttachEngine3D
  Height = 14
  Length = 20
  Placement = pos=(0,-15,16.4) rot=(0,0,1;0rad)
  Width = 16
FEATURE [Part::Cylinder] Cylinder014005962107  label="Led004"
  Angle = 360
  AttacherType = Attacher::AttachEngine3D
  Height = 15
  Placement = pos=(44,-12,21.5) rot=(0,1,0;1.5708rad)
  Radius = 1.75
FEATURE [Part::Cylinder] Cylinder014005962108  label="extpwr001"
  Angle = 360
  AttacherType = Attacher::AttachEngine3D
  Height = 10
  Placement = pos=(-55,-18,18) rot=(0,1,0;1.5708rad)
  Radius = 4.1
FEATURE [Part::Cylinder] Cylinder014005962109  label="camLed001"
  Angle = 360
  AttacherType = Attacher::AttachEngine3D
  Height = 10
  Placement = pos=(0,-22.5,20) rot=(0,1,0;1.5708rad)
  Radius = 1.8
FEATURE [Part::Cylinder] Cylinder014005962110  label="Válec995"
  Angle = 360
  AttacherType = Attacher::AttachEngine3D
  Height = 7
  Placement = pos=(0,0,33) rot=(0,0,1;0rad)
  Radius = 53
FEATURE [Part::Box] Box021026  label="Krychle134"
  AttacherType = Attacher::AttachEngine3D
  Height = 35
  Length = 108
  Placement = pos=(-54,-38,5) rot=(0,0,1;0rad)
  Width = 76
FEATURE [Part::Box] Box021027  label="Krychle135"
  AttacherType = Attacher::AttachEngine3D
  Height = 36
  Length = 104
  Placement = pos=(-52,-36,2) rot=(0,0,1;0rad)
  Width = 72
FEATURE [Part::Cylinder] Cylinder014005962111  label="Válec996"
  Angle = 360
  AttacherType = Attacher::AttachEngine3D
  Height = 7
  Placement = pos=(0,-45,33) rot=(0,0,1;0rad)
  Radius = 2.65
FEATURE [Part::Cylinder] Cylinder014005962112  label="Válec997"
  Angle = 360
  AttacherType = Attacher::AttachEngine3D
  Height = 5.4
  Placement = pos=(0,-45,33) rot=(0,0,1;0rad)
  Radius = 4.3
FEATURE [Part::MultiFuse] Fusion001089102007007003008034028016007006009018009025004007003004052  label="Inbus013"
  Shapes = -> [Cylinder014005962111,Cylinder014005962112]
FEATURE [Part::Refine] Fusion001089102007007003008034028016007006009018009025004007003004053  label="Inbus014"
  Placement = pos=(0,0,0) rot=(0,0,1;1.0472rad)
  Source = -> Fusion001089102007007003008034028016007006009018009025004007003004052
FEATURE [Part::Refine] Fusion001089102007007003008034028016007006009018009025004007003004054  label="Inbus015"
  Placement = pos=(0,0,0) rot=(0,0,1;2.0944rad)
  Source = -> Fusion001089102007007003008034028016007006009018009025004007003004052
FEATURE [Part::Refine] Fusion001089102007007003008034028016007006009018009025004007003004055  label="Inbus016"
  Placement = pos=(0,0,0) rot=(0,0,1;3.14159rad)
  Source = -> Fusion001089102007007003008034028016007006009018009025004007003004052
FEATURE [Part::Refine] Fusion001089102007007003008034028016007006009018009025004007003004056  label="Inbus017"
  Placement = pos=(0,0,0) rot=(0,0,1;4.18879rad)
  Source = -> Fusion001089102007007003008034028016007006009018009025004007003004052
FEATURE [Part::Refine] Fusion001089102007007003008034028016007006009018009025004007003004057  label="Inbus018"
  Placement = pos=(0,0,0) rot=(0,0,-1;1.0472rad)
  Source = -> Fusion001089102007007003008034028016007006009018009025004007003004052
FEATURE [Part::MultiFuse] Fusion001089102007007003008034028016007006009018009025004007003004058  label="Inbus019"
  Shapes = -> [Fusion001089102007007003008034028016007006009018009025004007003004052,Fusion001089102007007003008034028016007006009018009025004007003004053,Fusion001089102007007003008034028016007006009018009025004007003004054,Fusion001089102007007003008034028016007006009018009025004007003004055,Fusion001089102007007003008034028016007006009018009025004007003004056,+1 more]
FEATURE [Part::Part2DObjectPython] ShapeString077  # Draft 2D object (typed FeaturePython)
  FontFile = <userpath>/MyGit/Small-EQ-mount-OnStep/ttf/ARIALBD.TTF
  Placement = pos=(0,0,0) rot=(-1,0,0;1.5708rad)
  Size = 10
  String = OnStep  HrEM
  Tracking = 0
FEATURE [Part::Extrusion] Extrude068  label="Hrem001"
  Base = -> ShapeString077
  Dir = (0,1,-2e-16)
  DirMode = 2
  FaceMakerClass = Part::FaceMakerBullseye
  LengthFwd = 0.5
  LengthRev = 0
  Placement = pos=(43,37.5,16) rot=(0,1,0;3.14159rad)
  Solid = true
  Symmetric = false
FEATURE [Part::Part2DObjectPython] ShapeString078  # Draft 2D object (typed FeaturePython)
  FontFile = <userpath>/MyGit/Small-EQ-mount-OnStep/ttf/ARIALBD.TTF
  Placement = pos=(0,0,0) rot=(1,0,0;1.5708rad)
  Size = 3
  String = ST4 SHC
  Tracking = 0
FEATURE [Part::Extrusion] Extrude069  label="ST005"
  Base = -> ShapeString078
  Dir = (0,-1,2e-16)
  DirMode = 2
  FaceMakerClass = Part::FaceMakerBullseye
  LengthFwd = 0.5
  LengthRev = 0
  Placement = pos=(53.5,-8.5,33) rot=(0,0,1;1.5708rad)
  Solid = true
  Symmetric = false
FEATURE [Part::Chamfer] Chamfer031
  Base = -> Cylinder014005962110
  Edges = 2 edges r=1: [Edge1,Edge3]
FEATURE [Part::MultiFuse] Fusion001089102007007003008034028016007006009018009025004007003004059
  Shapes = -> [Box021026,Chamfer031]
FEATURE [Part::Cut] Cut009003003009003003003007003002006024
  Base = -> Fusion001089102007007003008034028016007006009018009025004007003004059
  Tool = -> Box021027
FEATURE [Part::MultiFuse] Fusion001089102007007003008034028016007006009018009025004007003004060
  Shapes = -> [Fusion001089102007007003008034028016007006009018009025004007003004048,Cut009003003009003003003007003002006024]
FEATURE [Part::Part2DObjectPython] ShapeString079  # Draft 2D object (typed FeaturePython)
  FontFile = <userpath>/MyGit/Small-EQ-mount-OnStep/ttf/ARIALBD.TTF
  Placement = pos=(0,0,0) rot=(1,0,0;1.5708rad)
  Size = 3
  String = Power
  Tracking = 0
FEATURE [Part::Extrusion] Extrude070  label="Pwr003"
  Base = -> ShapeString079
  Dir = (0,-1,2e-16)
  DirMode = 2
  FaceMakerClass = Part::FaceMakerBullseye
  LengthFwd = 0.5
  LengthRev = 0
  Placement = pos=(-53.5,22,33) rot=(0,0,-1;1.5708rad)
  Solid = true
  Symmetric = false
FEATURE [Part::MultiFuse] Fusion001089102007007003008034028016007006009018009025004007003004049  label="texty012"
  Shapes = -> [Extrude066,Extrude067,Extrude065,Extrude068,Extrude069,Extrude070]
FEATURE [Part::Box] Box021028  label="usbTeensy "
  AttacherType = Attacher::AttachEngine3D
  Height = 4.5
  Length = 10
  Placement = pos=(46,13,14) rot=(0,0,1;0rad)
  Width = 9
FEATURE [Part::MultiFuse] Fusion001089102007007003008034028016007006009018009025004007003004050  label="PCB008"
  Shapes = -> [Box021022,Box021020,Box021021,Cut009003003009003003003007003002006023,Cut009003003009003003003007003002006021,Cut009003003009003003003007003002006022,Box021023,Box021024,Box021025,Cylinder014005962107,Cylinder014005962104,Cylinder014005962096,Cylinder014005962108,Cylinder014005962109,Box021028]
FEATURE [Part::MultiFuse] Fusion001089102007007003008034028016007006009018009025004007003004046  label="Diry001"
  Shapes = -> [Fusion001089102007007003008034028016007006009018009025004007003004050,Fusion001089102007007003008034028016007006009018009025004007003004051,Cylinder014005962100,Fusion001089102007007003008034028016007006009018009025004007003004047,Fusion001089102007007003008034028016007006009018009025004007003004049,Fusion001089102007007003008034028016007006009018009025004007003004058]
FEATURE [Part::Cut] Cut009003003009003003003007003002006025
  Base = -> Fusion001089102007007003008034028016007006009018009025004007003004060
  Tool = -> Fusion001089102007007003008034028016007006009018009025004007003004046
FEATURE [Part::Fillet] Fillet003  label="OnstepBoxTeensy"
  Base = -> Cut009003003009003003003007003002006025
  Edges = 4 edges r=2: [Edge143,Edge145,Edge244,Edge411]
FEATURE [Part::FeaturePython] frustum  # WARN: FeaturePython — macro-defined, semantics opaque (R4)
  FacesNumber = 4
  Height = 15
  Placement = pos=(0,0,0) rot=(0,0,1;0.785398rad)
  Radius1 = 31.1127
  Radius2 = 26.9444
FEATURE [Part::Feature] Matrix_Deformation
  Placement = pos=(0,0,0) rot=(0,0,1;0.785398rad)
  shape: bbox 336 x 88 x 15 mm, 6 faces (baked)
FEATURE [Part::Box] cube008
  AttacherType = Attacher::AttachEngine3D
  Height = 17
  Length = 84
  Placement = pos=(-126,-45,-1) rot=(0,0,1;0rad)
  Width = 90
FEATURE [Part::Box] cube009
  AttacherType = Attacher::AttachEngine3D
  Height = 17
  Length = 84
  Placement = pos=(42,-45,-1) rot=(0,0,1;0rad)
  Width = 90
FEATURE [Part::Fuse] Group
  Base = -> cube008
  Tool = -> cube009
FEATURE [Part::Cut] difference002  label="Vixen001"
  Base = -> Matrix_Deformation
  Placement = pos=(-10,0,41.5) rot=(0,1,0;1.5708rad)
  Tool = -> Group
FEATURE [Part::Refine] Fusion001089102007007003008034028016007006009018009025004007003004009001  label="Srouny "
  Source = -> Fusion001089102007007003008034028016007006009018009025004007003004009
FEATURE [Part::Cylinder] Cylinder014005962113  label="Válec998"
  Angle = 360
  AttacherType = Attacher::AttachEngine3D
  Height = 10
  Placement = pos=(-15,0,3) rot=(0,1,0;1.5708rad)
  Radius = 1.3
FEATURE [Part::Cylinder] Cylinder014005962114  label="Válec999"
  Angle = 360
  AttacherType = Attacher::AttachEngine3D
  Height = 10
  Placement = pos=(-15,0,81) rot=(0,1,0;1.5708rad)
  Radius = 1.3
FEATURE [Part::MultiFuse] Fusion001089102007007003008034028016007006009018009025004007003004009002
  Shapes = -> [Cylinder014005962114,Fusion001089102007007003008034028016007006009018009025004007003004009001,Cylinder014005962113]
FEATURE [Part::Cut] Cut009003003009003003003007003002006026  label="Vixen002"
  Base = -> difference002
  Tool = -> Fusion001089102007007003008034028016007006009018009025004007003004009002
FEATURE [Part::Cylinder] Cylinder014005962115  label="Válec1000"
  Angle = 360
  AttacherType = Attacher::AttachEngine3D
  Height = 40
  Radius = 30
FEATURE [Part::Box] Box021029  label="Krychle136"
  AttacherType = Attacher::AttachEngine3D
  Height = 40
  Length = 20
  Placement = pos=(-35,-30,0) rot=(0,0,1;0rad)
  Width = 60
FEATURE [Part::Box] Box021030  label="Krychle137"
  AttacherType = Attacher::AttachEngine3D
  Height = 40
  Length = 65
  Placement = pos=(0,-10,0) rot=(0,0,1;0.785398rad)
  Width = 14
FEATURE [Part::MultiFuse] Fusion001089102007007003008034028016007006009018009025004007003004009003  label="Interni"
  Shapes = -> [Box021030,Cylinder014005962115,Box021029]
FEATURE [Part::Cylinder] Cylinder014005962116  label="Válec1001"
  Angle = 360
  AttacherType = Attacher::AttachEngine3D
  Height = 40
  Radius = 6.16
FEATURE [Part::Cylinder] Cylinder014005962117  label="Válec1002"
  Angle = 360
  AttacherType = Attacher::AttachEngine3D
  Height = 30
  Placement = pos=(-42,17,20) rot=(0,1,0;1.5708rad)
  Radius = 4.16
FEATURE [Part::Cylinder] Cylinder014005962118  label="Válec1003"
  Angle = 360
  AttacherType = Attacher::AttachEngine3D
  Height = 30
  Placement = pos=(-42,-17,20) rot=(0,1,0;1.5708rad)
  Radius = 4.16
FEATURE [Part::Prism] Prism021  label="Hranol021"
  AttacherType = Attacher::AttachEngine3D
  Circumradius = 7.5
  FirstAngle = 0
  Height = 6.5
  Placement = pos=(0,0,0) rot=(0,1,0;1.5708rad)
  Polygon = 6
  SecondAngle = 0
FEATURE [Part::Box] Box021031  label="Krychle138"
  AttacherType = Attacher::AttachEngine3D
  Height = 20
  Length = 6.5
  Placement = pos=(0,-6.5,0) rot=(0,0,1;0rad)
  Width = 13
FEATURE [Part::MultiFuse] Fusion001089102007007003008034028016007006009018009025004007003004009004  label="M121"
  Placement = pos=(-28,-17,20) rot=(1,0,0;1.5708rad)
  Shapes = -> [Box021031,Prism021]
FEATURE [Part::Box] Box021032  label="Krychle139"
  AttacherType = Attacher::AttachEngine3D
  Height = 20
  Length = 6.5
  Placement = pos=(0,-6.5,-20) rot=(0,0,1;0rad)
  Width = 13
FEATURE [Part::Prism] Prism022  label="Hranol022"
  AttacherType = Attacher::AttachEngine3D
  Circumradius = 7.5
  FirstAngle = 0
  Height = 6.5
  Placement = pos=(0,0,0) rot=(0,1,0;1.5708rad)
  Polygon = 6
  SecondAngle = 0
FEATURE [Part::MultiFuse] Fusion001089102007007003008034028016007006009018009025004007003004009005  label="M122"
  Placement = pos=(-28,17,20) rot=(1,0,0;1.5708rad)
  Shapes = -> [Box021032,Prism022]
FEATURE [Part::Cylinder] Cylinder014005962120  label="Válec1005"
  Angle = 360
  AttacherType = Attacher::AttachEngine3D
  Height = 50
  Placement = pos=(0,0,20) rot=(0,1,0;1.5708rad)
  Radius = 2.4
FEATURE [Part::Cylinder] Cylinder014005962120002  label="Válec1007"
  Angle = 360
  AttacherType = Attacher::AttachEngine3D
  Height = 75
  Placement = pos=(0,0,20) rot=(0,1,0;1.5708rad)
  Radius = 2.9
FEATURE [Part::Cylinder] Cylinder014005962120003  label="Válec1008"
  Angle = 360
  AttacherType = Attacher::AttachEngine3D
  Height = 5.5
  Placement = pos=(52.5,0,20) rot=(0,1,0;1.5708rad)
  Radius = 4.3
FEATURE [Part::MultiFuse] Fusion001089102007007003008034028016007006009018009025004007003004009007
  Placement = pos=(0,0,0) rot=(0,0,1;0.785398rad)
  Shapes = -> [Cylinder014005962120002,Cylinder014005962120003]
FEATURE [Part::Cylinder] Cylinder014005962119  label="Válec1004"
  Angle = 360
  AttacherType = Attacher::AttachEngine3D
  Height = 32
  Placement = pos=(-40,0,20) rot=(0,1,0;1.5708rad)
  Radius = 2.9
FEATURE [Part::MultiFuse] Fusion001089102007007003008034028016007006009018009025004007003004009006  label="sr"
  Shapes = -> [Cylinder014005962116,Cylinder014005962117,Cylinder014005962118,Fusion001089102007007003008034028016007006009018009025004007003004009004,Fusion001089102007007003008034028016007006009018009025004007003004009005,Cylinder014005962119,Fusion001089102007007003008034028016007006009018009025004007003004009007]
FEATURE [Part::Cut] Cut009003003009003003003007003002006027  label="AZ"
  Base = -> Fusion001089102007007003008034028016007006009018009025004007003004009003
  Tool = -> Fusion001089102007007003008034028016007006009018009025004007003004009006
FEATURE [Part::Refine] Cut009003003009003003003007003002006027001  label="AZ001"
  Source = -> Cut009003003009003003003007003002006027
FEATURE [Part::Chamfer] Chamfer032
  Base = -> Cut009003003009003003003007003002006027001
  Edges = 12 edges r=1.5: [Edge5,Edge6,Edge7,Edge12,Edge13,Edge14,Edge23,Edge25,Edge26,Edge27,Edge43,Edge44]
FEATURE [Part::Cylinder] Cylinder014005962120014  label="Válec1019"
  Angle = 360
  AttacherType = Attacher::AttachEngine3D
  Height = 35
  Placement = pos=(0,43.5,20) rot=(0,0,1;0rad)
  Radius = 1.65
FEATURE [Part::Prism] Prism023  label="Hranol023"
  AttacherType = Attacher::AttachEngine3D
  Circumradius = 3.2
  FirstAngle = 0
  Height = 2.5
  Placement = pos=(0,0,23) rot=(0,0,1;0.523599rad)
  Polygon = 6
  SecondAngle = 0
FEATURE [Part::Box] Box021036  label="Krychle143"
  AttacherType = Attacher::AttachEngine3D
  Height = 3.5
  Length = 5.5
  Placement = pos=(-2.75,-10,23) rot=(0,0,1;0rad)
  Width = 10
FEATURE [Part::MultiFuse] Fusion001089102007007003008034028016007006009018009025004007003004009016  label="Matk007"
  Placement = pos=(0,43.5,0) rot=(0,0,1;0rad)
  Shapes = -> [Box021036,Prism023]
FEATURE [Part::Cylinder] Cylinder014005962120015  label="Válec1020"
  Angle = 360
  AttacherType = Attacher::AttachEngine3D
  Height = 3
  Placement = pos=(0,43.5,36) rot=(0,0,1;0rad)
  Radius = 3.3
FEATURE [Part::MultiFuse] Fusion001089102007007003008034028016007006009018009025004007003004009017  label="S020"
  Placement = pos=(0,0,0) rot=(0,0,1;1.0472rad)
  Shapes = -> [Cylinder014005962120014,Fusion001089102007007003008034028016007006009018009025004007003004009016,Cylinder014005962120015]
FEATURE [Part::Refine] Fusion001089102007007003008034028016007006009018009025004007003004009018  label="S021"
  Placement = pos=(0,0,0) rot=(0,0,1;1.0472rad)
  Source = -> Fusion001089102007007003008034028016007006009018009025004007003004009017
FEATURE [Part::Refine] Fusion001089102007007003008034028016007006009018009025004007003004009019  label="S022"
  Placement = pos=(0,0,0) rot=(0,0,1;3.14159rad)
  Source = -> Fusion001089102007007003008034028016007006009018009025004007003004009017
FEATURE [Part::Refine] Fusion001089102007007003008034028016007006009018009025004007003004009020  label="S023"
  Placement = pos=(0,0,0) rot=(0,0,-1;2.0944rad)
  Source = -> Fusion001089102007007003008034028016007006009018009025004007003004009017
FEATURE [Part::MultiFuse] Fusion001089102007007003008034028016007006009018009025004007003004009021  label="S024"
  Placement = pos=(0,0,-32) rot=(0,0,1;0rad)
  Shapes = -> [Fusion001089102007007003008034028016007006009018009025004007003004009017,Fusion001089102007007003008034028016007006009018009025004007003004009018,Fusion001089102007007003008034028016007006009018009025004007003004009019,Fusion001089102007007003008034028016007006009018009025004007003004009020]
FEATURE [Part::Cylinder] Cylinder014005962120016  label="Válec1021"
  Angle = 360
  AttacherType = Attacher::AttachEngine3D
  Height = 16
  Radius = 2.15
FEATURE [Part::Cylinder] Cylinder014005962120017  label="Válec1022"
  Angle = 360
  AttacherType = Attacher::AttachEngine3D
  Height = 4
  Placement = pos=(0,0,16) rot=(0,0,1;0rad)
  Radius = 3.5
FEATURE [Part::MultiFuse] Fusion001089102007007003008034028016007006009018009025004007003004009022  label="M4nut052"
  Placement = pos=(10,0,41.5) rot=(0,-1,0;1.5708rad)
  Shapes = -> [Cylinder014005962120016,Cylinder014005962120017]
FEATURE [Part::Refine] Fusion001089102007007003008034028016007006009018009025004007003004009023  label="M4nut053"
  Placement = pos=(0,10,0) rot=(0,0,1;0rad)
  Source = -> Fusion001089102007007003008034028016007006009018009025004007003004009022
FEATURE [Part::Refine] Fusion001089102007007003008034028016007006009018009025004007003004009024  label="M4nut054"
  Placement = pos=(0,-10,0) rot=(0,0,1;0rad)
  Source = -> Fusion001089102007007003008034028016007006009018009025004007003004009022
FEATURE [Part::Refine] Fusion001089102007007003008034028016007006009018009025004007003004009025  label="M4nut055"
  Placement = pos=(0,0,25) rot=(0,0,1;0rad)
  Source = -> Fusion001089102007007003008034028016007006009018009025004007003004009022
FEATURE [Part::Refine] Fusion001089102007007003008034028016007006009018009025004007003004009026  label="M4nut056"
  Placement = pos=(0,0,-25) rot=(0,0,1;0rad)
  Source = -> Fusion001089102007007003008034028016007006009018009025004007003004009022
FEATURE [Part::MultiFuse] Fusion001089102007007003008034028016007006009018009025004007003004009027
  Shapes = -> [Fusion001089102007007003008034028016007006009018009025004007003004009023,Fusion001089102007007003008034028016007006009018009025004007003004009024,Fusion001089102007007003008034028016007006009018009025004007003004009025,Fusion001089102007007003008034028016007006009018009025004007003004009026]
FEATURE [Part::Feature] Matrix_Deformation001
  Placement = pos=(0,0,0) rot=(0,0,1;0.785398rad)
  shape: bbox 336 x 88 x 15 mm, 6 faces (baked)
FEATURE [Part::Box] cube010
  AttacherType = Attacher::AttachEngine3D
  Height = 17
  Length = 84
  Placement = pos=(-136,-45,-1) rot=(0,0,1;0rad)
  Width = 90
FEATURE [Part::Box] cube011
  AttacherType = Attacher::AttachEngine3D
  Height = 17
  Length = 84
  Placement = pos=(52,-45,-1) rot=(0,0,1;0rad)
  Width = 90
FEATURE [Part::Fuse] Group001
  Base = -> cube010
  Tool = -> cube011
FEATURE [Part::Cut] difference003  label="Vixen003"
  Base = -> Matrix_Deformation001
  Placement = pos=(-10,0,41.5) rot=(0,1,0;1.5708rad)
  Tool = -> Group001
FEATURE [Part::Refine] Fusion001089102007007003008034028016007006009018009025004007003004009028  label="Srouny 001"
  Source = -> Fusion001089102007007003008034028016007006009018009025004007003004009027
FEATURE [Part::Cylinder] Cylinder014005962120018  label="Válec1023"
  Angle = 360
  AttacherType = Attacher::AttachEngine3D
  Height = 10
  Placement = pos=(-15,0,-7) rot=(0,1,0;1.5708rad)
  Radius = 1.3
FEATURE [Part::Cylinder] Cylinder014005962120019  label="Válec1024"
  Angle = 360
  AttacherType = Attacher::AttachEngine3D
  Height = 10
  Placement = pos=(-15,0,91) rot=(0,1,0;1.5708rad)
  Radius = 1.3
FEATURE [Part::MultiFuse] Fusion001089102007007003008034028016007006009018009025004007003004009029
  Shapes = -> [Cylinder014005962120019,Fusion001089102007007003008034028016007006009018009025004007003004009028,Cylinder014005962120018]
FEATURE [Part::Cut] Cut009003003009003003003007003002006027002  label="Vixen004"
  Base = -> difference003
  Tool = -> Fusion001089102007007003008034028016007006009018009025004007003004009029
FEATURE [Part::Cylinder] Cylinder014005962120021  label="Válec1026"
  Angle = 360
  AttacherType = Attacher::AttachEngine3D
  Height = 12
  Radius = 49
FEATURE [Part::Cylinder] Cylinder014005962120022  label="Válec1027"
  Angle = 360
  AttacherType = Attacher::AttachEngine3D
  Height = 10
  Placement = pos=(0,0,12) rot=(0,0,1;0rad)
  Radius = 39.8
FEATURE [Part::Cylinder] Cylinder014005962120023  label="Válec1028"
  Angle = 360
  AttacherType = Attacher::AttachEngine3D
  Height = 30
  Radius = 15.5
FEATURE [Part::FeaturePython] Tube006  # WARN: FeaturePython — macro-defined, semantics opaque (R4)
  AttacherType = Attacher::AttachEngine3D
  Height = 4
  InnerRadius = 37.5
  OuterRadius = 49
FEATURE [Part::Box] Box021037  label="Krychle144"
  AttacherType = Attacher::AttachEngine3D
  Height = 8
  Length = 38
  Placement = pos=(20,-8,4) rot=(0,0,1;0rad)
  Width = 16
FEATURE [Part::MultiFuse] Fusion001089102007007003008034028016007006009018009025004007003004009030  label="main"
  Shapes = -> [Cylinder014005962120021,Cylinder014005962120022]
FEATURE [Part::Cylinder] Cylinder014005962120024  label="Válec1029"
  Angle = 360
  AttacherType = Attacher::AttachEngine3D
  Height = 12
  Placement = pos=(52,0,0) rot=(0,0,1;0rad)
  Radius = 2
FEATURE [Part::Prism] Prism024  label="Hranol024"
  AttacherType = Attacher::AttachEngine3D
  Circumradius = 4.8
  FirstAngle = 0
  Height = 5
  Placement = pos=(52,0,7.5) rot=(0,0,1;0rad)
  Polygon = 6
  SecondAngle = 0
FEATURE [Part::MultiFuse] Fusion001089102007007003008034028016007006009018009025004007003004009033
  Shapes = -> [Cylinder014005962120024,Prism024,Fusion001089102007007003008034028016007006009018009025004007003004009021]
FEATURE [Part::Cylinder] Cylinder014005962120025  label="Válec1030"
  Angle = 360
  AttacherType = Attacher::AttachEngine3D
  Height = 4
  Radius = 31
FEATURE [Part::MultiFuse] Fusion001089102007007003008034028016007006009018009025004007003004009031  label="diry"
  Shapes = -> [Cylinder014005962120023,Tube006,Cylinder014005962120025]
FEATURE [Part::Cut] Cut009003003009003003003007003002006027003
  Base = -> Fusion001089102007007003008034028016007006009018009025004007003004009030
  Tool = -> Fusion001089102007007003008034028016007006009018009025004007003004009031
FEATURE [Part::MultiFuse] Fusion001089102007007003008034028016007006009018009025004007003004009032
  Shapes = -> [Box021037,Cut009003003009003003003007003002006027003]
FEATURE [Part::Cut] Cut009003003009003003003007003002006027004
  Base = -> Fusion001089102007007003008034028016007006009018009025004007003004009032
  Tool = -> Fusion001089102007007003008034028016007006009018009025004007003004009033
FEATURE [Part::Chamfer] Chamfer033
  Base = -> Cut009003003009003003003007003002006027004
  Edges = 4 edges r=1.5: [Edge12,Edge13,Edge78,Edge79]
FEATURE [Part::FeaturePython] Tube007  # WARN: FeaturePython — macro-defined, semantics opaque (R4)
  AttacherType = Attacher::AttachEngine3D
  Height = 30
  InnerRadius = 5.2
  OuterRadius = 13
FEATURE [Part::Box] Box021038  label="Krychle145"
  AttacherType = Attacher::AttachEngine3D
  Height = 15
  Length = 40
  Placement = pos=(-20,-6,-2) rot=(0,0,1;0rad)
  Width = 8
FEATURE [Part::Cylinder] Cylinder014005962120026  label="Válec1031"
  Angle = 360
  AttacherType = Attacher::AttachEngine3D
  Height = 12
  Placement = pos=(0,6,5) rot=(1,0,0;1.5708rad)
  Radius = 3.15
FEATURE [Part::Prism] Prism025  label="Hranol025"
  AttacherType = Attacher::AttachEngine3D
  Circumradius = 5.52
  FirstAngle = 0
  Height = 5
  Placement = pos=(0,2,5) rot=(1,0,0;1.5708rad)
  Polygon = 6
  SecondAngle = 0
FEATURE [Part::Cylinder] Cylinder014005962120027  label="Válec1032"
  Angle = 360
  AttacherType = Attacher::AttachEngine3D
  Height = 12
  Placement = pos=(15,6,5) rot=(1,0,0;1.5708rad)
  Radius = 2.15
FEATURE [Part::Cylinder] Cylinder014005962120028  label="Válec1033"
  Angle = 360
  AttacherType = Attacher::AttachEngine3D
  Height = 12
  Placement = pos=(-15,6,5) rot=(1,0,0;1.5708rad)
  Radius = 2.15
FEATURE [Part::Cylinder] Cylinder014005962120029  label="Válec1034"
  Angle = 360
  AttacherType = Attacher::AttachEngine3D
  Height = 4
  Placement = pos=(15,-3,5) rot=(1,0,0;1.5708rad)
  Radius = 3.5
FEATURE [Part::Cylinder] Cylinder014005962120030  label="Válec1035"
  Angle = 360
  AttacherType = Attacher::AttachEngine3D
  Height = 4
  Placement = pos=(-15,-3,5) rot=(1,0,0;1.5708rad)
  Radius = 3.4
FEATURE [Part::MultiFuse] Fusion001089102007007003008034028016007006009018009025004007003004009034
  Shapes = -> [Cylinder014005962120026,Prism025,Cylinder014005962120027,Cylinder014005962120028,Cylinder014005962120029,Cylinder014005962120030]
FEATURE [Part::Cut] Cut009003003009003003003007003002006027005
  Base = -> Box021038
  Tool = -> Fusion001089102007007003008034028016007006009018009025004007003004009034
FEATURE [Part::Fillet] Fillet004
  Base = -> Cut009003003009003003003007003002006027005
  Edges = 8 edges r=1: [Edge1,Edge2,Edge4,Edge5,Edge6,Edge7,Edge12,Edge23]
FEATURE [App::Part] Part001  label="Working "
  Group = -> [Cylinder014005891,Cylinder014005892,Cylinder014005893,Cylinder014005894,Cylinder014005895,Fusion001089102007007003008034002,cycloidgear008,Chamfer015,Cylinder014005896,Cylinder014005897,Cut009003003009003003002,Fusion001089102007007003008017,Fusion001089102007007003008018,Cylinder014005883,Cylinder014005884,Cylinder014005885,Fusion001089102007007003008019,Cylinder014005886,Cylinder014005887,+802 more]
  Origin = -> Origin002
  Placement = pos=(0,0,-22) rot=(0,0,1;0rad)
FEATURE [Part::Refine] Cut009003003009003003003007003002006027006  label="CIRCULAR_148"
  Source = -> Cut
note: 1 file-system path scrubbed to <path> (originals preserved in the JSON sidecar)
